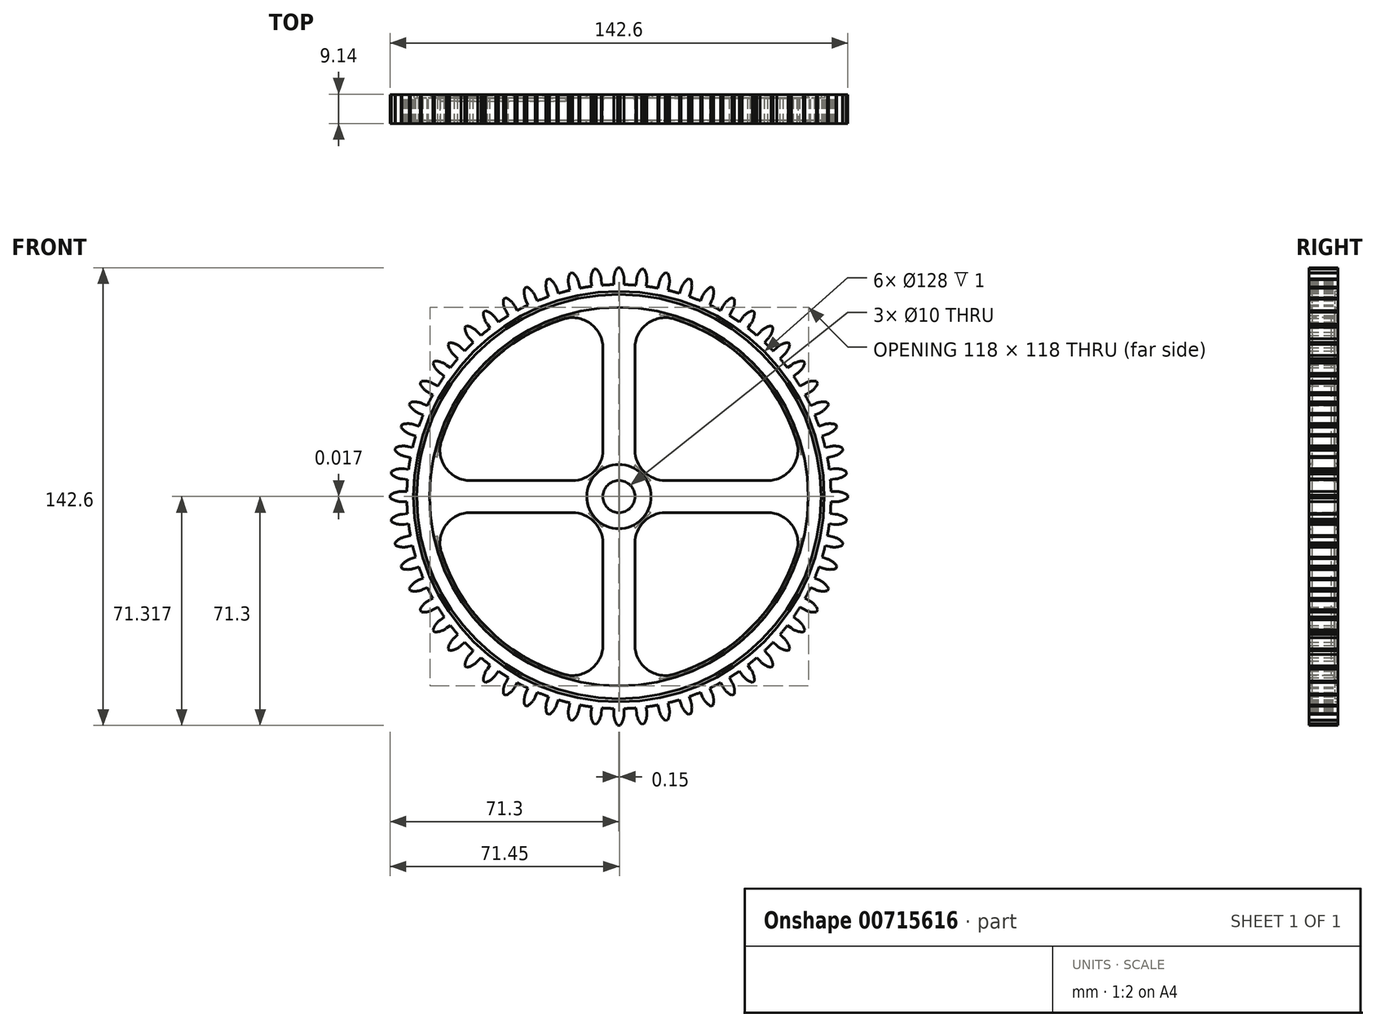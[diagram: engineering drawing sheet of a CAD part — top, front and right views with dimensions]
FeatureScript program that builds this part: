
annotation { "Feature Type Name" : "Feature", "Feature Type Description" : "" }
export const myFeature = defineFeature(function(context is Context, id is Id, definition is map)
    precondition{}
    {
        {
            var Q0;
            Q0=qCreatedBy(makeId("Front.planeOp"),FACE);
            var sketch = newSketch(context, id + "F0", { "sketchPlane" : qUnion([Q0])});
            skCircle(sketch, "E0", {"center": v(0, 0) * mm, "radius": 5 * mm});
            skCircle(sketch, "E1", {"center": v(0, 0) * mm, "radius": 66.1 * mm});
            skLineSegment(sketch, "E2", {"start": v(0, -77.77) * mm, "end": v(0, 74.62) * mm, "construction": true});
            skLineSegment(sketch, "E3", {"start": v(1.6, 66.08) * mm, "end": v(1.6, 67.83) * mm});
            skLineSegment(sketch, "E4", {"start": v(-1.6, 67.83) * mm, "end": v(-1.6, 66.08) * mm});
            skArc(sketch, "E5", {"start": v(-0.4, 71.3) * mm, "mid": v(-1.31, 69.54) * mm, "end": v(-1.6, 67.58) * mm});
            skArc(sketch, "E6.trimOffspring", {"start": v(1.6, 67.58) * mm, "mid": v(1.31, 69.54) * mm, "end": v(0.4, 71.3) * mm});
            skLineSegment(sketch, "E7", {"start": v(-0.4, 71.3) * mm, "end": v(0.4, 71.3) * mm});
            skLineSegment(sketch, "E8.1.0", {"start": v(-7.86, 70.87) * mm, "end": v(-7.05, 70.95) * mm});
            skArc(sketch, "E8.1.1", {"start": v(-5.47, 67.38) * mm, "mid": v(-5.96, 69.3) * mm, "end": v(-7.05, 70.95) * mm});
            skArc(sketch, "E8.1.2", {"start": v(-7.86, 70.87) * mm, "mid": v(-8.58, 69.02) * mm, "end": v(-8.66, 67.05) * mm});
            skLineSegment(sketch, "E8.1.3", {"start": v(-8.68, 67.3) * mm, "end": v(-8.5, 65.55) * mm});
            skLineSegment(sketch, "E8.1.4", {"start": v(-5.32, 65.89) * mm, "end": v(-5.5, 67.63) * mm});
            skLineSegment(sketch, "E8.2.0", {"start": v(-15.22, 69.66) * mm, "end": v(-14.43, 69.83) * mm});
            skArc(sketch, "E8.2.1", {"start": v(-12.49, 66.44) * mm, "mid": v(-13.17, 68.3) * mm, "end": v(-14.43, 69.83) * mm});
            skArc(sketch, "E8.2.2", {"start": v(-15.22, 69.66) * mm, "mid": v(-15.74, 67.75) * mm, "end": v(-15.62, 65.77) * mm});
            skLineSegment(sketch, "E8.2.3", {"start": v(-15.67, 66.02) * mm, "end": v(-15.3, 64.3) * mm});
            skLineSegment(sketch, "E8.2.4", {"start": v(-12.17, 64.97) * mm, "end": v(-12.54, 66.68) * mm});
            skLineSegment(sketch, "E9.1.3.0", {"start": v(-22.42, 67.68) * mm, "end": v(-21.64, 67.94) * mm});
            skArc(sketch, "E9.3.3.0", {"start": v(-19.36, 64.77) * mm, "mid": v(-20.24, 66.54) * mm, "end": v(-21.64, 67.94) * mm});
            skArc(sketch, "E9.7.3.0", {"start": v(-22.42, 67.68) * mm, "mid": v(-22.74, 65.73) * mm, "end": v(-22.4, 63.78) * mm});
            skLineSegment(sketch, "E9.11.3.0", {"start": v(-22.48, 64.02) * mm, "end": v(-21.94, 62.35) * mm});
            skLineSegment(sketch, "E9.14.3.0", {"start": v(-18.9, 63.34) * mm, "end": v(-19.44, 65) * mm});
            skLineSegment(sketch, "E9.1.4.0", {"start": v(-29.37, 64.97) * mm, "end": v(-28.63, 65.3) * mm});
            skArc(sketch, "E9.3.4.0", {"start": v(-26.03, 62.4) * mm, "mid": v(-27.08, 64.06) * mm, "end": v(-28.63, 65.3) * mm});
            skArc(sketch, "E9.7.4.0", {"start": v(-29.37, 64.97) * mm, "mid": v(-29.49, 63) * mm, "end": v(-28.95, 61.09) * mm});
            skLineSegment(sketch, "E9.11.4.0", {"start": v(-29.05, 61.32) * mm, "end": v(-28.34, 59.72) * mm});
            skLineSegment(sketch, "E9.14.4.0", {"start": v(-25.42, 61.02) * mm, "end": v(-26.13, 62.62) * mm});
            skLineSegment(sketch, "E9.1.5.0", {"start": v(-36, 61.54) * mm, "end": v(-35.3, 61.95) * mm});
            skArc(sketch, "E9.3.5.0", {"start": v(-32.4, 59.33) * mm, "mid": v(-33.63, 60.88) * mm, "end": v(-35.3, 61.95) * mm});
            skArc(sketch, "E9.7.5.0", {"start": v(-36, 61.54) * mm, "mid": v(-35.9, 59.57) * mm, "end": v(-35.18, 57.73) * mm});
            skLineSegment(sketch, "E9.11.5.0", {"start": v(-35.3, 57.94) * mm, "end": v(-34.43, 56.43) * mm});
            skLineSegment(sketch, "E9.14.5.0", {"start": v(-31.65, 58.03) * mm, "end": v(-32.53, 59.54) * mm});
            skLineSegment(sketch, "E9.1.6.0", {"start": v(-42.24, 57.44) * mm, "end": v(-41.58, 57.92) * mm});
            skArc(sketch, "E9.3.6.0", {"start": v(-38.43, 55.62) * mm, "mid": v(-39.81, 57.03) * mm, "end": v(-41.58, 57.92) * mm});
            skArc(sketch, "E9.7.6.0", {"start": v(-42.24, 57.44) * mm, "mid": v(-41.94, 55.49) * mm, "end": v(-41.02, 53.74) * mm});
            skLineSegment(sketch, "E9.11.6.0", {"start": v(-41.16, 53.94) * mm, "end": v(-40.14, 52.52) * mm});
            skLineSegment(sketch, "E9.14.6.0", {"start": v(-37.55, 54.4) * mm, "end": v(-38.58, 55.82) * mm});
            skLineSegment(sketch, "E9.1.7.0", {"start": v(-48.01, 52.71) * mm, "end": v(-47.4, 53.26) * mm});
            skArc(sketch, "E9.3.7.0", {"start": v(-44.03, 51.3) * mm, "mid": v(-45.56, 52.56) * mm, "end": v(-47.4, 53.26) * mm});
            skArc(sketch, "E9.7.7.0", {"start": v(-48.01, 52.71) * mm, "mid": v(-47.5, 50.8) * mm, "end": v(-46.41, 49.15) * mm});
            skLineSegment(sketch, "E9.11.7.0", {"start": v(-46.58, 49.34) * mm, "end": v(-45.4, 48.04) * mm});
            skLineSegment(sketch, "E9.14.7.0", {"start": v(-43.03, 50.18) * mm, "end": v(-44.2, 51.48) * mm});
            skLineSegment(sketch, "E9.1.8.0", {"start": v(-53.26, 47.4) * mm, "end": v(-52.71, 48.01) * mm});
            skArc(sketch, "E9.3.8.0", {"start": v(-49.15, 46.41) * mm, "mid": v(-50.8, 47.5) * mm, "end": v(-52.71, 48.01) * mm});
            skArc(sketch, "E9.7.8.0", {"start": v(-53.26, 47.4) * mm, "mid": v(-52.56, 45.56) * mm, "end": v(-51.3, 44.03) * mm});
            skLineSegment(sketch, "E9.11.8.0", {"start": v(-51.48, 44.2) * mm, "end": v(-50.18, 43.03) * mm});
            skLineSegment(sketch, "E9.14.8.0", {"start": v(-48.04, 45.4) * mm, "end": v(-49.34, 46.58) * mm});
            skLineSegment(sketch, "E9.1.9.0", {"start": v(-57.92, 41.58) * mm, "end": v(-57.44, 42.24) * mm});
            skArc(sketch, "E9.3.9.0", {"start": v(-53.74, 41.02) * mm, "mid": v(-55.49, 41.94) * mm, "end": v(-57.44, 42.24) * mm});
            skArc(sketch, "E9.7.9.0", {"start": v(-57.92, 41.58) * mm, "mid": v(-57.03, 39.81) * mm, "end": v(-55.62, 38.43) * mm});
            skLineSegment(sketch, "E9.11.9.0", {"start": v(-55.82, 38.58) * mm, "end": v(-54.4, 37.55) * mm});
            skLineSegment(sketch, "E9.14.9.0", {"start": v(-52.52, 40.14) * mm, "end": v(-53.94, 41.16) * mm});
            skLineSegment(sketch, "E9.1.10.0", {"start": v(-61.95, 35.3) * mm, "end": v(-61.54, 36) * mm});
            skArc(sketch, "E9.3.10.0", {"start": v(-57.73, 35.18) * mm, "mid": v(-59.57, 35.9) * mm, "end": v(-61.54, 36) * mm});
            skArc(sketch, "E9.7.10.0", {"start": v(-61.95, 35.3) * mm, "mid": v(-60.88, 33.63) * mm, "end": v(-59.33, 32.4) * mm});
            skLineSegment(sketch, "E9.11.10.0", {"start": v(-59.54, 32.53) * mm, "end": v(-58.03, 31.65) * mm});
            skLineSegment(sketch, "E9.14.10.0", {"start": v(-56.43, 34.43) * mm, "end": v(-57.94, 35.3) * mm});
            skLineSegment(sketch, "E9.1.11.0", {"start": v(-65.3, 28.63) * mm, "end": v(-64.97, 29.37) * mm});
            skArc(sketch, "E9.3.11.0", {"start": v(-61.09, 28.95) * mm, "mid": v(-63, 29.49) * mm, "end": v(-64.97, 29.37) * mm});
            skArc(sketch, "E9.7.11.0", {"start": v(-65.3, 28.63) * mm, "mid": v(-64.06, 27.08) * mm, "end": v(-62.4, 26.03) * mm});
            skLineSegment(sketch, "E9.11.11.0", {"start": v(-62.62, 26.13) * mm, "end": v(-61.02, 25.42) * mm});
            skLineSegment(sketch, "E9.14.11.0", {"start": v(-59.72, 28.34) * mm, "end": v(-61.32, 29.05) * mm});
            skLineSegment(sketch, "E9.1.12.0", {"start": v(-67.94, 21.64) * mm, "end": v(-67.68, 22.42) * mm});
            skArc(sketch, "E9.3.12.0", {"start": v(-63.78, 22.4) * mm, "mid": v(-65.73, 22.74) * mm, "end": v(-67.68, 22.42) * mm});
            skArc(sketch, "E9.7.12.0", {"start": v(-67.94, 21.64) * mm, "mid": v(-66.54, 20.24) * mm, "end": v(-64.77, 19.36) * mm});
            skLineSegment(sketch, "E9.11.12.0", {"start": v(-65, 19.44) * mm, "end": v(-63.34, 18.9) * mm});
            skLineSegment(sketch, "E9.14.12.0", {"start": v(-62.35, 21.94) * mm, "end": v(-64.02, 22.48) * mm});
            skLineSegment(sketch, "E9.1.13.0", {"start": v(-69.83, 14.43) * mm, "end": v(-69.66, 15.22) * mm});
            skArc(sketch, "E9.3.13.0", {"start": v(-65.77, 15.62) * mm, "mid": v(-67.75, 15.74) * mm, "end": v(-69.66, 15.22) * mm});
            skArc(sketch, "E9.7.13.0", {"start": v(-69.83, 14.43) * mm, "mid": v(-68.3, 13.17) * mm, "end": v(-66.44, 12.49) * mm});
            skLineSegment(sketch, "E9.11.13.0", {"start": v(-66.68, 12.54) * mm, "end": v(-64.97, 12.17) * mm});
            skLineSegment(sketch, "E9.14.13.0", {"start": v(-64.3, 15.3) * mm, "end": v(-66.02, 15.67) * mm});
            skLineSegment(sketch, "E9.1.14.0", {"start": v(-70.95, 7.05) * mm, "end": v(-70.87, 7.86) * mm});
            skArc(sketch, "E9.3.14.0", {"start": v(-67.05, 8.66) * mm, "mid": v(-69.02, 8.58) * mm, "end": v(-70.87, 7.86) * mm});
            skArc(sketch, "E9.7.14.0", {"start": v(-70.95, 7.05) * mm, "mid": v(-69.3, 5.96) * mm, "end": v(-67.38, 5.47) * mm});
            skLineSegment(sketch, "E9.11.14.0", {"start": v(-67.63, 5.5) * mm, "end": v(-65.89, 5.32) * mm});
            skLineSegment(sketch, "E9.14.14.0", {"start": v(-65.55, 8.5) * mm, "end": v(-67.3, 8.68) * mm});
            skLineSegment(sketch, "E9.1.15.0", {"start": v(-71.3, -0.4) * mm, "end": v(-71.3, 0.4) * mm});
            skArc(sketch, "E9.3.15.0", {"start": v(-67.58, 1.6) * mm, "mid": v(-69.54, 1.31) * mm, "end": v(-71.3, 0.4) * mm});
            skArc(sketch, "E9.7.15.0", {"start": v(-71.3, -0.4) * mm, "mid": v(-69.54, -1.31) * mm, "end": v(-67.58, -1.6) * mm});
            skLineSegment(sketch, "E9.11.15.0", {"start": v(-67.83, -1.6) * mm, "end": v(-66.08, -1.6) * mm});
            skLineSegment(sketch, "E9.14.15.0", {"start": v(-66.08, 1.6) * mm, "end": v(-67.83, 1.6) * mm});
            skLineSegment(sketch, "E9.1.16.0", {"start": v(-70.87, -7.86) * mm, "end": v(-70.95, -7.05) * mm});
            skArc(sketch, "E9.3.16.0", {"start": v(-67.38, -5.47) * mm, "mid": v(-69.3, -5.96) * mm, "end": v(-70.95, -7.05) * mm});
            skArc(sketch, "E9.7.16.0", {"start": v(-70.87, -7.86) * mm, "mid": v(-69.02, -8.58) * mm, "end": v(-67.05, -8.66) * mm});
            skLineSegment(sketch, "E9.11.16.0", {"start": v(-67.3, -8.68) * mm, "end": v(-65.55, -8.5) * mm});
            skLineSegment(sketch, "E9.14.16.0", {"start": v(-65.89, -5.32) * mm, "end": v(-67.63, -5.5) * mm});
            skLineSegment(sketch, "E9.1.17.0", {"start": v(-69.66, -15.22) * mm, "end": v(-69.83, -14.43) * mm});
            skArc(sketch, "E9.3.17.0", {"start": v(-66.44, -12.49) * mm, "mid": v(-68.3, -13.17) * mm, "end": v(-69.83, -14.43) * mm});
            skArc(sketch, "E9.7.17.0", {"start": v(-69.66, -15.22) * mm, "mid": v(-67.75, -15.74) * mm, "end": v(-65.77, -15.62) * mm});
            skLineSegment(sketch, "E9.11.17.0", {"start": v(-66.02, -15.67) * mm, "end": v(-64.3, -15.3) * mm});
            skLineSegment(sketch, "E9.14.17.0", {"start": v(-64.97, -12.17) * mm, "end": v(-66.68, -12.54) * mm});
            skLineSegment(sketch, "E9.1.18.0", {"start": v(-67.68, -22.42) * mm, "end": v(-67.94, -21.64) * mm});
            skArc(sketch, "E9.3.18.0", {"start": v(-64.77, -19.36) * mm, "mid": v(-66.54, -20.24) * mm, "end": v(-67.94, -21.64) * mm});
            skArc(sketch, "E9.7.18.0", {"start": v(-67.68, -22.42) * mm, "mid": v(-65.73, -22.74) * mm, "end": v(-63.78, -22.4) * mm});
            skLineSegment(sketch, "E9.11.18.0", {"start": v(-64.02, -22.48) * mm, "end": v(-62.35, -21.94) * mm});
            skLineSegment(sketch, "E9.14.18.0", {"start": v(-63.34, -18.9) * mm, "end": v(-65, -19.44) * mm});
            skLineSegment(sketch, "E9.1.19.0", {"start": v(-64.97, -29.37) * mm, "end": v(-65.3, -28.63) * mm});
            skArc(sketch, "E9.3.19.0", {"start": v(-62.4, -26.03) * mm, "mid": v(-64.06, -27.08) * mm, "end": v(-65.3, -28.63) * mm});
            skArc(sketch, "E9.7.19.0", {"start": v(-64.97, -29.37) * mm, "mid": v(-63, -29.49) * mm, "end": v(-61.09, -28.95) * mm});
            skLineSegment(sketch, "E9.11.19.0", {"start": v(-61.32, -29.05) * mm, "end": v(-59.72, -28.34) * mm});
            skLineSegment(sketch, "E9.14.19.0", {"start": v(-61.02, -25.42) * mm, "end": v(-62.62, -26.13) * mm});
            skLineSegment(sketch, "E9.1.20.0", {"start": v(-61.54, -36) * mm, "end": v(-61.95, -35.3) * mm});
            skArc(sketch, "E9.3.20.0", {"start": v(-59.33, -32.4) * mm, "mid": v(-60.88, -33.63) * mm, "end": v(-61.95, -35.3) * mm});
            skArc(sketch, "E9.7.20.0", {"start": v(-61.54, -36) * mm, "mid": v(-59.57, -35.9) * mm, "end": v(-57.73, -35.18) * mm});
            skLineSegment(sketch, "E9.11.20.0", {"start": v(-57.94, -35.3) * mm, "end": v(-56.43, -34.43) * mm});
            skLineSegment(sketch, "E9.14.20.0", {"start": v(-58.03, -31.65) * mm, "end": v(-59.54, -32.53) * mm});
            skLineSegment(sketch, "E9.1.21.0", {"start": v(-57.44, -42.24) * mm, "end": v(-57.92, -41.58) * mm});
            skArc(sketch, "E9.3.21.0", {"start": v(-55.62, -38.43) * mm, "mid": v(-57.03, -39.81) * mm, "end": v(-57.92, -41.58) * mm});
            skArc(sketch, "E9.7.21.0", {"start": v(-57.44, -42.24) * mm, "mid": v(-55.49, -41.94) * mm, "end": v(-53.74, -41.02) * mm});
            skLineSegment(sketch, "E9.11.21.0", {"start": v(-53.94, -41.16) * mm, "end": v(-52.52, -40.14) * mm});
            skLineSegment(sketch, "E9.14.21.0", {"start": v(-54.4, -37.55) * mm, "end": v(-55.82, -38.58) * mm});
            skLineSegment(sketch, "E9.1.22.0", {"start": v(-52.71, -48.01) * mm, "end": v(-53.26, -47.4) * mm});
            skArc(sketch, "E9.3.22.0", {"start": v(-51.3, -44.03) * mm, "mid": v(-52.56, -45.56) * mm, "end": v(-53.26, -47.4) * mm});
            skArc(sketch, "E9.7.22.0", {"start": v(-52.71, -48.01) * mm, "mid": v(-50.8, -47.5) * mm, "end": v(-49.15, -46.41) * mm});
            skLineSegment(sketch, "E9.11.22.0", {"start": v(-49.34, -46.58) * mm, "end": v(-48.04, -45.4) * mm});
            skLineSegment(sketch, "E9.14.22.0", {"start": v(-50.18, -43.03) * mm, "end": v(-51.48, -44.2) * mm});
            skLineSegment(sketch, "E9.1.23.0", {"start": v(-47.4, -53.26) * mm, "end": v(-48.01, -52.71) * mm});
            skArc(sketch, "E9.3.23.0", {"start": v(-46.41, -49.15) * mm, "mid": v(-47.5, -50.8) * mm, "end": v(-48.01, -52.71) * mm});
            skArc(sketch, "E9.7.23.0", {"start": v(-47.4, -53.26) * mm, "mid": v(-45.56, -52.56) * mm, "end": v(-44.03, -51.3) * mm});
            skLineSegment(sketch, "E9.11.23.0", {"start": v(-44.2, -51.48) * mm, "end": v(-43.03, -50.18) * mm});
            skLineSegment(sketch, "E9.14.23.0", {"start": v(-45.4, -48.04) * mm, "end": v(-46.58, -49.34) * mm});
            skLineSegment(sketch, "E9.1.24.0", {"start": v(-41.58, -57.92) * mm, "end": v(-42.24, -57.44) * mm});
            skArc(sketch, "E9.3.24.0", {"start": v(-41.02, -53.74) * mm, "mid": v(-41.94, -55.49) * mm, "end": v(-42.24, -57.44) * mm});
            skArc(sketch, "E9.7.24.0", {"start": v(-41.58, -57.92) * mm, "mid": v(-39.81, -57.03) * mm, "end": v(-38.43, -55.62) * mm});
            skLineSegment(sketch, "E9.11.24.0", {"start": v(-38.58, -55.82) * mm, "end": v(-37.55, -54.4) * mm});
            skLineSegment(sketch, "E9.14.24.0", {"start": v(-40.14, -52.52) * mm, "end": v(-41.16, -53.94) * mm});
            skLineSegment(sketch, "E9.1.25.0", {"start": v(-35.3, -61.95) * mm, "end": v(-36, -61.54) * mm});
            skArc(sketch, "E9.3.25.0", {"start": v(-35.18, -57.73) * mm, "mid": v(-35.9, -59.57) * mm, "end": v(-36, -61.54) * mm});
            skArc(sketch, "E9.7.25.0", {"start": v(-35.3, -61.95) * mm, "mid": v(-33.63, -60.88) * mm, "end": v(-32.4, -59.33) * mm});
            skLineSegment(sketch, "E9.11.25.0", {"start": v(-32.53, -59.54) * mm, "end": v(-31.65, -58.03) * mm});
            skLineSegment(sketch, "E9.14.25.0", {"start": v(-34.43, -56.43) * mm, "end": v(-35.3, -57.94) * mm});
            skLineSegment(sketch, "E9.1.26.0", {"start": v(-28.63, -65.3) * mm, "end": v(-29.37, -64.97) * mm});
            skArc(sketch, "E9.3.26.0", {"start": v(-28.95, -61.09) * mm, "mid": v(-29.49, -63) * mm, "end": v(-29.37, -64.97) * mm});
            skArc(sketch, "E9.7.26.0", {"start": v(-28.63, -65.3) * mm, "mid": v(-27.08, -64.06) * mm, "end": v(-26.03, -62.4) * mm});
            skLineSegment(sketch, "E9.11.26.0", {"start": v(-26.13, -62.62) * mm, "end": v(-25.42, -61.02) * mm});
            skLineSegment(sketch, "E9.14.26.0", {"start": v(-28.34, -59.72) * mm, "end": v(-29.05, -61.32) * mm});
            skLineSegment(sketch, "E9.1.27.0", {"start": v(-21.64, -67.94) * mm, "end": v(-22.42, -67.68) * mm});
            skArc(sketch, "E9.3.27.0", {"start": v(-22.4, -63.78) * mm, "mid": v(-22.74, -65.73) * mm, "end": v(-22.42, -67.68) * mm});
            skArc(sketch, "E9.7.27.0", {"start": v(-21.64, -67.94) * mm, "mid": v(-20.24, -66.54) * mm, "end": v(-19.36, -64.77) * mm});
            skLineSegment(sketch, "E9.11.27.0", {"start": v(-19.44, -65) * mm, "end": v(-18.9, -63.34) * mm});
            skLineSegment(sketch, "E9.14.27.0", {"start": v(-21.94, -62.35) * mm, "end": v(-22.48, -64.02) * mm});
            skLineSegment(sketch, "E9.1.28.0", {"start": v(-14.43, -69.83) * mm, "end": v(-15.22, -69.66) * mm});
            skArc(sketch, "E9.3.28.0", {"start": v(-15.62, -65.77) * mm, "mid": v(-15.74, -67.75) * mm, "end": v(-15.22, -69.66) * mm});
            skArc(sketch, "E9.7.28.0", {"start": v(-14.43, -69.83) * mm, "mid": v(-13.17, -68.3) * mm, "end": v(-12.49, -66.44) * mm});
            skLineSegment(sketch, "E9.11.28.0", {"start": v(-12.54, -66.68) * mm, "end": v(-12.17, -64.97) * mm});
            skLineSegment(sketch, "E9.14.28.0", {"start": v(-15.3, -64.3) * mm, "end": v(-15.67, -66.02) * mm});
            skLineSegment(sketch, "E9.1.29.0", {"start": v(-7.05, -70.95) * mm, "end": v(-7.86, -70.87) * mm});
            skArc(sketch, "E9.3.29.0", {"start": v(-8.66, -67.05) * mm, "mid": v(-8.58, -69.02) * mm, "end": v(-7.86, -70.87) * mm});
            skArc(sketch, "E9.7.29.0", {"start": v(-7.05, -70.95) * mm, "mid": v(-5.96, -69.3) * mm, "end": v(-5.47, -67.38) * mm});
            skLineSegment(sketch, "E9.11.29.0", {"start": v(-5.5, -67.63) * mm, "end": v(-5.32, -65.89) * mm});
            skLineSegment(sketch, "E9.14.29.0", {"start": v(-8.5, -65.55) * mm, "end": v(-8.68, -67.3) * mm});
            skLineSegment(sketch, "E9.1.30.0", {"start": v(0.4, -71.3) * mm, "end": v(-0.4, -71.3) * mm});
            skArc(sketch, "E9.3.30.0", {"start": v(-1.6, -67.58) * mm, "mid": v(-1.31, -69.54) * mm, "end": v(-0.4, -71.3) * mm});
            skArc(sketch, "E9.7.30.0", {"start": v(0.4, -71.3) * mm, "mid": v(1.31, -69.54) * mm, "end": v(1.6, -67.58) * mm});
            skLineSegment(sketch, "E9.11.30.0", {"start": v(1.6, -67.83) * mm, "end": v(1.6, -66.08) * mm});
            skLineSegment(sketch, "E9.14.30.0", {"start": v(-1.6, -66.08) * mm, "end": v(-1.6, -67.83) * mm});
            skLineSegment(sketch, "E9.1.31.0", {"start": v(7.86, -70.87) * mm, "end": v(7.05, -70.95) * mm});
            skArc(sketch, "E9.3.31.0", {"start": v(5.47, -67.38) * mm, "mid": v(5.96, -69.3) * mm, "end": v(7.05, -70.95) * mm});
            skArc(sketch, "E9.7.31.0", {"start": v(7.86, -70.87) * mm, "mid": v(8.58, -69.02) * mm, "end": v(8.66, -67.05) * mm});
            skLineSegment(sketch, "E9.11.31.0", {"start": v(8.68, -67.3) * mm, "end": v(8.5, -65.55) * mm});
            skLineSegment(sketch, "E9.14.31.0", {"start": v(5.32, -65.89) * mm, "end": v(5.5, -67.63) * mm});
            skLineSegment(sketch, "E9.1.32.0", {"start": v(15.22, -69.66) * mm, "end": v(14.43, -69.83) * mm});
            skArc(sketch, "E9.3.32.0", {"start": v(12.49, -66.44) * mm, "mid": v(13.17, -68.3) * mm, "end": v(14.43, -69.83) * mm});
            skArc(sketch, "E9.7.32.0", {"start": v(15.22, -69.66) * mm, "mid": v(15.74, -67.75) * mm, "end": v(15.62, -65.77) * mm});
            skLineSegment(sketch, "E9.11.32.0", {"start": v(15.67, -66.02) * mm, "end": v(15.3, -64.3) * mm});
            skLineSegment(sketch, "E9.14.32.0", {"start": v(12.17, -64.97) * mm, "end": v(12.54, -66.68) * mm});
            skLineSegment(sketch, "E9.1.33.0", {"start": v(22.42, -67.68) * mm, "end": v(21.64, -67.94) * mm});
            skArc(sketch, "E9.3.33.0", {"start": v(19.36, -64.77) * mm, "mid": v(20.24, -66.54) * mm, "end": v(21.64, -67.94) * mm});
            skArc(sketch, "E9.7.33.0", {"start": v(22.42, -67.68) * mm, "mid": v(22.74, -65.73) * mm, "end": v(22.4, -63.78) * mm});
            skLineSegment(sketch, "E9.11.33.0", {"start": v(22.48, -64.02) * mm, "end": v(21.94, -62.35) * mm});
            skLineSegment(sketch, "E9.14.33.0", {"start": v(18.9, -63.34) * mm, "end": v(19.44, -65) * mm});
            skLineSegment(sketch, "E9.1.34.0", {"start": v(29.37, -64.97) * mm, "end": v(28.63, -65.3) * mm});
            skArc(sketch, "E9.3.34.0", {"start": v(26.03, -62.4) * mm, "mid": v(27.08, -64.06) * mm, "end": v(28.63, -65.3) * mm});
            skArc(sketch, "E9.7.34.0", {"start": v(29.37, -64.97) * mm, "mid": v(29.49, -63) * mm, "end": v(28.95, -61.09) * mm});
            skLineSegment(sketch, "E9.11.34.0", {"start": v(29.05, -61.32) * mm, "end": v(28.34, -59.72) * mm});
            skLineSegment(sketch, "E9.14.34.0", {"start": v(25.42, -61.02) * mm, "end": v(26.13, -62.62) * mm});
            skLineSegment(sketch, "E9.1.35.0", {"start": v(36, -61.54) * mm, "end": v(35.3, -61.95) * mm});
            skArc(sketch, "E9.3.35.0", {"start": v(32.4, -59.33) * mm, "mid": v(33.63, -60.88) * mm, "end": v(35.3, -61.95) * mm});
            skArc(sketch, "E9.7.35.0", {"start": v(36, -61.54) * mm, "mid": v(35.9, -59.57) * mm, "end": v(35.18, -57.73) * mm});
            skLineSegment(sketch, "E9.11.35.0", {"start": v(35.3, -57.94) * mm, "end": v(34.43, -56.43) * mm});
            skLineSegment(sketch, "E9.14.35.0", {"start": v(31.65, -58.03) * mm, "end": v(32.53, -59.54) * mm});
            skLineSegment(sketch, "E9.1.36.0", {"start": v(42.24, -57.44) * mm, "end": v(41.58, -57.92) * mm});
            skArc(sketch, "E9.3.36.0", {"start": v(38.43, -55.62) * mm, "mid": v(39.81, -57.03) * mm, "end": v(41.58, -57.92) * mm});
            skArc(sketch, "E9.7.36.0", {"start": v(42.24, -57.44) * mm, "mid": v(41.94, -55.49) * mm, "end": v(41.02, -53.74) * mm});
            skLineSegment(sketch, "E9.11.36.0", {"start": v(41.16, -53.94) * mm, "end": v(40.14, -52.52) * mm});
            skLineSegment(sketch, "E9.14.36.0", {"start": v(37.55, -54.4) * mm, "end": v(38.58, -55.82) * mm});
            skLineSegment(sketch, "E9.1.37.0", {"start": v(48.01, -52.71) * mm, "end": v(47.4, -53.26) * mm});
            skArc(sketch, "E9.3.37.0", {"start": v(44.03, -51.3) * mm, "mid": v(45.56, -52.56) * mm, "end": v(47.4, -53.26) * mm});
            skArc(sketch, "E9.7.37.0", {"start": v(48.01, -52.71) * mm, "mid": v(47.5, -50.8) * mm, "end": v(46.41, -49.15) * mm});
            skLineSegment(sketch, "E9.11.37.0", {"start": v(46.58, -49.34) * mm, "end": v(45.4, -48.04) * mm});
            skLineSegment(sketch, "E9.14.37.0", {"start": v(43.03, -50.18) * mm, "end": v(44.2, -51.48) * mm});
            skLineSegment(sketch, "E9.1.38.0", {"start": v(53.26, -47.4) * mm, "end": v(52.71, -48.01) * mm});
            skArc(sketch, "E9.3.38.0", {"start": v(49.15, -46.41) * mm, "mid": v(50.8, -47.5) * mm, "end": v(52.71, -48.01) * mm});
            skArc(sketch, "E9.7.38.0", {"start": v(53.26, -47.4) * mm, "mid": v(52.56, -45.56) * mm, "end": v(51.3, -44.03) * mm});
            skLineSegment(sketch, "E9.11.38.0", {"start": v(51.48, -44.2) * mm, "end": v(50.18, -43.03) * mm});
            skLineSegment(sketch, "E9.14.38.0", {"start": v(48.04, -45.4) * mm, "end": v(49.34, -46.58) * mm});
            skLineSegment(sketch, "E9.1.39.0", {"start": v(57.92, -41.58) * mm, "end": v(57.44, -42.24) * mm});
            skArc(sketch, "E9.3.39.0", {"start": v(53.74, -41.02) * mm, "mid": v(55.49, -41.94) * mm, "end": v(57.44, -42.24) * mm});
            skArc(sketch, "E9.7.39.0", {"start": v(57.92, -41.58) * mm, "mid": v(57.03, -39.81) * mm, "end": v(55.62, -38.43) * mm});
            skLineSegment(sketch, "E9.11.39.0", {"start": v(55.82, -38.58) * mm, "end": v(54.4, -37.55) * mm});
            skLineSegment(sketch, "E9.14.39.0", {"start": v(52.52, -40.14) * mm, "end": v(53.94, -41.16) * mm});
            skLineSegment(sketch, "E9.1.40.0", {"start": v(61.95, -35.3) * mm, "end": v(61.54, -36) * mm});
            skArc(sketch, "E9.3.40.0", {"start": v(57.73, -35.18) * mm, "mid": v(59.57, -35.9) * mm, "end": v(61.54, -36) * mm});
            skArc(sketch, "E9.7.40.0", {"start": v(61.95, -35.3) * mm, "mid": v(60.88, -33.63) * mm, "end": v(59.33, -32.4) * mm});
            skLineSegment(sketch, "E9.11.40.0", {"start": v(59.54, -32.53) * mm, "end": v(58.03, -31.65) * mm});
            skLineSegment(sketch, "E9.14.40.0", {"start": v(56.43, -34.43) * mm, "end": v(57.94, -35.3) * mm});
            skLineSegment(sketch, "E9.1.41.0", {"start": v(65.3, -28.63) * mm, "end": v(64.97, -29.37) * mm});
            skArc(sketch, "E9.3.41.0", {"start": v(61.09, -28.95) * mm, "mid": v(63, -29.49) * mm, "end": v(64.97, -29.37) * mm});
            skArc(sketch, "E9.7.41.0", {"start": v(65.3, -28.63) * mm, "mid": v(64.06, -27.08) * mm, "end": v(62.4, -26.03) * mm});
            skLineSegment(sketch, "E9.11.41.0", {"start": v(62.62, -26.13) * mm, "end": v(61.02, -25.42) * mm});
            skLineSegment(sketch, "E9.14.41.0", {"start": v(59.72, -28.34) * mm, "end": v(61.32, -29.05) * mm});
            skLineSegment(sketch, "E9.1.42.0", {"start": v(67.94, -21.64) * mm, "end": v(67.68, -22.42) * mm});
            skArc(sketch, "E9.3.42.0", {"start": v(63.78, -22.4) * mm, "mid": v(65.73, -22.74) * mm, "end": v(67.68, -22.42) * mm});
            skArc(sketch, "E9.7.42.0", {"start": v(67.94, -21.64) * mm, "mid": v(66.54, -20.24) * mm, "end": v(64.77, -19.36) * mm});
            skLineSegment(sketch, "E9.11.42.0", {"start": v(65, -19.44) * mm, "end": v(63.34, -18.9) * mm});
            skLineSegment(sketch, "E9.14.42.0", {"start": v(62.35, -21.94) * mm, "end": v(64.02, -22.48) * mm});
            skLineSegment(sketch, "E9.1.43.0", {"start": v(69.83, -14.43) * mm, "end": v(69.66, -15.22) * mm});
            skArc(sketch, "E9.3.43.0", {"start": v(65.77, -15.62) * mm, "mid": v(67.75, -15.74) * mm, "end": v(69.66, -15.22) * mm});
            skArc(sketch, "E9.7.43.0", {"start": v(69.83, -14.43) * mm, "mid": v(68.3, -13.17) * mm, "end": v(66.44, -12.49) * mm});
            skLineSegment(sketch, "E9.11.43.0", {"start": v(66.68, -12.54) * mm, "end": v(64.97, -12.17) * mm});
            skLineSegment(sketch, "E9.14.43.0", {"start": v(64.3, -15.3) * mm, "end": v(66.02, -15.67) * mm});
            skLineSegment(sketch, "E9.1.44.0", {"start": v(70.95, -7.05) * mm, "end": v(70.87, -7.86) * mm});
            skArc(sketch, "E9.3.44.0", {"start": v(67.05, -8.66) * mm, "mid": v(69.02, -8.58) * mm, "end": v(70.87, -7.86) * mm});
            skArc(sketch, "E9.7.44.0", {"start": v(70.95, -7.05) * mm, "mid": v(69.3, -5.96) * mm, "end": v(67.38, -5.47) * mm});
            skLineSegment(sketch, "E9.11.44.0", {"start": v(67.63, -5.5) * mm, "end": v(65.89, -5.32) * mm});
            skLineSegment(sketch, "E9.14.44.0", {"start": v(65.55, -8.5) * mm, "end": v(67.3, -8.68) * mm});
            skLineSegment(sketch, "E9.1.45.0", {"start": v(71.3, 0.4) * mm, "end": v(71.3, -0.4) * mm});
            skArc(sketch, "E9.3.45.0", {"start": v(67.58, -1.6) * mm, "mid": v(69.54, -1.31) * mm, "end": v(71.3, -0.4) * mm});
            skArc(sketch, "E9.7.45.0", {"start": v(71.3, 0.4) * mm, "mid": v(69.54, 1.31) * mm, "end": v(67.58, 1.6) * mm});
            skLineSegment(sketch, "E9.11.45.0", {"start": v(67.83, 1.6) * mm, "end": v(66.08, 1.6) * mm});
            skLineSegment(sketch, "E9.14.45.0", {"start": v(66.08, -1.6) * mm, "end": v(67.83, -1.6) * mm});
            skLineSegment(sketch, "E9.1.46.0", {"start": v(70.87, 7.86) * mm, "end": v(70.95, 7.05) * mm});
            skArc(sketch, "E9.3.46.0", {"start": v(67.38, 5.47) * mm, "mid": v(69.3, 5.96) * mm, "end": v(70.95, 7.05) * mm});
            skArc(sketch, "E9.7.46.0", {"start": v(70.87, 7.86) * mm, "mid": v(69.02, 8.58) * mm, "end": v(67.05, 8.66) * mm});
            skLineSegment(sketch, "E9.11.46.0", {"start": v(67.3, 8.68) * mm, "end": v(65.55, 8.5) * mm});
            skLineSegment(sketch, "E9.14.46.0", {"start": v(65.89, 5.32) * mm, "end": v(67.63, 5.5) * mm});
            skLineSegment(sketch, "E9.1.47.0", {"start": v(69.66, 15.22) * mm, "end": v(69.83, 14.43) * mm});
            skArc(sketch, "E9.3.47.0", {"start": v(66.44, 12.49) * mm, "mid": v(68.3, 13.17) * mm, "end": v(69.83, 14.43) * mm});
            skArc(sketch, "E9.7.47.0", {"start": v(69.66, 15.22) * mm, "mid": v(67.75, 15.74) * mm, "end": v(65.77, 15.62) * mm});
            skLineSegment(sketch, "E9.11.47.0", {"start": v(66.02, 15.67) * mm, "end": v(64.3, 15.3) * mm});
            skLineSegment(sketch, "E9.14.47.0", {"start": v(64.97, 12.17) * mm, "end": v(66.68, 12.54) * mm});
            skLineSegment(sketch, "E9.1.48.0", {"start": v(67.68, 22.42) * mm, "end": v(67.94, 21.64) * mm});
            skArc(sketch, "E9.3.48.0", {"start": v(64.77, 19.36) * mm, "mid": v(66.54, 20.24) * mm, "end": v(67.94, 21.64) * mm});
            skArc(sketch, "E9.7.48.0", {"start": v(67.68, 22.42) * mm, "mid": v(65.73, 22.74) * mm, "end": v(63.78, 22.4) * mm});
            skLineSegment(sketch, "E9.11.48.0", {"start": v(64.02, 22.48) * mm, "end": v(62.35, 21.94) * mm});
            skLineSegment(sketch, "E9.14.48.0", {"start": v(63.34, 18.9) * mm, "end": v(65, 19.44) * mm});
            skLineSegment(sketch, "E9.1.49.0", {"start": v(64.97, 29.37) * mm, "end": v(65.3, 28.63) * mm});
            skArc(sketch, "E9.3.49.0", {"start": v(62.4, 26.03) * mm, "mid": v(64.06, 27.08) * mm, "end": v(65.3, 28.63) * mm});
            skArc(sketch, "E9.7.49.0", {"start": v(64.97, 29.37) * mm, "mid": v(63, 29.49) * mm, "end": v(61.09, 28.95) * mm});
            skLineSegment(sketch, "E9.11.49.0", {"start": v(61.32, 29.05) * mm, "end": v(59.72, 28.34) * mm});
            skLineSegment(sketch, "E9.14.49.0", {"start": v(61.02, 25.42) * mm, "end": v(62.62, 26.13) * mm});
            skLineSegment(sketch, "E9.1.50.0", {"start": v(61.54, 36) * mm, "end": v(61.95, 35.3) * mm});
            skArc(sketch, "E9.3.50.0", {"start": v(59.33, 32.4) * mm, "mid": v(60.88, 33.63) * mm, "end": v(61.95, 35.3) * mm});
            skArc(sketch, "E9.7.50.0", {"start": v(61.54, 36) * mm, "mid": v(59.57, 35.9) * mm, "end": v(57.73, 35.18) * mm});
            skLineSegment(sketch, "E9.11.50.0", {"start": v(57.94, 35.3) * mm, "end": v(56.43, 34.43) * mm});
            skLineSegment(sketch, "E9.14.50.0", {"start": v(58.03, 31.65) * mm, "end": v(59.54, 32.53) * mm});
            skLineSegment(sketch, "E9.1.51.0", {"start": v(57.44, 42.24) * mm, "end": v(57.92, 41.58) * mm});
            skArc(sketch, "E9.3.51.0", {"start": v(55.62, 38.43) * mm, "mid": v(57.03, 39.81) * mm, "end": v(57.92, 41.58) * mm});
            skArc(sketch, "E9.7.51.0", {"start": v(57.44, 42.24) * mm, "mid": v(55.49, 41.94) * mm, "end": v(53.74, 41.02) * mm});
            skLineSegment(sketch, "E9.11.51.0", {"start": v(53.94, 41.16) * mm, "end": v(52.52, 40.14) * mm});
            skLineSegment(sketch, "E9.14.51.0", {"start": v(54.4, 37.55) * mm, "end": v(55.82, 38.58) * mm});
            skLineSegment(sketch, "E9.1.52.0", {"start": v(52.71, 48.01) * mm, "end": v(53.26, 47.4) * mm});
            skArc(sketch, "E9.3.52.0", {"start": v(51.3, 44.03) * mm, "mid": v(52.56, 45.56) * mm, "end": v(53.26, 47.4) * mm});
            skArc(sketch, "E9.7.52.0", {"start": v(52.71, 48.01) * mm, "mid": v(50.8, 47.5) * mm, "end": v(49.15, 46.41) * mm});
            skLineSegment(sketch, "E9.11.52.0", {"start": v(49.34, 46.58) * mm, "end": v(48.04, 45.4) * mm});
            skLineSegment(sketch, "E9.14.52.0", {"start": v(50.18, 43.03) * mm, "end": v(51.48, 44.2) * mm});
            skLineSegment(sketch, "E9.1.53.0", {"start": v(47.4, 53.26) * mm, "end": v(48.01, 52.71) * mm});
            skArc(sketch, "E9.3.53.0", {"start": v(46.41, 49.15) * mm, "mid": v(47.5, 50.8) * mm, "end": v(48.01, 52.71) * mm});
            skArc(sketch, "E9.7.53.0", {"start": v(47.4, 53.26) * mm, "mid": v(45.56, 52.56) * mm, "end": v(44.03, 51.3) * mm});
            skLineSegment(sketch, "E9.11.53.0", {"start": v(44.2, 51.48) * mm, "end": v(43.03, 50.18) * mm});
            skLineSegment(sketch, "E9.14.53.0", {"start": v(45.4, 48.04) * mm, "end": v(46.58, 49.34) * mm});
            skLineSegment(sketch, "E9.1.54.0", {"start": v(41.58, 57.92) * mm, "end": v(42.24, 57.44) * mm});
            skArc(sketch, "E9.3.54.0", {"start": v(41.02, 53.74) * mm, "mid": v(41.94, 55.49) * mm, "end": v(42.24, 57.44) * mm});
            skArc(sketch, "E9.7.54.0", {"start": v(41.58, 57.92) * mm, "mid": v(39.81, 57.03) * mm, "end": v(38.43, 55.62) * mm});
            skLineSegment(sketch, "E9.11.54.0", {"start": v(38.58, 55.82) * mm, "end": v(37.55, 54.4) * mm});
            skLineSegment(sketch, "E9.14.54.0", {"start": v(40.14, 52.52) * mm, "end": v(41.16, 53.94) * mm});
            skLineSegment(sketch, "E9.1.55.0", {"start": v(35.3, 61.95) * mm, "end": v(36, 61.54) * mm});
            skArc(sketch, "E9.3.55.0", {"start": v(35.18, 57.73) * mm, "mid": v(35.9, 59.57) * mm, "end": v(36, 61.54) * mm});
            skArc(sketch, "E9.7.55.0", {"start": v(35.3, 61.95) * mm, "mid": v(33.63, 60.88) * mm, "end": v(32.4, 59.33) * mm});
            skLineSegment(sketch, "E9.11.55.0", {"start": v(32.53, 59.54) * mm, "end": v(31.65, 58.03) * mm});
            skLineSegment(sketch, "E9.14.55.0", {"start": v(34.43, 56.43) * mm, "end": v(35.3, 57.94) * mm});
            skLineSegment(sketch, "E9.1.56.0", {"start": v(28.63, 65.3) * mm, "end": v(29.37, 64.97) * mm});
            skArc(sketch, "E9.3.56.0", {"start": v(28.95, 61.09) * mm, "mid": v(29.49, 63) * mm, "end": v(29.37, 64.97) * mm});
            skArc(sketch, "E9.7.56.0", {"start": v(28.63, 65.3) * mm, "mid": v(27.08, 64.06) * mm, "end": v(26.03, 62.4) * mm});
            skLineSegment(sketch, "E9.11.56.0", {"start": v(26.13, 62.62) * mm, "end": v(25.42, 61.02) * mm});
            skLineSegment(sketch, "E9.14.56.0", {"start": v(28.34, 59.72) * mm, "end": v(29.05, 61.32) * mm});
            skLineSegment(sketch, "E9.1.57.0", {"start": v(21.64, 67.94) * mm, "end": v(22.42, 67.68) * mm});
            skArc(sketch, "E9.3.57.0", {"start": v(22.4, 63.78) * mm, "mid": v(22.74, 65.73) * mm, "end": v(22.42, 67.68) * mm});
            skArc(sketch, "E9.7.57.0", {"start": v(21.64, 67.94) * mm, "mid": v(20.24, 66.54) * mm, "end": v(19.36, 64.77) * mm});
            skLineSegment(sketch, "E9.11.57.0", {"start": v(19.44, 65) * mm, "end": v(18.9, 63.34) * mm});
            skLineSegment(sketch, "E9.14.57.0", {"start": v(21.94, 62.35) * mm, "end": v(22.48, 64.02) * mm});
            skLineSegment(sketch, "E9.1.58.0", {"start": v(14.43, 69.83) * mm, "end": v(15.22, 69.66) * mm});
            skArc(sketch, "E9.3.58.0", {"start": v(15.62, 65.77) * mm, "mid": v(15.74, 67.75) * mm, "end": v(15.22, 69.66) * mm});
            skArc(sketch, "E9.7.58.0", {"start": v(14.43, 69.83) * mm, "mid": v(13.17, 68.3) * mm, "end": v(12.49, 66.44) * mm});
            skLineSegment(sketch, "E9.11.58.0", {"start": v(12.54, 66.68) * mm, "end": v(12.17, 64.97) * mm});
            skLineSegment(sketch, "E9.14.58.0", {"start": v(15.3, 64.3) * mm, "end": v(15.67, 66.02) * mm});
            skLineSegment(sketch, "E9.1.59.0", {"start": v(7.05, 70.95) * mm, "end": v(7.86, 70.87) * mm});
            skArc(sketch, "E9.3.59.0", {"start": v(8.66, 67.05) * mm, "mid": v(8.58, 69.02) * mm, "end": v(7.86, 70.87) * mm});
            skArc(sketch, "E9.7.59.0", {"start": v(7.05, 70.95) * mm, "mid": v(5.96, 69.3) * mm, "end": v(5.47, 67.38) * mm});
            skLineSegment(sketch, "E9.11.59.0", {"start": v(5.5, 67.63) * mm, "end": v(5.32, 65.89) * mm});
            skLineSegment(sketch, "E9.14.59.0", {"start": v(8.5, 65.55) * mm, "end": v(8.68, 67.3) * mm});
            skSolve(sketch);
        }
        {
            var Q0;
            Q0=qSketchRegion(id+"F0",true);
            extrude(context, id + "F1", {"entities" : qUnion([Q0]), "depth" : 10 * mm, "offsetDistance" : 25 * mm});
        }
        {
            var Q0;
            Q0=makeQuery(id+"F1.opExtrude","CAP_FACE",FACE,{"disambiguationData":[OSD([sQuery(id+"F0.wireOp",EDGE,"E0"),sQuery(id+"F0.wireOp",EDGE,"E1"),sQuery(id+"F0.wireOp",EDGE,"E3"),sQuery(id+"F0.wireOp",EDGE,"E4"),sQuery(id+"F0.wireOp",EDGE,"E5"),sQuery(id+"F0.wireOp",EDGE,"E6.trimOffspring"),sQuery(id+"F0.wireOp",EDGE,"E7"),sQuery(id+"F0.wireOp",EDGE,"E8.1.0"),sQuery(id+"F0.wireOp",EDGE,"E8.1.1"),sQuery(id+"F0.wireOp",EDGE,"E8.1.2"),sQuery(id+"F0.wireOp",EDGE,"E8.1.3"),sQuery(id+"F0.wireOp",EDGE,"E8.1.4"),sQuery(id+"F0.wireOp",EDGE,"E8.2.0"),sQuery(id+"F0.wireOp",EDGE,"E8.2.1"),sQuery(id+"F0.wireOp",EDGE,"E8.2.2"),sQuery(id+"F0.wireOp",EDGE,"E8.2.3"),sQuery(id+"F0.wireOp",EDGE,"E8.2.4"),sQuery(id+"F0.wireOp",EDGE,"E9.1.3.0"),sQuery(id+"F0.wireOp",EDGE,"E9.3.3.0"),sQuery(id+"F0.wireOp",EDGE,"E9.7.3.0"),sQuery(id+"F0.wireOp",EDGE,"E9.11.3.0"),sQuery(id+"F0.wireOp",EDGE,"E9.14.3.0"),sQuery(id+"F0.wireOp",EDGE,"E9.1.4.0"),sQuery(id+"F0.wireOp",EDGE,"E9.3.4.0"),sQuery(id+"F0.wireOp",EDGE,"E9.7.4.0"),sQuery(id+"F0.wireOp",EDGE,"E9.11.4.0"),sQuery(id+"F0.wireOp",EDGE,"E9.14.4.0"),sQuery(id+"F0.wireOp",EDGE,"E9.1.5.0"),sQuery(id+"F0.wireOp",EDGE,"E9.3.5.0"),sQuery(id+"F0.wireOp",EDGE,"E9.7.5.0"),sQuery(id+"F0.wireOp",EDGE,"E9.11.5.0"),sQuery(id+"F0.wireOp",EDGE,"E9.14.5.0"),sQuery(id+"F0.wireOp",EDGE,"E9.1.6.0"),sQuery(id+"F0.wireOp",EDGE,"E9.3.6.0"),sQuery(id+"F0.wireOp",EDGE,"E9.7.6.0"),sQuery(id+"F0.wireOp",EDGE,"E9.11.6.0"),sQuery(id+"F0.wireOp",EDGE,"E9.14.6.0"),sQuery(id+"F0.wireOp",EDGE,"E9.1.7.0"),sQuery(id+"F0.wireOp",EDGE,"E9.3.7.0"),sQuery(id+"F0.wireOp",EDGE,"E9.7.7.0"),sQuery(id+"F0.wireOp",EDGE,"E9.11.7.0"),sQuery(id+"F0.wireOp",EDGE,"E9.14.7.0"),sQuery(id+"F0.wireOp",EDGE,"E9.1.8.0"),sQuery(id+"F0.wireOp",EDGE,"E9.3.8.0"),sQuery(id+"F0.wireOp",EDGE,"E9.7.8.0"),sQuery(id+"F0.wireOp",EDGE,"E9.11.8.0"),sQuery(id+"F0.wireOp",EDGE,"E9.14.8.0"),sQuery(id+"F0.wireOp",EDGE,"E9.1.9.0"),sQuery(id+"F0.wireOp",EDGE,"E9.3.9.0"),sQuery(id+"F0.wireOp",EDGE,"E9.7.9.0"),sQuery(id+"F0.wireOp",EDGE,"E9.11.9.0"),sQuery(id+"F0.wireOp",EDGE,"E9.14.9.0"),sQuery(id+"F0.wireOp",EDGE,"E9.1.10.0"),sQuery(id+"F0.wireOp",EDGE,"E9.3.10.0"),sQuery(id+"F0.wireOp",EDGE,"E9.7.10.0"),sQuery(id+"F0.wireOp",EDGE,"E9.11.10.0"),sQuery(id+"F0.wireOp",EDGE,"E9.14.10.0"),sQuery(id+"F0.wireOp",EDGE,"E9.1.11.0"),sQuery(id+"F0.wireOp",EDGE,"E9.3.11.0"),sQuery(id+"F0.wireOp",EDGE,"E9.7.11.0"),sQuery(id+"F0.wireOp",EDGE,"E9.11.11.0"),sQuery(id+"F0.wireOp",EDGE,"E9.14.11.0"),sQuery(id+"F0.wireOp",EDGE,"E9.1.12.0"),sQuery(id+"F0.wireOp",EDGE,"E9.3.12.0"),sQuery(id+"F0.wireOp",EDGE,"E9.7.12.0"),sQuery(id+"F0.wireOp",EDGE,"E9.11.12.0"),sQuery(id+"F0.wireOp",EDGE,"E9.14.12.0"),sQuery(id+"F0.wireOp",EDGE,"E9.1.13.0"),sQuery(id+"F0.wireOp",EDGE,"E9.3.13.0"),sQuery(id+"F0.wireOp",EDGE,"E9.7.13.0"),sQuery(id+"F0.wireOp",EDGE,"E9.11.13.0"),sQuery(id+"F0.wireOp",EDGE,"E9.14.13.0"),sQuery(id+"F0.wireOp",EDGE,"E9.1.14.0"),sQuery(id+"F0.wireOp",EDGE,"E9.3.14.0"),sQuery(id+"F0.wireOp",EDGE,"E9.7.14.0"),sQuery(id+"F0.wireOp",EDGE,"E9.11.14.0"),sQuery(id+"F0.wireOp",EDGE,"E9.14.14.0"),sQuery(id+"F0.wireOp",EDGE,"E9.1.15.0"),sQuery(id+"F0.wireOp",EDGE,"E9.3.15.0"),sQuery(id+"F0.wireOp",EDGE,"E9.7.15.0"),sQuery(id+"F0.wireOp",EDGE,"E9.11.15.0"),sQuery(id+"F0.wireOp",EDGE,"E9.14.15.0"),sQuery(id+"F0.wireOp",EDGE,"E9.1.16.0"),sQuery(id+"F0.wireOp",EDGE,"E9.3.16.0"),sQuery(id+"F0.wireOp",EDGE,"E9.7.16.0"),sQuery(id+"F0.wireOp",EDGE,"E9.11.16.0"),sQuery(id+"F0.wireOp",EDGE,"E9.14.16.0"),sQuery(id+"F0.wireOp",EDGE,"E9.1.17.0"),sQuery(id+"F0.wireOp",EDGE,"E9.3.17.0"),sQuery(id+"F0.wireOp",EDGE,"E9.7.17.0"),sQuery(id+"F0.wireOp",EDGE,"E9.11.17.0"),sQuery(id+"F0.wireOp",EDGE,"E9.14.17.0"),sQuery(id+"F0.wireOp",EDGE,"E9.1.18.0"),sQuery(id+"F0.wireOp",EDGE,"E9.3.18.0"),sQuery(id+"F0.wireOp",EDGE,"E9.7.18.0"),sQuery(id+"F0.wireOp",EDGE,"E9.11.18.0"),sQuery(id+"F0.wireOp",EDGE,"E9.14.18.0"),sQuery(id+"F0.wireOp",EDGE,"E9.1.19.0"),sQuery(id+"F0.wireOp",EDGE,"E9.3.19.0"),sQuery(id+"F0.wireOp",EDGE,"E9.7.19.0"),sQuery(id+"F0.wireOp",EDGE,"E9.11.19.0"),sQuery(id+"F0.wireOp",EDGE,"E9.14.19.0"),sQuery(id+"F0.wireOp",EDGE,"E9.1.20.0"),sQuery(id+"F0.wireOp",EDGE,"E9.3.20.0"),sQuery(id+"F0.wireOp",EDGE,"E9.7.20.0"),sQuery(id+"F0.wireOp",EDGE,"E9.11.20.0"),sQuery(id+"F0.wireOp",EDGE,"E9.14.20.0"),sQuery(id+"F0.wireOp",EDGE,"E9.1.21.0"),sQuery(id+"F0.wireOp",EDGE,"E9.3.21.0"),sQuery(id+"F0.wireOp",EDGE,"E9.7.21.0"),sQuery(id+"F0.wireOp",EDGE,"E9.11.21.0"),sQuery(id+"F0.wireOp",EDGE,"E9.14.21.0"),sQuery(id+"F0.wireOp",EDGE,"E9.1.22.0"),sQuery(id+"F0.wireOp",EDGE,"E9.3.22.0"),sQuery(id+"F0.wireOp",EDGE,"E9.7.22.0"),sQuery(id+"F0.wireOp",EDGE,"E9.11.22.0"),sQuery(id+"F0.wireOp",EDGE,"E9.14.22.0"),sQuery(id+"F0.wireOp",EDGE,"E9.1.23.0"),sQuery(id+"F0.wireOp",EDGE,"E9.3.23.0"),sQuery(id+"F0.wireOp",EDGE,"E9.7.23.0"),sQuery(id+"F0.wireOp",EDGE,"E9.11.23.0"),sQuery(id+"F0.wireOp",EDGE,"E9.14.23.0"),sQuery(id+"F0.wireOp",EDGE,"E9.1.24.0"),sQuery(id+"F0.wireOp",EDGE,"E9.3.24.0"),sQuery(id+"F0.wireOp",EDGE,"E9.7.24.0"),sQuery(id+"F0.wireOp",EDGE,"E9.11.24.0"),sQuery(id+"F0.wireOp",EDGE,"E9.14.24.0"),sQuery(id+"F0.wireOp",EDGE,"E9.1.25.0"),sQuery(id+"F0.wireOp",EDGE,"E9.3.25.0"),sQuery(id+"F0.wireOp",EDGE,"E9.7.25.0"),sQuery(id+"F0.wireOp",EDGE,"E9.11.25.0"),sQuery(id+"F0.wireOp",EDGE,"E9.14.25.0"),sQuery(id+"F0.wireOp",EDGE,"E9.1.26.0"),sQuery(id+"F0.wireOp",EDGE,"E9.3.26.0"),sQuery(id+"F0.wireOp",EDGE,"E9.7.26.0"),sQuery(id+"F0.wireOp",EDGE,"E9.11.26.0"),sQuery(id+"F0.wireOp",EDGE,"E9.14.26.0"),sQuery(id+"F0.wireOp",EDGE,"E9.1.27.0"),sQuery(id+"F0.wireOp",EDGE,"E9.3.27.0"),sQuery(id+"F0.wireOp",EDGE,"E9.7.27.0"),sQuery(id+"F0.wireOp",EDGE,"E9.11.27.0"),sQuery(id+"F0.wireOp",EDGE,"E9.14.27.0"),sQuery(id+"F0.wireOp",EDGE,"E9.1.28.0"),sQuery(id+"F0.wireOp",EDGE,"E9.3.28.0"),sQuery(id+"F0.wireOp",EDGE,"E9.7.28.0"),sQuery(id+"F0.wireOp",EDGE,"E9.11.28.0"),sQuery(id+"F0.wireOp",EDGE,"E9.14.28.0"),sQuery(id+"F0.wireOp",EDGE,"E9.1.29.0"),sQuery(id+"F0.wireOp",EDGE,"E9.3.29.0"),sQuery(id+"F0.wireOp",EDGE,"E9.7.29.0"),sQuery(id+"F0.wireOp",EDGE,"E9.11.29.0"),sQuery(id+"F0.wireOp",EDGE,"E9.14.29.0"),sQuery(id+"F0.wireOp",EDGE,"E9.1.30.0"),sQuery(id+"F0.wireOp",EDGE,"E9.3.30.0"),sQuery(id+"F0.wireOp",EDGE,"E9.7.30.0"),sQuery(id+"F0.wireOp",EDGE,"E9.11.30.0"),sQuery(id+"F0.wireOp",EDGE,"E9.14.30.0"),sQuery(id+"F0.wireOp",EDGE,"E9.1.31.0"),sQuery(id+"F0.wireOp",EDGE,"E9.3.31.0"),sQuery(id+"F0.wireOp",EDGE,"E9.7.31.0"),sQuery(id+"F0.wireOp",EDGE,"E9.11.31.0"),sQuery(id+"F0.wireOp",EDGE,"E9.14.31.0"),sQuery(id+"F0.wireOp",EDGE,"E9.1.32.0"),sQuery(id+"F0.wireOp",EDGE,"E9.3.32.0"),sQuery(id+"F0.wireOp",EDGE,"E9.7.32.0"),sQuery(id+"F0.wireOp",EDGE,"E9.11.32.0"),sQuery(id+"F0.wireOp",EDGE,"E9.14.32.0"),sQuery(id+"F0.wireOp",EDGE,"E9.1.33.0"),sQuery(id+"F0.wireOp",EDGE,"E9.3.33.0"),sQuery(id+"F0.wireOp",EDGE,"E9.7.33.0"),sQuery(id+"F0.wireOp",EDGE,"E9.11.33.0"),sQuery(id+"F0.wireOp",EDGE,"E9.14.33.0"),sQuery(id+"F0.wireOp",EDGE,"E9.1.34.0"),sQuery(id+"F0.wireOp",EDGE,"E9.3.34.0"),sQuery(id+"F0.wireOp",EDGE,"E9.7.34.0"),sQuery(id+"F0.wireOp",EDGE,"E9.11.34.0"),sQuery(id+"F0.wireOp",EDGE,"E9.14.34.0"),sQuery(id+"F0.wireOp",EDGE,"E9.1.35.0"),sQuery(id+"F0.wireOp",EDGE,"E9.3.35.0"),sQuery(id+"F0.wireOp",EDGE,"E9.7.35.0"),sQuery(id+"F0.wireOp",EDGE,"E9.11.35.0"),sQuery(id+"F0.wireOp",EDGE,"E9.14.35.0"),sQuery(id+"F0.wireOp",EDGE,"E9.1.36.0"),sQuery(id+"F0.wireOp",EDGE,"E9.3.36.0"),sQuery(id+"F0.wireOp",EDGE,"E9.7.36.0"),sQuery(id+"F0.wireOp",EDGE,"E9.11.36.0"),sQuery(id+"F0.wireOp",EDGE,"E9.14.36.0"),sQuery(id+"F0.wireOp",EDGE,"E9.1.37.0"),sQuery(id+"F0.wireOp",EDGE,"E9.3.37.0"),sQuery(id+"F0.wireOp",EDGE,"E9.7.37.0"),sQuery(id+"F0.wireOp",EDGE,"E9.11.37.0"),sQuery(id+"F0.wireOp",EDGE,"E9.14.37.0"),sQuery(id+"F0.wireOp",EDGE,"E9.1.38.0"),sQuery(id+"F0.wireOp",EDGE,"E9.3.38.0"),sQuery(id+"F0.wireOp",EDGE,"E9.7.38.0"),sQuery(id+"F0.wireOp",EDGE,"E9.11.38.0"),sQuery(id+"F0.wireOp",EDGE,"E9.14.38.0"),sQuery(id+"F0.wireOp",EDGE,"E9.1.39.0"),sQuery(id+"F0.wireOp",EDGE,"E9.3.39.0"),sQuery(id+"F0.wireOp",EDGE,"E9.7.39.0"),sQuery(id+"F0.wireOp",EDGE,"E9.11.39.0"),sQuery(id+"F0.wireOp",EDGE,"E9.14.39.0"),sQuery(id+"F0.wireOp",EDGE,"E9.1.40.0"),sQuery(id+"F0.wireOp",EDGE,"E9.3.40.0"),sQuery(id+"F0.wireOp",EDGE,"E9.7.40.0"),sQuery(id+"F0.wireOp",EDGE,"E9.11.40.0"),sQuery(id+"F0.wireOp",EDGE,"E9.14.40.0"),sQuery(id+"F0.wireOp",EDGE,"E9.1.41.0"),sQuery(id+"F0.wireOp",EDGE,"E9.3.41.0"),sQuery(id+"F0.wireOp",EDGE,"E9.7.41.0"),sQuery(id+"F0.wireOp",EDGE,"E9.11.41.0"),sQuery(id+"F0.wireOp",EDGE,"E9.14.41.0"),sQuery(id+"F0.wireOp",EDGE,"E9.1.42.0"),sQuery(id+"F0.wireOp",EDGE,"E9.3.42.0"),sQuery(id+"F0.wireOp",EDGE,"E9.7.42.0"),sQuery(id+"F0.wireOp",EDGE,"E9.11.42.0"),sQuery(id+"F0.wireOp",EDGE,"E9.14.42.0"),sQuery(id+"F0.wireOp",EDGE,"E9.1.43.0"),sQuery(id+"F0.wireOp",EDGE,"E9.3.43.0"),sQuery(id+"F0.wireOp",EDGE,"E9.7.43.0"),sQuery(id+"F0.wireOp",EDGE,"E9.11.43.0"),sQuery(id+"F0.wireOp",EDGE,"E9.14.43.0"),sQuery(id+"F0.wireOp",EDGE,"E9.1.44.0"),sQuery(id+"F0.wireOp",EDGE,"E9.3.44.0"),sQuery(id+"F0.wireOp",EDGE,"E9.7.44.0"),sQuery(id+"F0.wireOp",EDGE,"E9.11.44.0"),sQuery(id+"F0.wireOp",EDGE,"E9.14.44.0"),sQuery(id+"F0.wireOp",EDGE,"E9.1.45.0"),sQuery(id+"F0.wireOp",EDGE,"E9.3.45.0"),sQuery(id+"F0.wireOp",EDGE,"E9.7.45.0"),sQuery(id+"F0.wireOp",EDGE,"E9.11.45.0"),sQuery(id+"F0.wireOp",EDGE,"E9.14.45.0"),sQuery(id+"F0.wireOp",EDGE,"E9.1.46.0"),sQuery(id+"F0.wireOp",EDGE,"E9.3.46.0"),sQuery(id+"F0.wireOp",EDGE,"E9.7.46.0"),sQuery(id+"F0.wireOp",EDGE,"E9.11.46.0"),sQuery(id+"F0.wireOp",EDGE,"E9.14.46.0"),sQuery(id+"F0.wireOp",EDGE,"E9.1.47.0"),sQuery(id+"F0.wireOp",EDGE,"E9.3.47.0"),sQuery(id+"F0.wireOp",EDGE,"E9.7.47.0"),sQuery(id+"F0.wireOp",EDGE,"E9.11.47.0"),sQuery(id+"F0.wireOp",EDGE,"E9.14.47.0"),sQuery(id+"F0.wireOp",EDGE,"E9.1.48.0"),sQuery(id+"F0.wireOp",EDGE,"E9.3.48.0"),sQuery(id+"F0.wireOp",EDGE,"E9.7.48.0"),sQuery(id+"F0.wireOp",EDGE,"E9.11.48.0"),sQuery(id+"F0.wireOp",EDGE,"E9.14.48.0"),sQuery(id+"F0.wireOp",EDGE,"E9.1.49.0"),sQuery(id+"F0.wireOp",EDGE,"E9.3.49.0"),sQuery(id+"F0.wireOp",EDGE,"E9.7.49.0"),sQuery(id+"F0.wireOp",EDGE,"E9.11.49.0"),sQuery(id+"F0.wireOp",EDGE,"E9.14.49.0"),sQuery(id+"F0.wireOp",EDGE,"E9.1.50.0"),sQuery(id+"F0.wireOp",EDGE,"E9.3.50.0"),sQuery(id+"F0.wireOp",EDGE,"E9.7.50.0"),sQuery(id+"F0.wireOp",EDGE,"E9.11.50.0"),sQuery(id+"F0.wireOp",EDGE,"E9.14.50.0"),sQuery(id+"F0.wireOp",EDGE,"E9.1.51.0"),sQuery(id+"F0.wireOp",EDGE,"E9.3.51.0"),sQuery(id+"F0.wireOp",EDGE,"E9.7.51.0"),sQuery(id+"F0.wireOp",EDGE,"E9.11.51.0"),sQuery(id+"F0.wireOp",EDGE,"E9.14.51.0"),sQuery(id+"F0.wireOp",EDGE,"E9.1.52.0"),sQuery(id+"F0.wireOp",EDGE,"E9.3.52.0"),sQuery(id+"F0.wireOp",EDGE,"E9.7.52.0"),sQuery(id+"F0.wireOp",EDGE,"E9.11.52.0"),sQuery(id+"F0.wireOp",EDGE,"E9.14.52.0"),sQuery(id+"F0.wireOp",EDGE,"E9.1.53.0"),sQuery(id+"F0.wireOp",EDGE,"E9.3.53.0"),sQuery(id+"F0.wireOp",EDGE,"E9.7.53.0"),sQuery(id+"F0.wireOp",EDGE,"E9.11.53.0"),sQuery(id+"F0.wireOp",EDGE,"E9.14.53.0"),sQuery(id+"F0.wireOp",EDGE,"E9.1.54.0"),sQuery(id+"F0.wireOp",EDGE,"E9.3.54.0"),sQuery(id+"F0.wireOp",EDGE,"E9.7.54.0"),sQuery(id+"F0.wireOp",EDGE,"E9.11.54.0"),sQuery(id+"F0.wireOp",EDGE,"E9.14.54.0"),sQuery(id+"F0.wireOp",EDGE,"E9.1.55.0"),sQuery(id+"F0.wireOp",EDGE,"E9.3.55.0"),sQuery(id+"F0.wireOp",EDGE,"E9.7.55.0"),sQuery(id+"F0.wireOp",EDGE,"E9.11.55.0"),sQuery(id+"F0.wireOp",EDGE,"E9.14.55.0"),sQuery(id+"F0.wireOp",EDGE,"E9.1.56.0"),sQuery(id+"F0.wireOp",EDGE,"E9.3.56.0"),sQuery(id+"F0.wireOp",EDGE,"E9.7.56.0"),sQuery(id+"F0.wireOp",EDGE,"E9.11.56.0"),sQuery(id+"F0.wireOp",EDGE,"E9.14.56.0"),sQuery(id+"F0.wireOp",EDGE,"E9.1.57.0"),sQuery(id+"F0.wireOp",EDGE,"E9.3.57.0"),sQuery(id+"F0.wireOp",EDGE,"E9.7.57.0"),sQuery(id+"F0.wireOp",EDGE,"E9.11.57.0"),sQuery(id+"F0.wireOp",EDGE,"E9.14.57.0"),sQuery(id+"F0.wireOp",EDGE,"E9.1.58.0"),sQuery(id+"F0.wireOp",EDGE,"E9.3.58.0"),sQuery(id+"F0.wireOp",EDGE,"E9.7.58.0"),sQuery(id+"F0.wireOp",EDGE,"E9.11.58.0"),sQuery(id+"F0.wireOp",EDGE,"E9.14.58.0"),sQuery(id+"F0.wireOp",EDGE,"E9.1.59.0"),sQuery(id+"F0.wireOp",EDGE,"E9.3.59.0"),sQuery(id+"F0.wireOp",EDGE,"E9.7.59.0"),sQuery(id+"F0.wireOp",EDGE,"E9.11.59.0"),sQuery(id+"F0.wireOp",EDGE,"E9.14.59.0")])],"isStart":false});
            var sketch = newSketch(context, id + "F2", { "sketchPlane" : qUnion([Q0])});
            skCircle(sketch, "E10", {"center": v(0, 0) * mm, "radius": 64 * mm});
            skCircle(sketch, "E11", {"center": v(0, 0) * mm, "radius": 63 * mm});
            skCircle(sketch, "E12", {"center": v(0, 0) * mm, "radius": 60 * mm});
            skCircle(sketch, "E13", {"center": v(0, 0) * mm, "radius": 59 * mm});
            skCircle(sketch, "E14", {"center": v(0, 0) * mm, "radius": 10 * mm});
            skCircle(sketch, "E15", {"center": v(0, 0) * mm, "radius": 58 * mm});
            skCircle(sketch, "E16", {"center": v(0, 0) * mm, "radius": 11 * mm});
            skLineSegment(sketch, "E17", {"start": v(0, -58) * mm, "end": v(0, 58) * mm, "construction": true});
            skLineSegment(sketch, "E18", {"start": v(58, 0) * mm, "end": v(-58, 0) * mm, "construction": true});
            skLineSegment(sketch, "E19", {"start": v(-46.28, 5) * mm, "end": v(-14.5, 5) * mm});
            skLineSegment(sketch, "E20.0", {"start": v(-46.28, -5) * mm, "end": v(-14.5, -5) * mm});
            skLineSegment(sketch, "E21", {"start": v(-5, -46.28) * mm, "end": v(-5, -14.5) * mm});
            skLineSegment(sketch, "E22.0", {"start": v(5, -46.28) * mm, "end": v(5, -14.5) * mm});
            skArc(sketch, "E23", {"start": v(5, 14.5) * mm, "mid": v(7.78, 7.78) * mm, "end": v(14.5, 5) * mm});
            skArc(sketch, "E24", {"start": v(-14.5, 5) * mm, "mid": v(-7.78, 7.78) * mm, "end": v(-5, 14.5) * mm});
            skArc(sketch, "E25", {"start": v(-5, -14.5) * mm, "mid": v(-7.78, -7.78) * mm, "end": v(-14.5, -5) * mm});
            skArc(sketch, "E26", {"start": v(14.5, -5) * mm, "mid": v(7.78, -7.78) * mm, "end": v(5, -14.5) * mm});
            skArc(sketch, "E27", {"start": v(46.28, 5) * mm, "mid": v(53.94, 8.88) * mm, "end": v(55.35, 17.34) * mm});
            skArc(sketch, "E28", {"start": v(17.34, 55.35) * mm, "mid": v(8.88, 53.94) * mm, "end": v(5, 46.28) * mm});
            skArc(sketch, "E29", {"start": v(-5, 46.28) * mm, "mid": v(-8.88, 53.94) * mm, "end": v(-17.34, 55.35) * mm});
            skArc(sketch, "E30", {"start": v(-55.35, 17.34) * mm, "mid": v(-53.94, 8.88) * mm, "end": v(-46.28, 5) * mm});
            skArc(sketch, "E31", {"start": v(-46.28, -5) * mm, "mid": v(-53.94, -8.88) * mm, "end": v(-55.35, -17.34) * mm});
            skArc(sketch, "E32", {"start": v(-17.34, -55.35) * mm, "mid": v(-8.88, -53.94) * mm, "end": v(-5, -46.28) * mm});
            skArc(sketch, "E33", {"start": v(5, -46.28) * mm, "mid": v(8.88, -53.94) * mm, "end": v(17.34, -55.35) * mm});
            skArc(sketch, "E34", {"start": v(55.35, -17.34) * mm, "mid": v(53.94, -8.88) * mm, "end": v(46.28, -5) * mm});
            skLineSegment(sketch, "E35.trimOffspring", {"start": v(-5, 14.5) * mm, "end": v(-5, 46.28) * mm});
            skLineSegment(sketch, "E36.trimOffspring", {"start": v(14.5, 5) * mm, "end": v(46.28, 5) * mm});
            skLineSegment(sketch, "E37.trimOffspring", {"start": v(5, 14.5) * mm, "end": v(5, 46.28) * mm});
            skLineSegment(sketch, "E38.trimOffspring", {"start": v(14.5, -5) * mm, "end": v(46.28, -5) * mm});
            skSolve(sketch);
        }
        {
            var Q0;
            Q0=makeQuery(id+"F1.opExtrude","CAP_FACE",FACE,{"disambiguationData":[OSD([sQuery(id+"F0.wireOp",EDGE,"E0"),sQuery(id+"F0.wireOp",EDGE,"E1"),sQuery(id+"F0.wireOp",EDGE,"E3"),sQuery(id+"F0.wireOp",EDGE,"E4"),sQuery(id+"F0.wireOp",EDGE,"E5"),sQuery(id+"F0.wireOp",EDGE,"E6.trimOffspring"),sQuery(id+"F0.wireOp",EDGE,"E7"),sQuery(id+"F0.wireOp",EDGE,"E8.1.0"),sQuery(id+"F0.wireOp",EDGE,"E8.1.1"),sQuery(id+"F0.wireOp",EDGE,"E8.1.2"),sQuery(id+"F0.wireOp",EDGE,"E8.1.3"),sQuery(id+"F0.wireOp",EDGE,"E8.1.4"),sQuery(id+"F0.wireOp",EDGE,"E8.2.0"),sQuery(id+"F0.wireOp",EDGE,"E8.2.1"),sQuery(id+"F0.wireOp",EDGE,"E8.2.2"),sQuery(id+"F0.wireOp",EDGE,"E8.2.3"),sQuery(id+"F0.wireOp",EDGE,"E8.2.4"),sQuery(id+"F0.wireOp",EDGE,"E9.1.3.0"),sQuery(id+"F0.wireOp",EDGE,"E9.3.3.0"),sQuery(id+"F0.wireOp",EDGE,"E9.7.3.0"),sQuery(id+"F0.wireOp",EDGE,"E9.11.3.0"),sQuery(id+"F0.wireOp",EDGE,"E9.14.3.0"),sQuery(id+"F0.wireOp",EDGE,"E9.1.4.0"),sQuery(id+"F0.wireOp",EDGE,"E9.3.4.0"),sQuery(id+"F0.wireOp",EDGE,"E9.7.4.0"),sQuery(id+"F0.wireOp",EDGE,"E9.11.4.0"),sQuery(id+"F0.wireOp",EDGE,"E9.14.4.0"),sQuery(id+"F0.wireOp",EDGE,"E9.1.5.0"),sQuery(id+"F0.wireOp",EDGE,"E9.3.5.0"),sQuery(id+"F0.wireOp",EDGE,"E9.7.5.0"),sQuery(id+"F0.wireOp",EDGE,"E9.11.5.0"),sQuery(id+"F0.wireOp",EDGE,"E9.14.5.0"),sQuery(id+"F0.wireOp",EDGE,"E9.1.6.0"),sQuery(id+"F0.wireOp",EDGE,"E9.3.6.0"),sQuery(id+"F0.wireOp",EDGE,"E9.7.6.0"),sQuery(id+"F0.wireOp",EDGE,"E9.11.6.0"),sQuery(id+"F0.wireOp",EDGE,"E9.14.6.0"),sQuery(id+"F0.wireOp",EDGE,"E9.1.7.0"),sQuery(id+"F0.wireOp",EDGE,"E9.3.7.0"),sQuery(id+"F0.wireOp",EDGE,"E9.7.7.0"),sQuery(id+"F0.wireOp",EDGE,"E9.11.7.0"),sQuery(id+"F0.wireOp",EDGE,"E9.14.7.0"),sQuery(id+"F0.wireOp",EDGE,"E9.1.8.0"),sQuery(id+"F0.wireOp",EDGE,"E9.3.8.0"),sQuery(id+"F0.wireOp",EDGE,"E9.7.8.0"),sQuery(id+"F0.wireOp",EDGE,"E9.11.8.0"),sQuery(id+"F0.wireOp",EDGE,"E9.14.8.0"),sQuery(id+"F0.wireOp",EDGE,"E9.1.9.0"),sQuery(id+"F0.wireOp",EDGE,"E9.3.9.0"),sQuery(id+"F0.wireOp",EDGE,"E9.7.9.0"),sQuery(id+"F0.wireOp",EDGE,"E9.11.9.0"),sQuery(id+"F0.wireOp",EDGE,"E9.14.9.0"),sQuery(id+"F0.wireOp",EDGE,"E9.1.10.0"),sQuery(id+"F0.wireOp",EDGE,"E9.3.10.0"),sQuery(id+"F0.wireOp",EDGE,"E9.7.10.0"),sQuery(id+"F0.wireOp",EDGE,"E9.11.10.0"),sQuery(id+"F0.wireOp",EDGE,"E9.14.10.0"),sQuery(id+"F0.wireOp",EDGE,"E9.1.11.0"),sQuery(id+"F0.wireOp",EDGE,"E9.3.11.0"),sQuery(id+"F0.wireOp",EDGE,"E9.7.11.0"),sQuery(id+"F0.wireOp",EDGE,"E9.11.11.0"),sQuery(id+"F0.wireOp",EDGE,"E9.14.11.0"),sQuery(id+"F0.wireOp",EDGE,"E9.1.12.0"),sQuery(id+"F0.wireOp",EDGE,"E9.3.12.0"),sQuery(id+"F0.wireOp",EDGE,"E9.7.12.0"),sQuery(id+"F0.wireOp",EDGE,"E9.11.12.0"),sQuery(id+"F0.wireOp",EDGE,"E9.14.12.0"),sQuery(id+"F0.wireOp",EDGE,"E9.1.13.0"),sQuery(id+"F0.wireOp",EDGE,"E9.3.13.0"),sQuery(id+"F0.wireOp",EDGE,"E9.7.13.0"),sQuery(id+"F0.wireOp",EDGE,"E9.11.13.0"),sQuery(id+"F0.wireOp",EDGE,"E9.14.13.0"),sQuery(id+"F0.wireOp",EDGE,"E9.1.14.0"),sQuery(id+"F0.wireOp",EDGE,"E9.3.14.0"),sQuery(id+"F0.wireOp",EDGE,"E9.7.14.0"),sQuery(id+"F0.wireOp",EDGE,"E9.11.14.0"),sQuery(id+"F0.wireOp",EDGE,"E9.14.14.0"),sQuery(id+"F0.wireOp",EDGE,"E9.1.15.0"),sQuery(id+"F0.wireOp",EDGE,"E9.3.15.0"),sQuery(id+"F0.wireOp",EDGE,"E9.7.15.0"),sQuery(id+"F0.wireOp",EDGE,"E9.11.15.0"),sQuery(id+"F0.wireOp",EDGE,"E9.14.15.0"),sQuery(id+"F0.wireOp",EDGE,"E9.1.16.0"),sQuery(id+"F0.wireOp",EDGE,"E9.3.16.0"),sQuery(id+"F0.wireOp",EDGE,"E9.7.16.0"),sQuery(id+"F0.wireOp",EDGE,"E9.11.16.0"),sQuery(id+"F0.wireOp",EDGE,"E9.14.16.0"),sQuery(id+"F0.wireOp",EDGE,"E9.1.17.0"),sQuery(id+"F0.wireOp",EDGE,"E9.3.17.0"),sQuery(id+"F0.wireOp",EDGE,"E9.7.17.0"),sQuery(id+"F0.wireOp",EDGE,"E9.11.17.0"),sQuery(id+"F0.wireOp",EDGE,"E9.14.17.0"),sQuery(id+"F0.wireOp",EDGE,"E9.1.18.0"),sQuery(id+"F0.wireOp",EDGE,"E9.3.18.0"),sQuery(id+"F0.wireOp",EDGE,"E9.7.18.0"),sQuery(id+"F0.wireOp",EDGE,"E9.11.18.0"),sQuery(id+"F0.wireOp",EDGE,"E9.14.18.0"),sQuery(id+"F0.wireOp",EDGE,"E9.1.19.0"),sQuery(id+"F0.wireOp",EDGE,"E9.3.19.0"),sQuery(id+"F0.wireOp",EDGE,"E9.7.19.0"),sQuery(id+"F0.wireOp",EDGE,"E9.11.19.0"),sQuery(id+"F0.wireOp",EDGE,"E9.14.19.0"),sQuery(id+"F0.wireOp",EDGE,"E9.1.20.0"),sQuery(id+"F0.wireOp",EDGE,"E9.3.20.0"),sQuery(id+"F0.wireOp",EDGE,"E9.7.20.0"),sQuery(id+"F0.wireOp",EDGE,"E9.11.20.0"),sQuery(id+"F0.wireOp",EDGE,"E9.14.20.0"),sQuery(id+"F0.wireOp",EDGE,"E9.1.21.0"),sQuery(id+"F0.wireOp",EDGE,"E9.3.21.0"),sQuery(id+"F0.wireOp",EDGE,"E9.7.21.0"),sQuery(id+"F0.wireOp",EDGE,"E9.11.21.0"),sQuery(id+"F0.wireOp",EDGE,"E9.14.21.0"),sQuery(id+"F0.wireOp",EDGE,"E9.1.22.0"),sQuery(id+"F0.wireOp",EDGE,"E9.3.22.0"),sQuery(id+"F0.wireOp",EDGE,"E9.7.22.0"),sQuery(id+"F0.wireOp",EDGE,"E9.11.22.0"),sQuery(id+"F0.wireOp",EDGE,"E9.14.22.0"),sQuery(id+"F0.wireOp",EDGE,"E9.1.23.0"),sQuery(id+"F0.wireOp",EDGE,"E9.3.23.0"),sQuery(id+"F0.wireOp",EDGE,"E9.7.23.0"),sQuery(id+"F0.wireOp",EDGE,"E9.11.23.0"),sQuery(id+"F0.wireOp",EDGE,"E9.14.23.0"),sQuery(id+"F0.wireOp",EDGE,"E9.1.24.0"),sQuery(id+"F0.wireOp",EDGE,"E9.3.24.0"),sQuery(id+"F0.wireOp",EDGE,"E9.7.24.0"),sQuery(id+"F0.wireOp",EDGE,"E9.11.24.0"),sQuery(id+"F0.wireOp",EDGE,"E9.14.24.0"),sQuery(id+"F0.wireOp",EDGE,"E9.1.25.0"),sQuery(id+"F0.wireOp",EDGE,"E9.3.25.0"),sQuery(id+"F0.wireOp",EDGE,"E9.7.25.0"),sQuery(id+"F0.wireOp",EDGE,"E9.11.25.0"),sQuery(id+"F0.wireOp",EDGE,"E9.14.25.0"),sQuery(id+"F0.wireOp",EDGE,"E9.1.26.0"),sQuery(id+"F0.wireOp",EDGE,"E9.3.26.0"),sQuery(id+"F0.wireOp",EDGE,"E9.7.26.0"),sQuery(id+"F0.wireOp",EDGE,"E9.11.26.0"),sQuery(id+"F0.wireOp",EDGE,"E9.14.26.0"),sQuery(id+"F0.wireOp",EDGE,"E9.1.27.0"),sQuery(id+"F0.wireOp",EDGE,"E9.3.27.0"),sQuery(id+"F0.wireOp",EDGE,"E9.7.27.0"),sQuery(id+"F0.wireOp",EDGE,"E9.11.27.0"),sQuery(id+"F0.wireOp",EDGE,"E9.14.27.0"),sQuery(id+"F0.wireOp",EDGE,"E9.1.28.0"),sQuery(id+"F0.wireOp",EDGE,"E9.3.28.0"),sQuery(id+"F0.wireOp",EDGE,"E9.7.28.0"),sQuery(id+"F0.wireOp",EDGE,"E9.11.28.0"),sQuery(id+"F0.wireOp",EDGE,"E9.14.28.0"),sQuery(id+"F0.wireOp",EDGE,"E9.1.29.0"),sQuery(id+"F0.wireOp",EDGE,"E9.3.29.0"),sQuery(id+"F0.wireOp",EDGE,"E9.7.29.0"),sQuery(id+"F0.wireOp",EDGE,"E9.11.29.0"),sQuery(id+"F0.wireOp",EDGE,"E9.14.29.0"),sQuery(id+"F0.wireOp",EDGE,"E9.1.30.0"),sQuery(id+"F0.wireOp",EDGE,"E9.3.30.0"),sQuery(id+"F0.wireOp",EDGE,"E9.7.30.0"),sQuery(id+"F0.wireOp",EDGE,"E9.11.30.0"),sQuery(id+"F0.wireOp",EDGE,"E9.14.30.0"),sQuery(id+"F0.wireOp",EDGE,"E9.1.31.0"),sQuery(id+"F0.wireOp",EDGE,"E9.3.31.0"),sQuery(id+"F0.wireOp",EDGE,"E9.7.31.0"),sQuery(id+"F0.wireOp",EDGE,"E9.11.31.0"),sQuery(id+"F0.wireOp",EDGE,"E9.14.31.0"),sQuery(id+"F0.wireOp",EDGE,"E9.1.32.0"),sQuery(id+"F0.wireOp",EDGE,"E9.3.32.0"),sQuery(id+"F0.wireOp",EDGE,"E9.7.32.0"),sQuery(id+"F0.wireOp",EDGE,"E9.11.32.0"),sQuery(id+"F0.wireOp",EDGE,"E9.14.32.0"),sQuery(id+"F0.wireOp",EDGE,"E9.1.33.0"),sQuery(id+"F0.wireOp",EDGE,"E9.3.33.0"),sQuery(id+"F0.wireOp",EDGE,"E9.7.33.0"),sQuery(id+"F0.wireOp",EDGE,"E9.11.33.0"),sQuery(id+"F0.wireOp",EDGE,"E9.14.33.0"),sQuery(id+"F0.wireOp",EDGE,"E9.1.34.0"),sQuery(id+"F0.wireOp",EDGE,"E9.3.34.0"),sQuery(id+"F0.wireOp",EDGE,"E9.7.34.0"),sQuery(id+"F0.wireOp",EDGE,"E9.11.34.0"),sQuery(id+"F0.wireOp",EDGE,"E9.14.34.0"),sQuery(id+"F0.wireOp",EDGE,"E9.1.35.0"),sQuery(id+"F0.wireOp",EDGE,"E9.3.35.0"),sQuery(id+"F0.wireOp",EDGE,"E9.7.35.0"),sQuery(id+"F0.wireOp",EDGE,"E9.11.35.0"),sQuery(id+"F0.wireOp",EDGE,"E9.14.35.0"),sQuery(id+"F0.wireOp",EDGE,"E9.1.36.0"),sQuery(id+"F0.wireOp",EDGE,"E9.3.36.0"),sQuery(id+"F0.wireOp",EDGE,"E9.7.36.0"),sQuery(id+"F0.wireOp",EDGE,"E9.11.36.0"),sQuery(id+"F0.wireOp",EDGE,"E9.14.36.0"),sQuery(id+"F0.wireOp",EDGE,"E9.1.37.0"),sQuery(id+"F0.wireOp",EDGE,"E9.3.37.0"),sQuery(id+"F0.wireOp",EDGE,"E9.7.37.0"),sQuery(id+"F0.wireOp",EDGE,"E9.11.37.0"),sQuery(id+"F0.wireOp",EDGE,"E9.14.37.0"),sQuery(id+"F0.wireOp",EDGE,"E9.1.38.0"),sQuery(id+"F0.wireOp",EDGE,"E9.3.38.0"),sQuery(id+"F0.wireOp",EDGE,"E9.7.38.0"),sQuery(id+"F0.wireOp",EDGE,"E9.11.38.0"),sQuery(id+"F0.wireOp",EDGE,"E9.14.38.0"),sQuery(id+"F0.wireOp",EDGE,"E9.1.39.0"),sQuery(id+"F0.wireOp",EDGE,"E9.3.39.0"),sQuery(id+"F0.wireOp",EDGE,"E9.7.39.0"),sQuery(id+"F0.wireOp",EDGE,"E9.11.39.0"),sQuery(id+"F0.wireOp",EDGE,"E9.14.39.0"),sQuery(id+"F0.wireOp",EDGE,"E9.1.40.0"),sQuery(id+"F0.wireOp",EDGE,"E9.3.40.0"),sQuery(id+"F0.wireOp",EDGE,"E9.7.40.0"),sQuery(id+"F0.wireOp",EDGE,"E9.11.40.0"),sQuery(id+"F0.wireOp",EDGE,"E9.14.40.0"),sQuery(id+"F0.wireOp",EDGE,"E9.1.41.0"),sQuery(id+"F0.wireOp",EDGE,"E9.3.41.0"),sQuery(id+"F0.wireOp",EDGE,"E9.7.41.0"),sQuery(id+"F0.wireOp",EDGE,"E9.11.41.0"),sQuery(id+"F0.wireOp",EDGE,"E9.14.41.0"),sQuery(id+"F0.wireOp",EDGE,"E9.1.42.0"),sQuery(id+"F0.wireOp",EDGE,"E9.3.42.0"),sQuery(id+"F0.wireOp",EDGE,"E9.7.42.0"),sQuery(id+"F0.wireOp",EDGE,"E9.11.42.0"),sQuery(id+"F0.wireOp",EDGE,"E9.14.42.0"),sQuery(id+"F0.wireOp",EDGE,"E9.1.43.0"),sQuery(id+"F0.wireOp",EDGE,"E9.3.43.0"),sQuery(id+"F0.wireOp",EDGE,"E9.7.43.0"),sQuery(id+"F0.wireOp",EDGE,"E9.11.43.0"),sQuery(id+"F0.wireOp",EDGE,"E9.14.43.0"),sQuery(id+"F0.wireOp",EDGE,"E9.1.44.0"),sQuery(id+"F0.wireOp",EDGE,"E9.3.44.0"),sQuery(id+"F0.wireOp",EDGE,"E9.7.44.0"),sQuery(id+"F0.wireOp",EDGE,"E9.11.44.0"),sQuery(id+"F0.wireOp",EDGE,"E9.14.44.0"),sQuery(id+"F0.wireOp",EDGE,"E9.1.45.0"),sQuery(id+"F0.wireOp",EDGE,"E9.3.45.0"),sQuery(id+"F0.wireOp",EDGE,"E9.7.45.0"),sQuery(id+"F0.wireOp",EDGE,"E9.11.45.0"),sQuery(id+"F0.wireOp",EDGE,"E9.14.45.0"),sQuery(id+"F0.wireOp",EDGE,"E9.1.46.0"),sQuery(id+"F0.wireOp",EDGE,"E9.3.46.0"),sQuery(id+"F0.wireOp",EDGE,"E9.7.46.0"),sQuery(id+"F0.wireOp",EDGE,"E9.11.46.0"),sQuery(id+"F0.wireOp",EDGE,"E9.14.46.0"),sQuery(id+"F0.wireOp",EDGE,"E9.1.47.0"),sQuery(id+"F0.wireOp",EDGE,"E9.3.47.0"),sQuery(id+"F0.wireOp",EDGE,"E9.7.47.0"),sQuery(id+"F0.wireOp",EDGE,"E9.11.47.0"),sQuery(id+"F0.wireOp",EDGE,"E9.14.47.0"),sQuery(id+"F0.wireOp",EDGE,"E9.1.48.0"),sQuery(id+"F0.wireOp",EDGE,"E9.3.48.0"),sQuery(id+"F0.wireOp",EDGE,"E9.7.48.0"),sQuery(id+"F0.wireOp",EDGE,"E9.11.48.0"),sQuery(id+"F0.wireOp",EDGE,"E9.14.48.0"),sQuery(id+"F0.wireOp",EDGE,"E9.1.49.0"),sQuery(id+"F0.wireOp",EDGE,"E9.3.49.0"),sQuery(id+"F0.wireOp",EDGE,"E9.7.49.0"),sQuery(id+"F0.wireOp",EDGE,"E9.11.49.0"),sQuery(id+"F0.wireOp",EDGE,"E9.14.49.0"),sQuery(id+"F0.wireOp",EDGE,"E9.1.50.0"),sQuery(id+"F0.wireOp",EDGE,"E9.3.50.0"),sQuery(id+"F0.wireOp",EDGE,"E9.7.50.0"),sQuery(id+"F0.wireOp",EDGE,"E9.11.50.0"),sQuery(id+"F0.wireOp",EDGE,"E9.14.50.0"),sQuery(id+"F0.wireOp",EDGE,"E9.1.51.0"),sQuery(id+"F0.wireOp",EDGE,"E9.3.51.0"),sQuery(id+"F0.wireOp",EDGE,"E9.7.51.0"),sQuery(id+"F0.wireOp",EDGE,"E9.11.51.0"),sQuery(id+"F0.wireOp",EDGE,"E9.14.51.0"),sQuery(id+"F0.wireOp",EDGE,"E9.1.52.0"),sQuery(id+"F0.wireOp",EDGE,"E9.3.52.0"),sQuery(id+"F0.wireOp",EDGE,"E9.7.52.0"),sQuery(id+"F0.wireOp",EDGE,"E9.11.52.0"),sQuery(id+"F0.wireOp",EDGE,"E9.14.52.0"),sQuery(id+"F0.wireOp",EDGE,"E9.1.53.0"),sQuery(id+"F0.wireOp",EDGE,"E9.3.53.0"),sQuery(id+"F0.wireOp",EDGE,"E9.7.53.0"),sQuery(id+"F0.wireOp",EDGE,"E9.11.53.0"),sQuery(id+"F0.wireOp",EDGE,"E9.14.53.0"),sQuery(id+"F0.wireOp",EDGE,"E9.1.54.0"),sQuery(id+"F0.wireOp",EDGE,"E9.3.54.0"),sQuery(id+"F0.wireOp",EDGE,"E9.7.54.0"),sQuery(id+"F0.wireOp",EDGE,"E9.11.54.0"),sQuery(id+"F0.wireOp",EDGE,"E9.14.54.0"),sQuery(id+"F0.wireOp",EDGE,"E9.1.55.0"),sQuery(id+"F0.wireOp",EDGE,"E9.3.55.0"),sQuery(id+"F0.wireOp",EDGE,"E9.7.55.0"),sQuery(id+"F0.wireOp",EDGE,"E9.11.55.0"),sQuery(id+"F0.wireOp",EDGE,"E9.14.55.0"),sQuery(id+"F0.wireOp",EDGE,"E9.1.56.0"),sQuery(id+"F0.wireOp",EDGE,"E9.3.56.0"),sQuery(id+"F0.wireOp",EDGE,"E9.7.56.0"),sQuery(id+"F0.wireOp",EDGE,"E9.11.56.0"),sQuery(id+"F0.wireOp",EDGE,"E9.14.56.0"),sQuery(id+"F0.wireOp",EDGE,"E9.1.57.0"),sQuery(id+"F0.wireOp",EDGE,"E9.3.57.0"),sQuery(id+"F0.wireOp",EDGE,"E9.7.57.0"),sQuery(id+"F0.wireOp",EDGE,"E9.11.57.0"),sQuery(id+"F0.wireOp",EDGE,"E9.14.57.0"),sQuery(id+"F0.wireOp",EDGE,"E9.1.58.0"),sQuery(id+"F0.wireOp",EDGE,"E9.3.58.0"),sQuery(id+"F0.wireOp",EDGE,"E9.7.58.0"),sQuery(id+"F0.wireOp",EDGE,"E9.11.58.0"),sQuery(id+"F0.wireOp",EDGE,"E9.14.58.0"),sQuery(id+"F0.wireOp",EDGE,"E9.1.59.0"),sQuery(id+"F0.wireOp",EDGE,"E9.3.59.0"),sQuery(id+"F0.wireOp",EDGE,"E9.7.59.0"),sQuery(id+"F0.wireOp",EDGE,"E9.11.59.0"),sQuery(id+"F0.wireOp",EDGE,"E9.14.59.0")])],"isStart":true});
            var sketch = newSketch(context, id + "F3", { "sketchPlane" : qUnion([Q0])});
            skCircle(sketch, "E39", {"center": v(-0.15, 0.02) * mm, "radius": 64 * mm});
            skCircle(sketch, "E40", {"center": v(-0.15, 0.02) * mm, "radius": 63 * mm});
            skCircle(sketch, "E41", {"center": v(-0.15, 0.02) * mm, "radius": 60 * mm});
            skCircle(sketch, "E42", {"center": v(-0.15, 0.02) * mm, "radius": 59 * mm});
            skCircle(sketch, "E43", {"center": v(-0.15, 0.02) * mm, "radius": 10 * mm});
            skSolve(sketch);
        }
        {
            var Q0;
            Q0=makeQuery(id+"F3.imprint","IMPRINT",FACE,{"disambiguationData":[TD([[makeQuery(id+"F3.imprint","IMPRINT",EDGE,{"derivedFrom":sQuery(id+"F3.wireOp",EDGE,"E39")}),1.0]])]});
            var Q1;
            Q1=makeQuery(id+"F3.imprint","IMPRINT",FACE,{"disambiguationData":[TD([[makeQuery(id+"F3.imprint","IMPRINT",EDGE,{"derivedFrom":sQuery(id+"F3.wireOp",EDGE,"E42")}),1.0]])]});
            var Q2;
            Q2=qConstructionFilter(qBodyType(qCreatedBy(id+"F3",EDGE),BodyType.WIRE),ConstructionObject.NO);
            extrude(context, id + "F4", {"entities" : qUnion([Q0, Q1]), "operationType" : NewBodyOperationType.REMOVE, "surfaceEntities" : qUnion([Q2]), "oppositeDirection" : true, "depth" : 1 * mm, "offsetDistance" : 25 * mm});
        }
        {
            var Q0;
            Q0=makeQuery(id+"FLAiNYIGUJVPJrN_1.boolean.opBoolean","SPLIT",FACE,{"disambiguationData":[TD([makeQuery(id+"FLAiNYIGUJVPJrN_1.opExtrude","SWEPT_FACE",FACE,{"disambiguationData":[OSD([sQuery(id+"F2.wireOp",EDGE,"E15")])]})])],"derivedFrom":makeQuery(id+"F1.opExtrude","CAP_FACE",FACE,{"disambiguationData":[OSD([sQuery(id+"F0.wireOp",EDGE,"E0"),sQuery(id+"F0.wireOp",EDGE,"E1"),sQuery(id+"F0.wireOp",EDGE,"E3"),sQuery(id+"F0.wireOp",EDGE,"E4"),sQuery(id+"F0.wireOp",EDGE,"E5"),sQuery(id+"F0.wireOp",EDGE,"E6.trimOffspring"),sQuery(id+"F0.wireOp",EDGE,"E7"),sQuery(id+"F0.wireOp",EDGE,"E8.1.0"),sQuery(id+"F0.wireOp",EDGE,"E8.1.1"),sQuery(id+"F0.wireOp",EDGE,"E8.1.2"),sQuery(id+"F0.wireOp",EDGE,"E8.1.3"),sQuery(id+"F0.wireOp",EDGE,"E8.1.4"),sQuery(id+"F0.wireOp",EDGE,"E8.2.0"),sQuery(id+"F0.wireOp",EDGE,"E8.2.1"),sQuery(id+"F0.wireOp",EDGE,"E8.2.2"),sQuery(id+"F0.wireOp",EDGE,"E8.2.3"),sQuery(id+"F0.wireOp",EDGE,"E8.2.4"),sQuery(id+"F0.wireOp",EDGE,"E9.1.3.0"),sQuery(id+"F0.wireOp",EDGE,"E9.3.3.0"),sQuery(id+"F0.wireOp",EDGE,"E9.7.3.0"),sQuery(id+"F0.wireOp",EDGE,"E9.11.3.0"),sQuery(id+"F0.wireOp",EDGE,"E9.14.3.0"),sQuery(id+"F0.wireOp",EDGE,"E9.1.4.0"),sQuery(id+"F0.wireOp",EDGE,"E9.3.4.0"),sQuery(id+"F0.wireOp",EDGE,"E9.7.4.0"),sQuery(id+"F0.wireOp",EDGE,"E9.11.4.0"),sQuery(id+"F0.wireOp",EDGE,"E9.14.4.0"),sQuery(id+"F0.wireOp",EDGE,"E9.1.5.0"),sQuery(id+"F0.wireOp",EDGE,"E9.3.5.0"),sQuery(id+"F0.wireOp",EDGE,"E9.7.5.0"),sQuery(id+"F0.wireOp",EDGE,"E9.11.5.0"),sQuery(id+"F0.wireOp",EDGE,"E9.14.5.0"),sQuery(id+"F0.wireOp",EDGE,"E9.1.6.0"),sQuery(id+"F0.wireOp",EDGE,"E9.3.6.0"),sQuery(id+"F0.wireOp",EDGE,"E9.7.6.0"),sQuery(id+"F0.wireOp",EDGE,"E9.11.6.0"),sQuery(id+"F0.wireOp",EDGE,"E9.14.6.0"),sQuery(id+"F0.wireOp",EDGE,"E9.1.7.0"),sQuery(id+"F0.wireOp",EDGE,"E9.3.7.0"),sQuery(id+"F0.wireOp",EDGE,"E9.7.7.0"),sQuery(id+"F0.wireOp",EDGE,"E9.11.7.0"),sQuery(id+"F0.wireOp",EDGE,"E9.14.7.0"),sQuery(id+"F0.wireOp",EDGE,"E9.1.8.0"),sQuery(id+"F0.wireOp",EDGE,"E9.3.8.0"),sQuery(id+"F0.wireOp",EDGE,"E9.7.8.0"),sQuery(id+"F0.wireOp",EDGE,"E9.11.8.0"),sQuery(id+"F0.wireOp",EDGE,"E9.14.8.0"),sQuery(id+"F0.wireOp",EDGE,"E9.1.9.0"),sQuery(id+"F0.wireOp",EDGE,"E9.3.9.0"),sQuery(id+"F0.wireOp",EDGE,"E9.7.9.0"),sQuery(id+"F0.wireOp",EDGE,"E9.11.9.0"),sQuery(id+"F0.wireOp",EDGE,"E9.14.9.0"),sQuery(id+"F0.wireOp",EDGE,"E9.1.10.0"),sQuery(id+"F0.wireOp",EDGE,"E9.3.10.0"),sQuery(id+"F0.wireOp",EDGE,"E9.7.10.0"),sQuery(id+"F0.wireOp",EDGE,"E9.11.10.0"),sQuery(id+"F0.wireOp",EDGE,"E9.14.10.0"),sQuery(id+"F0.wireOp",EDGE,"E9.1.11.0"),sQuery(id+"F0.wireOp",EDGE,"E9.3.11.0"),sQuery(id+"F0.wireOp",EDGE,"E9.7.11.0"),sQuery(id+"F0.wireOp",EDGE,"E9.11.11.0"),sQuery(id+"F0.wireOp",EDGE,"E9.14.11.0"),sQuery(id+"F0.wireOp",EDGE,"E9.1.12.0"),sQuery(id+"F0.wireOp",EDGE,"E9.3.12.0"),sQuery(id+"F0.wireOp",EDGE,"E9.7.12.0"),sQuery(id+"F0.wireOp",EDGE,"E9.11.12.0"),sQuery(id+"F0.wireOp",EDGE,"E9.14.12.0"),sQuery(id+"F0.wireOp",EDGE,"E9.1.13.0"),sQuery(id+"F0.wireOp",EDGE,"E9.3.13.0"),sQuery(id+"F0.wireOp",EDGE,"E9.7.13.0"),sQuery(id+"F0.wireOp",EDGE,"E9.11.13.0"),sQuery(id+"F0.wireOp",EDGE,"E9.14.13.0"),sQuery(id+"F0.wireOp",EDGE,"E9.1.14.0"),sQuery(id+"F0.wireOp",EDGE,"E9.3.14.0"),sQuery(id+"F0.wireOp",EDGE,"E9.7.14.0"),sQuery(id+"F0.wireOp",EDGE,"E9.11.14.0"),sQuery(id+"F0.wireOp",EDGE,"E9.14.14.0"),sQuery(id+"F0.wireOp",EDGE,"E9.1.15.0"),sQuery(id+"F0.wireOp",EDGE,"E9.3.15.0"),sQuery(id+"F0.wireOp",EDGE,"E9.7.15.0"),sQuery(id+"F0.wireOp",EDGE,"E9.11.15.0"),sQuery(id+"F0.wireOp",EDGE,"E9.14.15.0"),sQuery(id+"F0.wireOp",EDGE,"E9.1.16.0"),sQuery(id+"F0.wireOp",EDGE,"E9.3.16.0"),sQuery(id+"F0.wireOp",EDGE,"E9.7.16.0"),sQuery(id+"F0.wireOp",EDGE,"E9.11.16.0"),sQuery(id+"F0.wireOp",EDGE,"E9.14.16.0"),sQuery(id+"F0.wireOp",EDGE,"E9.1.17.0"),sQuery(id+"F0.wireOp",EDGE,"E9.3.17.0"),sQuery(id+"F0.wireOp",EDGE,"E9.7.17.0"),sQuery(id+"F0.wireOp",EDGE,"E9.11.17.0"),sQuery(id+"F0.wireOp",EDGE,"E9.14.17.0"),sQuery(id+"F0.wireOp",EDGE,"E9.1.18.0"),sQuery(id+"F0.wireOp",EDGE,"E9.3.18.0"),sQuery(id+"F0.wireOp",EDGE,"E9.7.18.0"),sQuery(id+"F0.wireOp",EDGE,"E9.11.18.0"),sQuery(id+"F0.wireOp",EDGE,"E9.14.18.0"),sQuery(id+"F0.wireOp",EDGE,"E9.1.19.0"),sQuery(id+"F0.wireOp",EDGE,"E9.3.19.0"),sQuery(id+"F0.wireOp",EDGE,"E9.7.19.0"),sQuery(id+"F0.wireOp",EDGE,"E9.11.19.0"),sQuery(id+"F0.wireOp",EDGE,"E9.14.19.0"),sQuery(id+"F0.wireOp",EDGE,"E9.1.20.0"),sQuery(id+"F0.wireOp",EDGE,"E9.3.20.0"),sQuery(id+"F0.wireOp",EDGE,"E9.7.20.0"),sQuery(id+"F0.wireOp",EDGE,"E9.11.20.0"),sQuery(id+"F0.wireOp",EDGE,"E9.14.20.0"),sQuery(id+"F0.wireOp",EDGE,"E9.1.21.0"),sQuery(id+"F0.wireOp",EDGE,"E9.3.21.0"),sQuery(id+"F0.wireOp",EDGE,"E9.7.21.0"),sQuery(id+"F0.wireOp",EDGE,"E9.11.21.0"),sQuery(id+"F0.wireOp",EDGE,"E9.14.21.0"),sQuery(id+"F0.wireOp",EDGE,"E9.1.22.0"),sQuery(id+"F0.wireOp",EDGE,"E9.3.22.0"),sQuery(id+"F0.wireOp",EDGE,"E9.7.22.0"),sQuery(id+"F0.wireOp",EDGE,"E9.11.22.0"),sQuery(id+"F0.wireOp",EDGE,"E9.14.22.0"),sQuery(id+"F0.wireOp",EDGE,"E9.1.23.0"),sQuery(id+"F0.wireOp",EDGE,"E9.3.23.0"),sQuery(id+"F0.wireOp",EDGE,"E9.7.23.0"),sQuery(id+"F0.wireOp",EDGE,"E9.11.23.0"),sQuery(id+"F0.wireOp",EDGE,"E9.14.23.0"),sQuery(id+"F0.wireOp",EDGE,"E9.1.24.0"),sQuery(id+"F0.wireOp",EDGE,"E9.3.24.0"),sQuery(id+"F0.wireOp",EDGE,"E9.7.24.0"),sQuery(id+"F0.wireOp",EDGE,"E9.11.24.0"),sQuery(id+"F0.wireOp",EDGE,"E9.14.24.0"),sQuery(id+"F0.wireOp",EDGE,"E9.1.25.0"),sQuery(id+"F0.wireOp",EDGE,"E9.3.25.0"),sQuery(id+"F0.wireOp",EDGE,"E9.7.25.0"),sQuery(id+"F0.wireOp",EDGE,"E9.11.25.0"),sQuery(id+"F0.wireOp",EDGE,"E9.14.25.0"),sQuery(id+"F0.wireOp",EDGE,"E9.1.26.0"),sQuery(id+"F0.wireOp",EDGE,"E9.3.26.0"),sQuery(id+"F0.wireOp",EDGE,"E9.7.26.0"),sQuery(id+"F0.wireOp",EDGE,"E9.11.26.0"),sQuery(id+"F0.wireOp",EDGE,"E9.14.26.0"),sQuery(id+"F0.wireOp",EDGE,"E9.1.27.0"),sQuery(id+"F0.wireOp",EDGE,"E9.3.27.0"),sQuery(id+"F0.wireOp",EDGE,"E9.7.27.0"),sQuery(id+"F0.wireOp",EDGE,"E9.11.27.0"),sQuery(id+"F0.wireOp",EDGE,"E9.14.27.0"),sQuery(id+"F0.wireOp",EDGE,"E9.1.28.0"),sQuery(id+"F0.wireOp",EDGE,"E9.3.28.0"),sQuery(id+"F0.wireOp",EDGE,"E9.7.28.0"),sQuery(id+"F0.wireOp",EDGE,"E9.11.28.0"),sQuery(id+"F0.wireOp",EDGE,"E9.14.28.0"),sQuery(id+"F0.wireOp",EDGE,"E9.1.29.0"),sQuery(id+"F0.wireOp",EDGE,"E9.3.29.0"),sQuery(id+"F0.wireOp",EDGE,"E9.7.29.0"),sQuery(id+"F0.wireOp",EDGE,"E9.11.29.0"),sQuery(id+"F0.wireOp",EDGE,"E9.14.29.0"),sQuery(id+"F0.wireOp",EDGE,"E9.1.30.0"),sQuery(id+"F0.wireOp",EDGE,"E9.3.30.0"),sQuery(id+"F0.wireOp",EDGE,"E9.7.30.0"),sQuery(id+"F0.wireOp",EDGE,"E9.11.30.0"),sQuery(id+"F0.wireOp",EDGE,"E9.14.30.0"),sQuery(id+"F0.wireOp",EDGE,"E9.1.31.0"),sQuery(id+"F0.wireOp",EDGE,"E9.3.31.0"),sQuery(id+"F0.wireOp",EDGE,"E9.7.31.0"),sQuery(id+"F0.wireOp",EDGE,"E9.11.31.0"),sQuery(id+"F0.wireOp",EDGE,"E9.14.31.0"),sQuery(id+"F0.wireOp",EDGE,"E9.1.32.0"),sQuery(id+"F0.wireOp",EDGE,"E9.3.32.0"),sQuery(id+"F0.wireOp",EDGE,"E9.7.32.0"),sQuery(id+"F0.wireOp",EDGE,"E9.11.32.0"),sQuery(id+"F0.wireOp",EDGE,"E9.14.32.0"),sQuery(id+"F0.wireOp",EDGE,"E9.1.33.0"),sQuery(id+"F0.wireOp",EDGE,"E9.3.33.0"),sQuery(id+"F0.wireOp",EDGE,"E9.7.33.0"),sQuery(id+"F0.wireOp",EDGE,"E9.11.33.0"),sQuery(id+"F0.wireOp",EDGE,"E9.14.33.0"),sQuery(id+"F0.wireOp",EDGE,"E9.1.34.0"),sQuery(id+"F0.wireOp",EDGE,"E9.3.34.0"),sQuery(id+"F0.wireOp",EDGE,"E9.7.34.0"),sQuery(id+"F0.wireOp",EDGE,"E9.11.34.0"),sQuery(id+"F0.wireOp",EDGE,"E9.14.34.0"),sQuery(id+"F0.wireOp",EDGE,"E9.1.35.0"),sQuery(id+"F0.wireOp",EDGE,"E9.3.35.0"),sQuery(id+"F0.wireOp",EDGE,"E9.7.35.0"),sQuery(id+"F0.wireOp",EDGE,"E9.11.35.0"),sQuery(id+"F0.wireOp",EDGE,"E9.14.35.0"),sQuery(id+"F0.wireOp",EDGE,"E9.1.36.0"),sQuery(id+"F0.wireOp",EDGE,"E9.3.36.0"),sQuery(id+"F0.wireOp",EDGE,"E9.7.36.0"),sQuery(id+"F0.wireOp",EDGE,"E9.11.36.0"),sQuery(id+"F0.wireOp",EDGE,"E9.14.36.0"),sQuery(id+"F0.wireOp",EDGE,"E9.1.37.0"),sQuery(id+"F0.wireOp",EDGE,"E9.3.37.0"),sQuery(id+"F0.wireOp",EDGE,"E9.7.37.0"),sQuery(id+"F0.wireOp",EDGE,"E9.11.37.0"),sQuery(id+"F0.wireOp",EDGE,"E9.14.37.0"),sQuery(id+"F0.wireOp",EDGE,"E9.1.38.0"),sQuery(id+"F0.wireOp",EDGE,"E9.3.38.0"),sQuery(id+"F0.wireOp",EDGE,"E9.7.38.0"),sQuery(id+"F0.wireOp",EDGE,"E9.11.38.0"),sQuery(id+"F0.wireOp",EDGE,"E9.14.38.0"),sQuery(id+"F0.wireOp",EDGE,"E9.1.39.0"),sQuery(id+"F0.wireOp",EDGE,"E9.3.39.0"),sQuery(id+"F0.wireOp",EDGE,"E9.7.39.0"),sQuery(id+"F0.wireOp",EDGE,"E9.11.39.0"),sQuery(id+"F0.wireOp",EDGE,"E9.14.39.0"),sQuery(id+"F0.wireOp",EDGE,"E9.1.40.0"),sQuery(id+"F0.wireOp",EDGE,"E9.3.40.0"),sQuery(id+"F0.wireOp",EDGE,"E9.7.40.0"),sQuery(id+"F0.wireOp",EDGE,"E9.11.40.0"),sQuery(id+"F0.wireOp",EDGE,"E9.14.40.0"),sQuery(id+"F0.wireOp",EDGE,"E9.1.41.0"),sQuery(id+"F0.wireOp",EDGE,"E9.3.41.0"),sQuery(id+"F0.wireOp",EDGE,"E9.7.41.0"),sQuery(id+"F0.wireOp",EDGE,"E9.11.41.0"),sQuery(id+"F0.wireOp",EDGE,"E9.14.41.0"),sQuery(id+"F0.wireOp",EDGE,"E9.1.42.0"),sQuery(id+"F0.wireOp",EDGE,"E9.3.42.0"),sQuery(id+"F0.wireOp",EDGE,"E9.7.42.0"),sQuery(id+"F0.wireOp",EDGE,"E9.11.42.0"),sQuery(id+"F0.wireOp",EDGE,"E9.14.42.0"),sQuery(id+"F0.wireOp",EDGE,"E9.1.43.0"),sQuery(id+"F0.wireOp",EDGE,"E9.3.43.0"),sQuery(id+"F0.wireOp",EDGE,"E9.7.43.0"),sQuery(id+"F0.wireOp",EDGE,"E9.11.43.0"),sQuery(id+"F0.wireOp",EDGE,"E9.14.43.0"),sQuery(id+"F0.wireOp",EDGE,"E9.1.44.0"),sQuery(id+"F0.wireOp",EDGE,"E9.3.44.0"),sQuery(id+"F0.wireOp",EDGE,"E9.7.44.0"),sQuery(id+"F0.wireOp",EDGE,"E9.11.44.0"),sQuery(id+"F0.wireOp",EDGE,"E9.14.44.0"),sQuery(id+"F0.wireOp",EDGE,"E9.1.45.0"),sQuery(id+"F0.wireOp",EDGE,"E9.3.45.0"),sQuery(id+"F0.wireOp",EDGE,"E9.7.45.0"),sQuery(id+"F0.wireOp",EDGE,"E9.11.45.0"),sQuery(id+"F0.wireOp",EDGE,"E9.14.45.0"),sQuery(id+"F0.wireOp",EDGE,"E9.1.46.0"),sQuery(id+"F0.wireOp",EDGE,"E9.3.46.0"),sQuery(id+"F0.wireOp",EDGE,"E9.7.46.0"),sQuery(id+"F0.wireOp",EDGE,"E9.11.46.0"),sQuery(id+"F0.wireOp",EDGE,"E9.14.46.0"),sQuery(id+"F0.wireOp",EDGE,"E9.1.47.0"),sQuery(id+"F0.wireOp",EDGE,"E9.3.47.0"),sQuery(id+"F0.wireOp",EDGE,"E9.7.47.0"),sQuery(id+"F0.wireOp",EDGE,"E9.11.47.0"),sQuery(id+"F0.wireOp",EDGE,"E9.14.47.0"),sQuery(id+"F0.wireOp",EDGE,"E9.1.48.0"),sQuery(id+"F0.wireOp",EDGE,"E9.3.48.0"),sQuery(id+"F0.wireOp",EDGE,"E9.7.48.0"),sQuery(id+"F0.wireOp",EDGE,"E9.11.48.0"),sQuery(id+"F0.wireOp",EDGE,"E9.14.48.0"),sQuery(id+"F0.wireOp",EDGE,"E9.1.49.0"),sQuery(id+"F0.wireOp",EDGE,"E9.3.49.0"),sQuery(id+"F0.wireOp",EDGE,"E9.7.49.0"),sQuery(id+"F0.wireOp",EDGE,"E9.11.49.0"),sQuery(id+"F0.wireOp",EDGE,"E9.14.49.0"),sQuery(id+"F0.wireOp",EDGE,"E9.1.50.0"),sQuery(id+"F0.wireOp",EDGE,"E9.3.50.0"),sQuery(id+"F0.wireOp",EDGE,"E9.7.50.0"),sQuery(id+"F0.wireOp",EDGE,"E9.11.50.0"),sQuery(id+"F0.wireOp",EDGE,"E9.14.50.0"),sQuery(id+"F0.wireOp",EDGE,"E9.1.51.0"),sQuery(id+"F0.wireOp",EDGE,"E9.3.51.0"),sQuery(id+"F0.wireOp",EDGE,"E9.7.51.0"),sQuery(id+"F0.wireOp",EDGE,"E9.11.51.0"),sQuery(id+"F0.wireOp",EDGE,"E9.14.51.0"),sQuery(id+"F0.wireOp",EDGE,"E9.1.52.0"),sQuery(id+"F0.wireOp",EDGE,"E9.3.52.0"),sQuery(id+"F0.wireOp",EDGE,"E9.7.52.0"),sQuery(id+"F0.wireOp",EDGE,"E9.11.52.0"),sQuery(id+"F0.wireOp",EDGE,"E9.14.52.0"),sQuery(id+"F0.wireOp",EDGE,"E9.1.53.0"),sQuery(id+"F0.wireOp",EDGE,"E9.3.53.0"),sQuery(id+"F0.wireOp",EDGE,"E9.7.53.0"),sQuery(id+"F0.wireOp",EDGE,"E9.11.53.0"),sQuery(id+"F0.wireOp",EDGE,"E9.14.53.0"),sQuery(id+"F0.wireOp",EDGE,"E9.1.54.0"),sQuery(id+"F0.wireOp",EDGE,"E9.3.54.0"),sQuery(id+"F0.wireOp",EDGE,"E9.7.54.0"),sQuery(id+"F0.wireOp",EDGE,"E9.11.54.0"),sQuery(id+"F0.wireOp",EDGE,"E9.14.54.0"),sQuery(id+"F0.wireOp",EDGE,"E9.1.55.0"),sQuery(id+"F0.wireOp",EDGE,"E9.3.55.0"),sQuery(id+"F0.wireOp",EDGE,"E9.7.55.0"),sQuery(id+"F0.wireOp",EDGE,"E9.11.55.0"),sQuery(id+"F0.wireOp",EDGE,"E9.14.55.0"),sQuery(id+"F0.wireOp",EDGE,"E9.1.56.0"),sQuery(id+"F0.wireOp",EDGE,"E9.3.56.0"),sQuery(id+"F0.wireOp",EDGE,"E9.7.56.0"),sQuery(id+"F0.wireOp",EDGE,"E9.11.56.0"),sQuery(id+"F0.wireOp",EDGE,"E9.14.56.0"),sQuery(id+"F0.wireOp",EDGE,"E9.1.57.0"),sQuery(id+"F0.wireOp",EDGE,"E9.3.57.0"),sQuery(id+"F0.wireOp",EDGE,"E9.7.57.0"),sQuery(id+"F0.wireOp",EDGE,"E9.11.57.0"),sQuery(id+"F0.wireOp",EDGE,"E9.14.57.0"),sQuery(id+"F0.wireOp",EDGE,"E9.1.58.0"),sQuery(id+"F0.wireOp",EDGE,"E9.3.58.0"),sQuery(id+"F0.wireOp",EDGE,"E9.7.58.0"),sQuery(id+"F0.wireOp",EDGE,"E9.11.58.0"),sQuery(id+"F0.wireOp",EDGE,"E9.14.58.0"),sQuery(id+"F0.wireOp",EDGE,"E9.1.59.0"),sQuery(id+"F0.wireOp",EDGE,"E9.3.59.0"),sQuery(id+"F0.wireOp",EDGE,"E9.7.59.0"),sQuery(id+"F0.wireOp",EDGE,"E9.11.59.0"),sQuery(id+"F0.wireOp",EDGE,"E9.14.59.0")])],"isStart":false})});
            extrude(context, id + "F5", {"entities" : qUnion([Q0]), "operationType" : NewBodyOperationType.REMOVE, "oppositeDirection" : true, "depth" : 1 * mm, "offsetDistance" : 25 * mm});
        }
        {
            var Q0;
            Q0=makeQuery(id+"F2.imprint","IMPRINT",FACE,{"disambiguationData":[TD([[makeQuery(id+"F2.imprint","IMPRINT",EDGE,{"derivedFrom":sQuery(id+"F2.wireOp",EDGE,"E19")}),1.0]])]});
            var Q1;
            Q1=makeQuery(id+"F2.imprint","IMPRINT",FACE,{"disambiguationData":[TD([[makeQuery(id+"F2.imprint","IMPRINT",EDGE,{"derivedFrom":sQuery(id+"F2.wireOp",EDGE,"E23")}),1.0]])]});
            var Q2;
            Q2=makeQuery(id+"F2.imprint","IMPRINT",FACE,{"disambiguationData":[TD([[makeQuery(id+"F2.imprint","IMPRINT",EDGE,{"derivedFrom":sQuery(id+"F2.wireOp",EDGE,"E22.0")}),-1.0]])]});
            var Q3;
            Q3=makeQuery(id+"F2.imprint","IMPRINT",FACE,{"disambiguationData":[TD([[makeQuery(id+"F2.imprint","IMPRINT",EDGE,{"derivedFrom":sQuery(id+"F2.wireOp",EDGE,"E20.0")}),-1.0]])]});
            extrude(context, id + "F6", {"entities" : qUnion([Q0, Q1, Q2, Q3]), "operationType" : NewBodyOperationType.REMOVE, "endBound" : BoundingType.THROUGH_ALL, "oppositeDirection" : true, "depth" : 25 * mm, "offsetDistance" : 25 * mm});
        }
        {
            var Q0;
            Q0=makeQuery(id+"F5.boolean.opBoolean","COPY",FACE,{"derivedFrom":makeQuery(id+"F5.opExtrude","CAP_FACE",FACE,{"disambiguationData":[OSD([sQuery(id+"F0.wireOp",EDGE,"E0"),sQuery(id+"F0.wireOp",EDGE,"E1"),sQuery(id+"F0.wireOp",EDGE,"E3"),sQuery(id+"F0.wireOp",EDGE,"E4"),sQuery(id+"F0.wireOp",EDGE,"E5"),sQuery(id+"F0.wireOp",EDGE,"E6.trimOffspring"),sQuery(id+"F0.wireOp",EDGE,"E7"),sQuery(id+"F0.wireOp",EDGE,"E8.1.0"),sQuery(id+"F0.wireOp",EDGE,"E8.1.1"),sQuery(id+"F0.wireOp",EDGE,"E8.1.2"),sQuery(id+"F0.wireOp",EDGE,"E8.1.3"),sQuery(id+"F0.wireOp",EDGE,"E8.1.4"),sQuery(id+"F0.wireOp",EDGE,"E8.2.0"),sQuery(id+"F0.wireOp",EDGE,"E8.2.1"),sQuery(id+"F0.wireOp",EDGE,"E8.2.2"),sQuery(id+"F0.wireOp",EDGE,"E8.2.3"),sQuery(id+"F0.wireOp",EDGE,"E8.2.4"),sQuery(id+"F0.wireOp",EDGE,"E9.1.3.0"),sQuery(id+"F0.wireOp",EDGE,"E9.3.3.0"),sQuery(id+"F0.wireOp",EDGE,"E9.7.3.0"),sQuery(id+"F0.wireOp",EDGE,"E9.11.3.0"),sQuery(id+"F0.wireOp",EDGE,"E9.14.3.0"),sQuery(id+"F0.wireOp",EDGE,"E9.1.4.0"),sQuery(id+"F0.wireOp",EDGE,"E9.3.4.0"),sQuery(id+"F0.wireOp",EDGE,"E9.7.4.0"),sQuery(id+"F0.wireOp",EDGE,"E9.11.4.0"),sQuery(id+"F0.wireOp",EDGE,"E9.14.4.0"),sQuery(id+"F0.wireOp",EDGE,"E9.1.5.0"),sQuery(id+"F0.wireOp",EDGE,"E9.3.5.0"),sQuery(id+"F0.wireOp",EDGE,"E9.7.5.0"),sQuery(id+"F0.wireOp",EDGE,"E9.11.5.0"),sQuery(id+"F0.wireOp",EDGE,"E9.14.5.0"),sQuery(id+"F0.wireOp",EDGE,"E9.1.6.0"),sQuery(id+"F0.wireOp",EDGE,"E9.3.6.0"),sQuery(id+"F0.wireOp",EDGE,"E9.7.6.0"),sQuery(id+"F0.wireOp",EDGE,"E9.11.6.0"),sQuery(id+"F0.wireOp",EDGE,"E9.14.6.0"),sQuery(id+"F0.wireOp",EDGE,"E9.1.7.0"),sQuery(id+"F0.wireOp",EDGE,"E9.3.7.0"),sQuery(id+"F0.wireOp",EDGE,"E9.7.7.0"),sQuery(id+"F0.wireOp",EDGE,"E9.11.7.0"),sQuery(id+"F0.wireOp",EDGE,"E9.14.7.0"),sQuery(id+"F0.wireOp",EDGE,"E9.1.8.0"),sQuery(id+"F0.wireOp",EDGE,"E9.3.8.0"),sQuery(id+"F0.wireOp",EDGE,"E9.7.8.0"),sQuery(id+"F0.wireOp",EDGE,"E9.11.8.0"),sQuery(id+"F0.wireOp",EDGE,"E9.14.8.0"),sQuery(id+"F0.wireOp",EDGE,"E9.1.9.0"),sQuery(id+"F0.wireOp",EDGE,"E9.3.9.0"),sQuery(id+"F0.wireOp",EDGE,"E9.7.9.0"),sQuery(id+"F0.wireOp",EDGE,"E9.11.9.0"),sQuery(id+"F0.wireOp",EDGE,"E9.14.9.0"),sQuery(id+"F0.wireOp",EDGE,"E9.1.10.0"),sQuery(id+"F0.wireOp",EDGE,"E9.3.10.0"),sQuery(id+"F0.wireOp",EDGE,"E9.7.10.0"),sQuery(id+"F0.wireOp",EDGE,"E9.11.10.0"),sQuery(id+"F0.wireOp",EDGE,"E9.14.10.0"),sQuery(id+"F0.wireOp",EDGE,"E9.1.11.0"),sQuery(id+"F0.wireOp",EDGE,"E9.3.11.0"),sQuery(id+"F0.wireOp",EDGE,"E9.7.11.0"),sQuery(id+"F0.wireOp",EDGE,"E9.11.11.0"),sQuery(id+"F0.wireOp",EDGE,"E9.14.11.0"),sQuery(id+"F0.wireOp",EDGE,"E9.1.12.0"),sQuery(id+"F0.wireOp",EDGE,"E9.3.12.0"),sQuery(id+"F0.wireOp",EDGE,"E9.7.12.0"),sQuery(id+"F0.wireOp",EDGE,"E9.11.12.0"),sQuery(id+"F0.wireOp",EDGE,"E9.14.12.0"),sQuery(id+"F0.wireOp",EDGE,"E9.1.13.0"),sQuery(id+"F0.wireOp",EDGE,"E9.3.13.0"),sQuery(id+"F0.wireOp",EDGE,"E9.7.13.0"),sQuery(id+"F0.wireOp",EDGE,"E9.11.13.0"),sQuery(id+"F0.wireOp",EDGE,"E9.14.13.0"),sQuery(id+"F0.wireOp",EDGE,"E9.1.14.0"),sQuery(id+"F0.wireOp",EDGE,"E9.3.14.0"),sQuery(id+"F0.wireOp",EDGE,"E9.7.14.0"),sQuery(id+"F0.wireOp",EDGE,"E9.11.14.0"),sQuery(id+"F0.wireOp",EDGE,"E9.14.14.0"),sQuery(id+"F0.wireOp",EDGE,"E9.1.15.0"),sQuery(id+"F0.wireOp",EDGE,"E9.3.15.0"),sQuery(id+"F0.wireOp",EDGE,"E9.7.15.0"),sQuery(id+"F0.wireOp",EDGE,"E9.11.15.0"),sQuery(id+"F0.wireOp",EDGE,"E9.14.15.0"),sQuery(id+"F0.wireOp",EDGE,"E9.1.16.0"),sQuery(id+"F0.wireOp",EDGE,"E9.3.16.0"),sQuery(id+"F0.wireOp",EDGE,"E9.7.16.0"),sQuery(id+"F0.wireOp",EDGE,"E9.11.16.0"),sQuery(id+"F0.wireOp",EDGE,"E9.14.16.0"),sQuery(id+"F0.wireOp",EDGE,"E9.1.17.0"),sQuery(id+"F0.wireOp",EDGE,"E9.3.17.0"),sQuery(id+"F0.wireOp",EDGE,"E9.7.17.0"),sQuery(id+"F0.wireOp",EDGE,"E9.11.17.0"),sQuery(id+"F0.wireOp",EDGE,"E9.14.17.0"),sQuery(id+"F0.wireOp",EDGE,"E9.1.18.0"),sQuery(id+"F0.wireOp",EDGE,"E9.3.18.0"),sQuery(id+"F0.wireOp",EDGE,"E9.7.18.0"),sQuery(id+"F0.wireOp",EDGE,"E9.11.18.0"),sQuery(id+"F0.wireOp",EDGE,"E9.14.18.0"),sQuery(id+"F0.wireOp",EDGE,"E9.1.19.0"),sQuery(id+"F0.wireOp",EDGE,"E9.3.19.0"),sQuery(id+"F0.wireOp",EDGE,"E9.7.19.0"),sQuery(id+"F0.wireOp",EDGE,"E9.11.19.0"),sQuery(id+"F0.wireOp",EDGE,"E9.14.19.0"),sQuery(id+"F0.wireOp",EDGE,"E9.1.20.0"),sQuery(id+"F0.wireOp",EDGE,"E9.3.20.0"),sQuery(id+"F0.wireOp",EDGE,"E9.7.20.0"),sQuery(id+"F0.wireOp",EDGE,"E9.11.20.0"),sQuery(id+"F0.wireOp",EDGE,"E9.14.20.0"),sQuery(id+"F0.wireOp",EDGE,"E9.1.21.0"),sQuery(id+"F0.wireOp",EDGE,"E9.3.21.0"),sQuery(id+"F0.wireOp",EDGE,"E9.7.21.0"),sQuery(id+"F0.wireOp",EDGE,"E9.11.21.0"),sQuery(id+"F0.wireOp",EDGE,"E9.14.21.0"),sQuery(id+"F0.wireOp",EDGE,"E9.1.22.0"),sQuery(id+"F0.wireOp",EDGE,"E9.3.22.0"),sQuery(id+"F0.wireOp",EDGE,"E9.7.22.0"),sQuery(id+"F0.wireOp",EDGE,"E9.11.22.0"),sQuery(id+"F0.wireOp",EDGE,"E9.14.22.0"),sQuery(id+"F0.wireOp",EDGE,"E9.1.23.0"),sQuery(id+"F0.wireOp",EDGE,"E9.3.23.0"),sQuery(id+"F0.wireOp",EDGE,"E9.7.23.0"),sQuery(id+"F0.wireOp",EDGE,"E9.11.23.0"),sQuery(id+"F0.wireOp",EDGE,"E9.14.23.0"),sQuery(id+"F0.wireOp",EDGE,"E9.1.24.0"),sQuery(id+"F0.wireOp",EDGE,"E9.3.24.0"),sQuery(id+"F0.wireOp",EDGE,"E9.7.24.0"),sQuery(id+"F0.wireOp",EDGE,"E9.11.24.0"),sQuery(id+"F0.wireOp",EDGE,"E9.14.24.0"),sQuery(id+"F0.wireOp",EDGE,"E9.1.25.0"),sQuery(id+"F0.wireOp",EDGE,"E9.3.25.0"),sQuery(id+"F0.wireOp",EDGE,"E9.7.25.0"),sQuery(id+"F0.wireOp",EDGE,"E9.11.25.0"),sQuery(id+"F0.wireOp",EDGE,"E9.14.25.0"),sQuery(id+"F0.wireOp",EDGE,"E9.1.26.0"),sQuery(id+"F0.wireOp",EDGE,"E9.3.26.0"),sQuery(id+"F0.wireOp",EDGE,"E9.7.26.0"),sQuery(id+"F0.wireOp",EDGE,"E9.11.26.0"),sQuery(id+"F0.wireOp",EDGE,"E9.14.26.0"),sQuery(id+"F0.wireOp",EDGE,"E9.1.27.0"),sQuery(id+"F0.wireOp",EDGE,"E9.3.27.0"),sQuery(id+"F0.wireOp",EDGE,"E9.7.27.0"),sQuery(id+"F0.wireOp",EDGE,"E9.11.27.0"),sQuery(id+"F0.wireOp",EDGE,"E9.14.27.0"),sQuery(id+"F0.wireOp",EDGE,"E9.1.28.0"),sQuery(id+"F0.wireOp",EDGE,"E9.3.28.0"),sQuery(id+"F0.wireOp",EDGE,"E9.7.28.0"),sQuery(id+"F0.wireOp",EDGE,"E9.11.28.0"),sQuery(id+"F0.wireOp",EDGE,"E9.14.28.0"),sQuery(id+"F0.wireOp",EDGE,"E9.1.29.0"),sQuery(id+"F0.wireOp",EDGE,"E9.3.29.0"),sQuery(id+"F0.wireOp",EDGE,"E9.7.29.0"),sQuery(id+"F0.wireOp",EDGE,"E9.11.29.0"),sQuery(id+"F0.wireOp",EDGE,"E9.14.29.0"),sQuery(id+"F0.wireOp",EDGE,"E9.1.30.0"),sQuery(id+"F0.wireOp",EDGE,"E9.3.30.0"),sQuery(id+"F0.wireOp",EDGE,"E9.7.30.0"),sQuery(id+"F0.wireOp",EDGE,"E9.11.30.0"),sQuery(id+"F0.wireOp",EDGE,"E9.14.30.0"),sQuery(id+"F0.wireOp",EDGE,"E9.1.31.0"),sQuery(id+"F0.wireOp",EDGE,"E9.3.31.0"),sQuery(id+"F0.wireOp",EDGE,"E9.7.31.0"),sQuery(id+"F0.wireOp",EDGE,"E9.11.31.0"),sQuery(id+"F0.wireOp",EDGE,"E9.14.31.0"),sQuery(id+"F0.wireOp",EDGE,"E9.1.32.0"),sQuery(id+"F0.wireOp",EDGE,"E9.3.32.0"),sQuery(id+"F0.wireOp",EDGE,"E9.7.32.0"),sQuery(id+"F0.wireOp",EDGE,"E9.11.32.0"),sQuery(id+"F0.wireOp",EDGE,"E9.14.32.0"),sQuery(id+"F0.wireOp",EDGE,"E9.1.33.0"),sQuery(id+"F0.wireOp",EDGE,"E9.3.33.0"),sQuery(id+"F0.wireOp",EDGE,"E9.7.33.0"),sQuery(id+"F0.wireOp",EDGE,"E9.11.33.0"),sQuery(id+"F0.wireOp",EDGE,"E9.14.33.0"),sQuery(id+"F0.wireOp",EDGE,"E9.1.34.0"),sQuery(id+"F0.wireOp",EDGE,"E9.3.34.0"),sQuery(id+"F0.wireOp",EDGE,"E9.7.34.0"),sQuery(id+"F0.wireOp",EDGE,"E9.11.34.0"),sQuery(id+"F0.wireOp",EDGE,"E9.14.34.0"),sQuery(id+"F0.wireOp",EDGE,"E9.1.35.0"),sQuery(id+"F0.wireOp",EDGE,"E9.3.35.0"),sQuery(id+"F0.wireOp",EDGE,"E9.7.35.0"),sQuery(id+"F0.wireOp",EDGE,"E9.11.35.0"),sQuery(id+"F0.wireOp",EDGE,"E9.14.35.0"),sQuery(id+"F0.wireOp",EDGE,"E9.1.36.0"),sQuery(id+"F0.wireOp",EDGE,"E9.3.36.0"),sQuery(id+"F0.wireOp",EDGE,"E9.7.36.0"),sQuery(id+"F0.wireOp",EDGE,"E9.11.36.0"),sQuery(id+"F0.wireOp",EDGE,"E9.14.36.0"),sQuery(id+"F0.wireOp",EDGE,"E9.1.37.0"),sQuery(id+"F0.wireOp",EDGE,"E9.3.37.0"),sQuery(id+"F0.wireOp",EDGE,"E9.7.37.0"),sQuery(id+"F0.wireOp",EDGE,"E9.11.37.0"),sQuery(id+"F0.wireOp",EDGE,"E9.14.37.0"),sQuery(id+"F0.wireOp",EDGE,"E9.1.38.0"),sQuery(id+"F0.wireOp",EDGE,"E9.3.38.0"),sQuery(id+"F0.wireOp",EDGE,"E9.7.38.0"),sQuery(id+"F0.wireOp",EDGE,"E9.11.38.0"),sQuery(id+"F0.wireOp",EDGE,"E9.14.38.0"),sQuery(id+"F0.wireOp",EDGE,"E9.1.39.0"),sQuery(id+"F0.wireOp",EDGE,"E9.3.39.0"),sQuery(id+"F0.wireOp",EDGE,"E9.7.39.0"),sQuery(id+"F0.wireOp",EDGE,"E9.11.39.0"),sQuery(id+"F0.wireOp",EDGE,"E9.14.39.0"),sQuery(id+"F0.wireOp",EDGE,"E9.1.40.0"),sQuery(id+"F0.wireOp",EDGE,"E9.3.40.0"),sQuery(id+"F0.wireOp",EDGE,"E9.7.40.0"),sQuery(id+"F0.wireOp",EDGE,"E9.11.40.0"),sQuery(id+"F0.wireOp",EDGE,"E9.14.40.0"),sQuery(id+"F0.wireOp",EDGE,"E9.1.41.0"),sQuery(id+"F0.wireOp",EDGE,"E9.3.41.0"),sQuery(id+"F0.wireOp",EDGE,"E9.7.41.0"),sQuery(id+"F0.wireOp",EDGE,"E9.11.41.0"),sQuery(id+"F0.wireOp",EDGE,"E9.14.41.0"),sQuery(id+"F0.wireOp",EDGE,"E9.1.42.0"),sQuery(id+"F0.wireOp",EDGE,"E9.3.42.0"),sQuery(id+"F0.wireOp",EDGE,"E9.7.42.0"),sQuery(id+"F0.wireOp",EDGE,"E9.11.42.0"),sQuery(id+"F0.wireOp",EDGE,"E9.14.42.0"),sQuery(id+"F0.wireOp",EDGE,"E9.1.43.0"),sQuery(id+"F0.wireOp",EDGE,"E9.3.43.0"),sQuery(id+"F0.wireOp",EDGE,"E9.7.43.0"),sQuery(id+"F0.wireOp",EDGE,"E9.11.43.0"),sQuery(id+"F0.wireOp",EDGE,"E9.14.43.0"),sQuery(id+"F0.wireOp",EDGE,"E9.1.44.0"),sQuery(id+"F0.wireOp",EDGE,"E9.3.44.0"),sQuery(id+"F0.wireOp",EDGE,"E9.7.44.0"),sQuery(id+"F0.wireOp",EDGE,"E9.11.44.0"),sQuery(id+"F0.wireOp",EDGE,"E9.14.44.0"),sQuery(id+"F0.wireOp",EDGE,"E9.1.45.0"),sQuery(id+"F0.wireOp",EDGE,"E9.3.45.0"),sQuery(id+"F0.wireOp",EDGE,"E9.7.45.0"),sQuery(id+"F0.wireOp",EDGE,"E9.11.45.0"),sQuery(id+"F0.wireOp",EDGE,"E9.14.45.0"),sQuery(id+"F0.wireOp",EDGE,"E9.1.46.0"),sQuery(id+"F0.wireOp",EDGE,"E9.3.46.0"),sQuery(id+"F0.wireOp",EDGE,"E9.7.46.0"),sQuery(id+"F0.wireOp",EDGE,"E9.11.46.0"),sQuery(id+"F0.wireOp",EDGE,"E9.14.46.0"),sQuery(id+"F0.wireOp",EDGE,"E9.1.47.0"),sQuery(id+"F0.wireOp",EDGE,"E9.3.47.0"),sQuery(id+"F0.wireOp",EDGE,"E9.7.47.0"),sQuery(id+"F0.wireOp",EDGE,"E9.11.47.0"),sQuery(id+"F0.wireOp",EDGE,"E9.14.47.0"),sQuery(id+"F0.wireOp",EDGE,"E9.1.48.0"),sQuery(id+"F0.wireOp",EDGE,"E9.3.48.0"),sQuery(id+"F0.wireOp",EDGE,"E9.7.48.0"),sQuery(id+"F0.wireOp",EDGE,"E9.11.48.0"),sQuery(id+"F0.wireOp",EDGE,"E9.14.48.0"),sQuery(id+"F0.wireOp",EDGE,"E9.1.49.0"),sQuery(id+"F0.wireOp",EDGE,"E9.3.49.0"),sQuery(id+"F0.wireOp",EDGE,"E9.7.49.0"),sQuery(id+"F0.wireOp",EDGE,"E9.11.49.0"),sQuery(id+"F0.wireOp",EDGE,"E9.14.49.0"),sQuery(id+"F0.wireOp",EDGE,"E9.1.50.0"),sQuery(id+"F0.wireOp",EDGE,"E9.3.50.0"),sQuery(id+"F0.wireOp",EDGE,"E9.7.50.0"),sQuery(id+"F0.wireOp",EDGE,"E9.11.50.0"),sQuery(id+"F0.wireOp",EDGE,"E9.14.50.0"),sQuery(id+"F0.wireOp",EDGE,"E9.1.51.0"),sQuery(id+"F0.wireOp",EDGE,"E9.3.51.0"),sQuery(id+"F0.wireOp",EDGE,"E9.7.51.0"),sQuery(id+"F0.wireOp",EDGE,"E9.11.51.0"),sQuery(id+"F0.wireOp",EDGE,"E9.14.51.0"),sQuery(id+"F0.wireOp",EDGE,"E9.1.52.0"),sQuery(id+"F0.wireOp",EDGE,"E9.3.52.0"),sQuery(id+"F0.wireOp",EDGE,"E9.7.52.0"),sQuery(id+"F0.wireOp",EDGE,"E9.11.52.0"),sQuery(id+"F0.wireOp",EDGE,"E9.14.52.0"),sQuery(id+"F0.wireOp",EDGE,"E9.1.53.0"),sQuery(id+"F0.wireOp",EDGE,"E9.3.53.0"),sQuery(id+"F0.wireOp",EDGE,"E9.7.53.0"),sQuery(id+"F0.wireOp",EDGE,"E9.11.53.0"),sQuery(id+"F0.wireOp",EDGE,"E9.14.53.0"),sQuery(id+"F0.wireOp",EDGE,"E9.1.54.0"),sQuery(id+"F0.wireOp",EDGE,"E9.3.54.0"),sQuery(id+"F0.wireOp",EDGE,"E9.7.54.0"),sQuery(id+"F0.wireOp",EDGE,"E9.11.54.0"),sQuery(id+"F0.wireOp",EDGE,"E9.14.54.0"),sQuery(id+"F0.wireOp",EDGE,"E9.1.55.0"),sQuery(id+"F0.wireOp",EDGE,"E9.3.55.0"),sQuery(id+"F0.wireOp",EDGE,"E9.7.55.0"),sQuery(id+"F0.wireOp",EDGE,"E9.11.55.0"),sQuery(id+"F0.wireOp",EDGE,"E9.14.55.0"),sQuery(id+"F0.wireOp",EDGE,"E9.1.56.0"),sQuery(id+"F0.wireOp",EDGE,"E9.3.56.0"),sQuery(id+"F0.wireOp",EDGE,"E9.7.56.0"),sQuery(id+"F0.wireOp",EDGE,"E9.11.56.0"),sQuery(id+"F0.wireOp",EDGE,"E9.14.56.0"),sQuery(id+"F0.wireOp",EDGE,"E9.1.57.0"),sQuery(id+"F0.wireOp",EDGE,"E9.3.57.0"),sQuery(id+"F0.wireOp",EDGE,"E9.7.57.0"),sQuery(id+"F0.wireOp",EDGE,"E9.11.57.0"),sQuery(id+"F0.wireOp",EDGE,"E9.14.57.0"),sQuery(id+"F0.wireOp",EDGE,"E9.1.58.0"),sQuery(id+"F0.wireOp",EDGE,"E9.3.58.0"),sQuery(id+"F0.wireOp",EDGE,"E9.7.58.0"),sQuery(id+"F0.wireOp",EDGE,"E9.11.58.0"),sQuery(id+"F0.wireOp",EDGE,"E9.14.58.0"),sQuery(id+"F0.wireOp",EDGE,"E9.1.59.0"),sQuery(id+"F0.wireOp",EDGE,"E9.3.59.0"),sQuery(id+"F0.wireOp",EDGE,"E9.7.59.0"),sQuery(id+"F0.wireOp",EDGE,"E9.11.59.0"),sQuery(id+"F0.wireOp",EDGE,"E9.14.59.0")])],"isStart":false})});
            var sketch = newSketch(context, id + "F7", { "sketchPlane" : qUnion([Q0])});
            skCircle(sketch, "E44", {"center": v(0, 0) * mm, "radius": 59 * mm});
            skCircle(sketch, "E45", {"center": v(0, 0) * mm, "radius": 64 * mm});
            skCircle(sketch, "E46", {"center": v(0, 0) * mm, "radius": 63 * mm});
            skCircle(sketch, "E47", {"center": v(0, 0) * mm, "radius": 10 * mm});
            skSolve(sketch);
        }
        {
            var Q0;
            Q0=qSketchRegion(id+"F7",true);
            var Q1;
            Q1=makeQuery(id+"F7.imprint","IMPRINT",FACE,{"disambiguationData":[TD([[makeQuery(id+"F7.imprint","IMPRINT",EDGE,{"derivedFrom":sQuery(id+"F7.wireOp",EDGE,"E44")}),1.0]])]});
            extrude(context, id + "F8", {"entities" : qUnion([Q0, Q1]), "operationType" : NewBodyOperationType.REMOVE, "oppositeDirection" : true, "depth" : 1 * mm, "offsetDistance" : 25 * mm});
        }
        {
            var Q0;
            Q0=makeQuery(id+"F8.boolean.opBoolean","COPY",EDGE,{"derivedFrom":makeQuery(id+"F8.opExtrude","CAP_EDGE",EDGE,{"disambiguationData":[OSD([sQuery(id+"F0.wireOp",EDGE,"E0"),sQuery(id+"F0.wireOp",EDGE,"E1"),sQuery(id+"F0.wireOp",EDGE,"E3"),sQuery(id+"F0.wireOp",EDGE,"E4"),sQuery(id+"F0.wireOp",EDGE,"E5"),sQuery(id+"F0.wireOp",EDGE,"E6.trimOffspring"),sQuery(id+"F0.wireOp",EDGE,"E7"),sQuery(id+"F0.wireOp",EDGE,"E8.1.0"),sQuery(id+"F0.wireOp",EDGE,"E8.1.1"),sQuery(id+"F0.wireOp",EDGE,"E8.1.2"),sQuery(id+"F0.wireOp",EDGE,"E8.1.3"),sQuery(id+"F0.wireOp",EDGE,"E8.1.4"),sQuery(id+"F0.wireOp",EDGE,"E8.2.0"),sQuery(id+"F0.wireOp",EDGE,"E8.2.1"),sQuery(id+"F0.wireOp",EDGE,"E8.2.2"),sQuery(id+"F0.wireOp",EDGE,"E8.2.3"),sQuery(id+"F0.wireOp",EDGE,"E8.2.4"),sQuery(id+"F0.wireOp",EDGE,"E9.1.3.0"),sQuery(id+"F0.wireOp",EDGE,"E9.3.3.0"),sQuery(id+"F0.wireOp",EDGE,"E9.7.3.0"),sQuery(id+"F0.wireOp",EDGE,"E9.11.3.0"),sQuery(id+"F0.wireOp",EDGE,"E9.14.3.0"),sQuery(id+"F0.wireOp",EDGE,"E9.1.4.0"),sQuery(id+"F0.wireOp",EDGE,"E9.3.4.0"),sQuery(id+"F0.wireOp",EDGE,"E9.7.4.0"),sQuery(id+"F0.wireOp",EDGE,"E9.11.4.0"),sQuery(id+"F0.wireOp",EDGE,"E9.14.4.0"),sQuery(id+"F0.wireOp",EDGE,"E9.1.5.0"),sQuery(id+"F0.wireOp",EDGE,"E9.3.5.0"),sQuery(id+"F0.wireOp",EDGE,"E9.7.5.0"),sQuery(id+"F0.wireOp",EDGE,"E9.11.5.0"),sQuery(id+"F0.wireOp",EDGE,"E9.14.5.0"),sQuery(id+"F0.wireOp",EDGE,"E9.1.6.0"),sQuery(id+"F0.wireOp",EDGE,"E9.3.6.0"),sQuery(id+"F0.wireOp",EDGE,"E9.7.6.0"),sQuery(id+"F0.wireOp",EDGE,"E9.11.6.0"),sQuery(id+"F0.wireOp",EDGE,"E9.14.6.0"),sQuery(id+"F0.wireOp",EDGE,"E9.1.7.0"),sQuery(id+"F0.wireOp",EDGE,"E9.3.7.0"),sQuery(id+"F0.wireOp",EDGE,"E9.7.7.0"),sQuery(id+"F0.wireOp",EDGE,"E9.11.7.0"),sQuery(id+"F0.wireOp",EDGE,"E9.14.7.0"),sQuery(id+"F0.wireOp",EDGE,"E9.1.8.0"),sQuery(id+"F0.wireOp",EDGE,"E9.3.8.0"),sQuery(id+"F0.wireOp",EDGE,"E9.7.8.0"),sQuery(id+"F0.wireOp",EDGE,"E9.11.8.0"),sQuery(id+"F0.wireOp",EDGE,"E9.14.8.0"),sQuery(id+"F0.wireOp",EDGE,"E9.1.9.0"),sQuery(id+"F0.wireOp",EDGE,"E9.3.9.0"),sQuery(id+"F0.wireOp",EDGE,"E9.7.9.0"),sQuery(id+"F0.wireOp",EDGE,"E9.11.9.0"),sQuery(id+"F0.wireOp",EDGE,"E9.14.9.0"),sQuery(id+"F0.wireOp",EDGE,"E9.1.10.0"),sQuery(id+"F0.wireOp",EDGE,"E9.3.10.0"),sQuery(id+"F0.wireOp",EDGE,"E9.7.10.0"),sQuery(id+"F0.wireOp",EDGE,"E9.11.10.0"),sQuery(id+"F0.wireOp",EDGE,"E9.14.10.0"),sQuery(id+"F0.wireOp",EDGE,"E9.1.11.0"),sQuery(id+"F0.wireOp",EDGE,"E9.3.11.0"),sQuery(id+"F0.wireOp",EDGE,"E9.7.11.0"),sQuery(id+"F0.wireOp",EDGE,"E9.11.11.0"),sQuery(id+"F0.wireOp",EDGE,"E9.14.11.0"),sQuery(id+"F0.wireOp",EDGE,"E9.1.12.0"),sQuery(id+"F0.wireOp",EDGE,"E9.3.12.0"),sQuery(id+"F0.wireOp",EDGE,"E9.7.12.0"),sQuery(id+"F0.wireOp",EDGE,"E9.11.12.0"),sQuery(id+"F0.wireOp",EDGE,"E9.14.12.0"),sQuery(id+"F0.wireOp",EDGE,"E9.1.13.0"),sQuery(id+"F0.wireOp",EDGE,"E9.3.13.0"),sQuery(id+"F0.wireOp",EDGE,"E9.7.13.0"),sQuery(id+"F0.wireOp",EDGE,"E9.11.13.0"),sQuery(id+"F0.wireOp",EDGE,"E9.14.13.0"),sQuery(id+"F0.wireOp",EDGE,"E9.1.14.0"),sQuery(id+"F0.wireOp",EDGE,"E9.3.14.0"),sQuery(id+"F0.wireOp",EDGE,"E9.7.14.0"),sQuery(id+"F0.wireOp",EDGE,"E9.11.14.0"),sQuery(id+"F0.wireOp",EDGE,"E9.14.14.0"),sQuery(id+"F0.wireOp",EDGE,"E9.1.15.0"),sQuery(id+"F0.wireOp",EDGE,"E9.3.15.0"),sQuery(id+"F0.wireOp",EDGE,"E9.7.15.0"),sQuery(id+"F0.wireOp",EDGE,"E9.11.15.0"),sQuery(id+"F0.wireOp",EDGE,"E9.14.15.0"),sQuery(id+"F0.wireOp",EDGE,"E9.1.16.0"),sQuery(id+"F0.wireOp",EDGE,"E9.3.16.0"),sQuery(id+"F0.wireOp",EDGE,"E9.7.16.0"),sQuery(id+"F0.wireOp",EDGE,"E9.11.16.0"),sQuery(id+"F0.wireOp",EDGE,"E9.14.16.0"),sQuery(id+"F0.wireOp",EDGE,"E9.1.17.0"),sQuery(id+"F0.wireOp",EDGE,"E9.3.17.0"),sQuery(id+"F0.wireOp",EDGE,"E9.7.17.0"),sQuery(id+"F0.wireOp",EDGE,"E9.11.17.0"),sQuery(id+"F0.wireOp",EDGE,"E9.14.17.0"),sQuery(id+"F0.wireOp",EDGE,"E9.1.18.0"),sQuery(id+"F0.wireOp",EDGE,"E9.3.18.0"),sQuery(id+"F0.wireOp",EDGE,"E9.7.18.0"),sQuery(id+"F0.wireOp",EDGE,"E9.11.18.0"),sQuery(id+"F0.wireOp",EDGE,"E9.14.18.0"),sQuery(id+"F0.wireOp",EDGE,"E9.1.19.0"),sQuery(id+"F0.wireOp",EDGE,"E9.3.19.0"),sQuery(id+"F0.wireOp",EDGE,"E9.7.19.0"),sQuery(id+"F0.wireOp",EDGE,"E9.11.19.0"),sQuery(id+"F0.wireOp",EDGE,"E9.14.19.0"),sQuery(id+"F0.wireOp",EDGE,"E9.1.20.0"),sQuery(id+"F0.wireOp",EDGE,"E9.3.20.0"),sQuery(id+"F0.wireOp",EDGE,"E9.7.20.0"),sQuery(id+"F0.wireOp",EDGE,"E9.11.20.0"),sQuery(id+"F0.wireOp",EDGE,"E9.14.20.0"),sQuery(id+"F0.wireOp",EDGE,"E9.1.21.0"),sQuery(id+"F0.wireOp",EDGE,"E9.3.21.0"),sQuery(id+"F0.wireOp",EDGE,"E9.7.21.0"),sQuery(id+"F0.wireOp",EDGE,"E9.11.21.0"),sQuery(id+"F0.wireOp",EDGE,"E9.14.21.0"),sQuery(id+"F0.wireOp",EDGE,"E9.1.22.0"),sQuery(id+"F0.wireOp",EDGE,"E9.3.22.0"),sQuery(id+"F0.wireOp",EDGE,"E9.7.22.0"),sQuery(id+"F0.wireOp",EDGE,"E9.11.22.0"),sQuery(id+"F0.wireOp",EDGE,"E9.14.22.0"),sQuery(id+"F0.wireOp",EDGE,"E9.1.23.0"),sQuery(id+"F0.wireOp",EDGE,"E9.3.23.0"),sQuery(id+"F0.wireOp",EDGE,"E9.7.23.0"),sQuery(id+"F0.wireOp",EDGE,"E9.11.23.0"),sQuery(id+"F0.wireOp",EDGE,"E9.14.23.0"),sQuery(id+"F0.wireOp",EDGE,"E9.1.24.0"),sQuery(id+"F0.wireOp",EDGE,"E9.3.24.0"),sQuery(id+"F0.wireOp",EDGE,"E9.7.24.0"),sQuery(id+"F0.wireOp",EDGE,"E9.11.24.0"),sQuery(id+"F0.wireOp",EDGE,"E9.14.24.0"),sQuery(id+"F0.wireOp",EDGE,"E9.1.25.0"),sQuery(id+"F0.wireOp",EDGE,"E9.3.25.0"),sQuery(id+"F0.wireOp",EDGE,"E9.7.25.0"),sQuery(id+"F0.wireOp",EDGE,"E9.11.25.0"),sQuery(id+"F0.wireOp",EDGE,"E9.14.25.0"),sQuery(id+"F0.wireOp",EDGE,"E9.1.26.0"),sQuery(id+"F0.wireOp",EDGE,"E9.3.26.0"),sQuery(id+"F0.wireOp",EDGE,"E9.7.26.0"),sQuery(id+"F0.wireOp",EDGE,"E9.11.26.0"),sQuery(id+"F0.wireOp",EDGE,"E9.14.26.0"),sQuery(id+"F0.wireOp",EDGE,"E9.1.27.0"),sQuery(id+"F0.wireOp",EDGE,"E9.3.27.0"),sQuery(id+"F0.wireOp",EDGE,"E9.7.27.0"),sQuery(id+"F0.wireOp",EDGE,"E9.11.27.0"),sQuery(id+"F0.wireOp",EDGE,"E9.14.27.0"),sQuery(id+"F0.wireOp",EDGE,"E9.1.28.0"),sQuery(id+"F0.wireOp",EDGE,"E9.3.28.0"),sQuery(id+"F0.wireOp",EDGE,"E9.7.28.0"),sQuery(id+"F0.wireOp",EDGE,"E9.11.28.0"),sQuery(id+"F0.wireOp",EDGE,"E9.14.28.0"),sQuery(id+"F0.wireOp",EDGE,"E9.1.29.0"),sQuery(id+"F0.wireOp",EDGE,"E9.3.29.0"),sQuery(id+"F0.wireOp",EDGE,"E9.7.29.0"),sQuery(id+"F0.wireOp",EDGE,"E9.11.29.0"),sQuery(id+"F0.wireOp",EDGE,"E9.14.29.0"),sQuery(id+"F0.wireOp",EDGE,"E9.1.30.0"),sQuery(id+"F0.wireOp",EDGE,"E9.3.30.0"),sQuery(id+"F0.wireOp",EDGE,"E9.7.30.0"),sQuery(id+"F0.wireOp",EDGE,"E9.11.30.0"),sQuery(id+"F0.wireOp",EDGE,"E9.14.30.0"),sQuery(id+"F0.wireOp",EDGE,"E9.1.31.0"),sQuery(id+"F0.wireOp",EDGE,"E9.3.31.0"),sQuery(id+"F0.wireOp",EDGE,"E9.7.31.0"),sQuery(id+"F0.wireOp",EDGE,"E9.11.31.0"),sQuery(id+"F0.wireOp",EDGE,"E9.14.31.0"),sQuery(id+"F0.wireOp",EDGE,"E9.1.32.0"),sQuery(id+"F0.wireOp",EDGE,"E9.3.32.0"),sQuery(id+"F0.wireOp",EDGE,"E9.7.32.0"),sQuery(id+"F0.wireOp",EDGE,"E9.11.32.0"),sQuery(id+"F0.wireOp",EDGE,"E9.14.32.0"),sQuery(id+"F0.wireOp",EDGE,"E9.1.33.0"),sQuery(id+"F0.wireOp",EDGE,"E9.3.33.0"),sQuery(id+"F0.wireOp",EDGE,"E9.7.33.0"),sQuery(id+"F0.wireOp",EDGE,"E9.11.33.0"),sQuery(id+"F0.wireOp",EDGE,"E9.14.33.0"),sQuery(id+"F0.wireOp",EDGE,"E9.1.34.0"),sQuery(id+"F0.wireOp",EDGE,"E9.3.34.0"),sQuery(id+"F0.wireOp",EDGE,"E9.7.34.0"),sQuery(id+"F0.wireOp",EDGE,"E9.11.34.0"),sQuery(id+"F0.wireOp",EDGE,"E9.14.34.0"),sQuery(id+"F0.wireOp",EDGE,"E9.1.35.0"),sQuery(id+"F0.wireOp",EDGE,"E9.3.35.0"),sQuery(id+"F0.wireOp",EDGE,"E9.7.35.0"),sQuery(id+"F0.wireOp",EDGE,"E9.11.35.0"),sQuery(id+"F0.wireOp",EDGE,"E9.14.35.0"),sQuery(id+"F0.wireOp",EDGE,"E9.1.36.0"),sQuery(id+"F0.wireOp",EDGE,"E9.3.36.0"),sQuery(id+"F0.wireOp",EDGE,"E9.7.36.0"),sQuery(id+"F0.wireOp",EDGE,"E9.11.36.0"),sQuery(id+"F0.wireOp",EDGE,"E9.14.36.0"),sQuery(id+"F0.wireOp",EDGE,"E9.1.37.0"),sQuery(id+"F0.wireOp",EDGE,"E9.3.37.0"),sQuery(id+"F0.wireOp",EDGE,"E9.7.37.0"),sQuery(id+"F0.wireOp",EDGE,"E9.11.37.0"),sQuery(id+"F0.wireOp",EDGE,"E9.14.37.0"),sQuery(id+"F0.wireOp",EDGE,"E9.1.38.0"),sQuery(id+"F0.wireOp",EDGE,"E9.3.38.0"),sQuery(id+"F0.wireOp",EDGE,"E9.7.38.0"),sQuery(id+"F0.wireOp",EDGE,"E9.11.38.0"),sQuery(id+"F0.wireOp",EDGE,"E9.14.38.0"),sQuery(id+"F0.wireOp",EDGE,"E9.1.39.0"),sQuery(id+"F0.wireOp",EDGE,"E9.3.39.0"),sQuery(id+"F0.wireOp",EDGE,"E9.7.39.0"),sQuery(id+"F0.wireOp",EDGE,"E9.11.39.0"),sQuery(id+"F0.wireOp",EDGE,"E9.14.39.0"),sQuery(id+"F0.wireOp",EDGE,"E9.1.40.0"),sQuery(id+"F0.wireOp",EDGE,"E9.3.40.0"),sQuery(id+"F0.wireOp",EDGE,"E9.7.40.0"),sQuery(id+"F0.wireOp",EDGE,"E9.11.40.0"),sQuery(id+"F0.wireOp",EDGE,"E9.14.40.0"),sQuery(id+"F0.wireOp",EDGE,"E9.1.41.0"),sQuery(id+"F0.wireOp",EDGE,"E9.3.41.0"),sQuery(id+"F0.wireOp",EDGE,"E9.7.41.0"),sQuery(id+"F0.wireOp",EDGE,"E9.11.41.0"),sQuery(id+"F0.wireOp",EDGE,"E9.14.41.0"),sQuery(id+"F0.wireOp",EDGE,"E9.1.42.0"),sQuery(id+"F0.wireOp",EDGE,"E9.3.42.0"),sQuery(id+"F0.wireOp",EDGE,"E9.7.42.0"),sQuery(id+"F0.wireOp",EDGE,"E9.11.42.0"),sQuery(id+"F0.wireOp",EDGE,"E9.14.42.0"),sQuery(id+"F0.wireOp",EDGE,"E9.1.43.0"),sQuery(id+"F0.wireOp",EDGE,"E9.3.43.0"),sQuery(id+"F0.wireOp",EDGE,"E9.7.43.0"),sQuery(id+"F0.wireOp",EDGE,"E9.11.43.0"),sQuery(id+"F0.wireOp",EDGE,"E9.14.43.0"),sQuery(id+"F0.wireOp",EDGE,"E9.1.44.0"),sQuery(id+"F0.wireOp",EDGE,"E9.3.44.0"),sQuery(id+"F0.wireOp",EDGE,"E9.7.44.0"),sQuery(id+"F0.wireOp",EDGE,"E9.11.44.0"),sQuery(id+"F0.wireOp",EDGE,"E9.14.44.0"),sQuery(id+"F0.wireOp",EDGE,"E9.1.45.0"),sQuery(id+"F0.wireOp",EDGE,"E9.3.45.0"),sQuery(id+"F0.wireOp",EDGE,"E9.7.45.0"),sQuery(id+"F0.wireOp",EDGE,"E9.11.45.0"),sQuery(id+"F0.wireOp",EDGE,"E9.14.45.0"),sQuery(id+"F0.wireOp",EDGE,"E9.1.46.0"),sQuery(id+"F0.wireOp",EDGE,"E9.3.46.0"),sQuery(id+"F0.wireOp",EDGE,"E9.7.46.0"),sQuery(id+"F0.wireOp",EDGE,"E9.11.46.0"),sQuery(id+"F0.wireOp",EDGE,"E9.14.46.0"),sQuery(id+"F0.wireOp",EDGE,"E9.1.47.0"),sQuery(id+"F0.wireOp",EDGE,"E9.3.47.0"),sQuery(id+"F0.wireOp",EDGE,"E9.7.47.0"),sQuery(id+"F0.wireOp",EDGE,"E9.11.47.0"),sQuery(id+"F0.wireOp",EDGE,"E9.14.47.0"),sQuery(id+"F0.wireOp",EDGE,"E9.1.48.0"),sQuery(id+"F0.wireOp",EDGE,"E9.3.48.0"),sQuery(id+"F0.wireOp",EDGE,"E9.7.48.0"),sQuery(id+"F0.wireOp",EDGE,"E9.11.48.0"),sQuery(id+"F0.wireOp",EDGE,"E9.14.48.0"),sQuery(id+"F0.wireOp",EDGE,"E9.1.49.0"),sQuery(id+"F0.wireOp",EDGE,"E9.3.49.0"),sQuery(id+"F0.wireOp",EDGE,"E9.7.49.0"),sQuery(id+"F0.wireOp",EDGE,"E9.11.49.0"),sQuery(id+"F0.wireOp",EDGE,"E9.14.49.0"),sQuery(id+"F0.wireOp",EDGE,"E9.1.50.0"),sQuery(id+"F0.wireOp",EDGE,"E9.3.50.0"),sQuery(id+"F0.wireOp",EDGE,"E9.7.50.0"),sQuery(id+"F0.wireOp",EDGE,"E9.11.50.0"),sQuery(id+"F0.wireOp",EDGE,"E9.14.50.0"),sQuery(id+"F0.wireOp",EDGE,"E9.1.51.0"),sQuery(id+"F0.wireOp",EDGE,"E9.3.51.0"),sQuery(id+"F0.wireOp",EDGE,"E9.7.51.0"),sQuery(id+"F0.wireOp",EDGE,"E9.11.51.0"),sQuery(id+"F0.wireOp",EDGE,"E9.14.51.0"),sQuery(id+"F0.wireOp",EDGE,"E9.1.52.0"),sQuery(id+"F0.wireOp",EDGE,"E9.3.52.0"),sQuery(id+"F0.wireOp",EDGE,"E9.7.52.0"),sQuery(id+"F0.wireOp",EDGE,"E9.11.52.0"),sQuery(id+"F0.wireOp",EDGE,"E9.14.52.0"),sQuery(id+"F0.wireOp",EDGE,"E9.1.53.0"),sQuery(id+"F0.wireOp",EDGE,"E9.3.53.0"),sQuery(id+"F0.wireOp",EDGE,"E9.7.53.0"),sQuery(id+"F0.wireOp",EDGE,"E9.11.53.0"),sQuery(id+"F0.wireOp",EDGE,"E9.14.53.0"),sQuery(id+"F0.wireOp",EDGE,"E9.1.54.0"),sQuery(id+"F0.wireOp",EDGE,"E9.3.54.0"),sQuery(id+"F0.wireOp",EDGE,"E9.7.54.0"),sQuery(id+"F0.wireOp",EDGE,"E9.11.54.0"),sQuery(id+"F0.wireOp",EDGE,"E9.14.54.0"),sQuery(id+"F0.wireOp",EDGE,"E9.1.55.0"),sQuery(id+"F0.wireOp",EDGE,"E9.3.55.0"),sQuery(id+"F0.wireOp",EDGE,"E9.7.55.0"),sQuery(id+"F0.wireOp",EDGE,"E9.11.55.0"),sQuery(id+"F0.wireOp",EDGE,"E9.14.55.0"),sQuery(id+"F0.wireOp",EDGE,"E9.1.56.0"),sQuery(id+"F0.wireOp",EDGE,"E9.3.56.0"),sQuery(id+"F0.wireOp",EDGE,"E9.7.56.0"),sQuery(id+"F0.wireOp",EDGE,"E9.11.56.0"),sQuery(id+"F0.wireOp",EDGE,"E9.14.56.0"),sQuery(id+"F0.wireOp",EDGE,"E9.1.57.0"),sQuery(id+"F0.wireOp",EDGE,"E9.3.57.0"),sQuery(id+"F0.wireOp",EDGE,"E9.7.57.0"),sQuery(id+"F0.wireOp",EDGE,"E9.11.57.0"),sQuery(id+"F0.wireOp",EDGE,"E9.14.57.0"),sQuery(id+"F0.wireOp",EDGE,"E9.1.58.0"),sQuery(id+"F0.wireOp",EDGE,"E9.3.58.0"),sQuery(id+"F0.wireOp",EDGE,"E9.7.58.0"),sQuery(id+"F0.wireOp",EDGE,"E9.11.58.0"),sQuery(id+"F0.wireOp",EDGE,"E9.14.58.0"),sQuery(id+"F0.wireOp",EDGE,"E9.1.59.0"),sQuery(id+"F0.wireOp",EDGE,"E9.3.59.0"),sQuery(id+"F0.wireOp",EDGE,"E9.7.59.0"),sQuery(id+"F0.wireOp",EDGE,"E9.11.59.0"),sQuery(id+"F0.wireOp",EDGE,"E9.14.59.0"),sQuery(id+"F2.wireOp",EDGE,"E19")])],"isStart":false})});
            var Q1;
            Q1=makeQuery(id+"F8.boolean.opBoolean","COPY",EDGE,{"derivedFrom":makeQuery(id+"F8.opExtrude","CAP_EDGE",EDGE,{"disambiguationData":[OSD([sQuery(id+"F0.wireOp",EDGE,"E0"),sQuery(id+"F0.wireOp",EDGE,"E1"),sQuery(id+"F0.wireOp",EDGE,"E3"),sQuery(id+"F0.wireOp",EDGE,"E4"),sQuery(id+"F0.wireOp",EDGE,"E5"),sQuery(id+"F0.wireOp",EDGE,"E6.trimOffspring"),sQuery(id+"F0.wireOp",EDGE,"E7"),sQuery(id+"F0.wireOp",EDGE,"E8.1.0"),sQuery(id+"F0.wireOp",EDGE,"E8.1.1"),sQuery(id+"F0.wireOp",EDGE,"E8.1.2"),sQuery(id+"F0.wireOp",EDGE,"E8.1.3"),sQuery(id+"F0.wireOp",EDGE,"E8.1.4"),sQuery(id+"F0.wireOp",EDGE,"E8.2.0"),sQuery(id+"F0.wireOp",EDGE,"E8.2.1"),sQuery(id+"F0.wireOp",EDGE,"E8.2.2"),sQuery(id+"F0.wireOp",EDGE,"E8.2.3"),sQuery(id+"F0.wireOp",EDGE,"E8.2.4"),sQuery(id+"F0.wireOp",EDGE,"E9.1.3.0"),sQuery(id+"F0.wireOp",EDGE,"E9.3.3.0"),sQuery(id+"F0.wireOp",EDGE,"E9.7.3.0"),sQuery(id+"F0.wireOp",EDGE,"E9.11.3.0"),sQuery(id+"F0.wireOp",EDGE,"E9.14.3.0"),sQuery(id+"F0.wireOp",EDGE,"E9.1.4.0"),sQuery(id+"F0.wireOp",EDGE,"E9.3.4.0"),sQuery(id+"F0.wireOp",EDGE,"E9.7.4.0"),sQuery(id+"F0.wireOp",EDGE,"E9.11.4.0"),sQuery(id+"F0.wireOp",EDGE,"E9.14.4.0"),sQuery(id+"F0.wireOp",EDGE,"E9.1.5.0"),sQuery(id+"F0.wireOp",EDGE,"E9.3.5.0"),sQuery(id+"F0.wireOp",EDGE,"E9.7.5.0"),sQuery(id+"F0.wireOp",EDGE,"E9.11.5.0"),sQuery(id+"F0.wireOp",EDGE,"E9.14.5.0"),sQuery(id+"F0.wireOp",EDGE,"E9.1.6.0"),sQuery(id+"F0.wireOp",EDGE,"E9.3.6.0"),sQuery(id+"F0.wireOp",EDGE,"E9.7.6.0"),sQuery(id+"F0.wireOp",EDGE,"E9.11.6.0"),sQuery(id+"F0.wireOp",EDGE,"E9.14.6.0"),sQuery(id+"F0.wireOp",EDGE,"E9.1.7.0"),sQuery(id+"F0.wireOp",EDGE,"E9.3.7.0"),sQuery(id+"F0.wireOp",EDGE,"E9.7.7.0"),sQuery(id+"F0.wireOp",EDGE,"E9.11.7.0"),sQuery(id+"F0.wireOp",EDGE,"E9.14.7.0"),sQuery(id+"F0.wireOp",EDGE,"E9.1.8.0"),sQuery(id+"F0.wireOp",EDGE,"E9.3.8.0"),sQuery(id+"F0.wireOp",EDGE,"E9.7.8.0"),sQuery(id+"F0.wireOp",EDGE,"E9.11.8.0"),sQuery(id+"F0.wireOp",EDGE,"E9.14.8.0"),sQuery(id+"F0.wireOp",EDGE,"E9.1.9.0"),sQuery(id+"F0.wireOp",EDGE,"E9.3.9.0"),sQuery(id+"F0.wireOp",EDGE,"E9.7.9.0"),sQuery(id+"F0.wireOp",EDGE,"E9.11.9.0"),sQuery(id+"F0.wireOp",EDGE,"E9.14.9.0"),sQuery(id+"F0.wireOp",EDGE,"E9.1.10.0"),sQuery(id+"F0.wireOp",EDGE,"E9.3.10.0"),sQuery(id+"F0.wireOp",EDGE,"E9.7.10.0"),sQuery(id+"F0.wireOp",EDGE,"E9.11.10.0"),sQuery(id+"F0.wireOp",EDGE,"E9.14.10.0"),sQuery(id+"F0.wireOp",EDGE,"E9.1.11.0"),sQuery(id+"F0.wireOp",EDGE,"E9.3.11.0"),sQuery(id+"F0.wireOp",EDGE,"E9.7.11.0"),sQuery(id+"F0.wireOp",EDGE,"E9.11.11.0"),sQuery(id+"F0.wireOp",EDGE,"E9.14.11.0"),sQuery(id+"F0.wireOp",EDGE,"E9.1.12.0"),sQuery(id+"F0.wireOp",EDGE,"E9.3.12.0"),sQuery(id+"F0.wireOp",EDGE,"E9.7.12.0"),sQuery(id+"F0.wireOp",EDGE,"E9.11.12.0"),sQuery(id+"F0.wireOp",EDGE,"E9.14.12.0"),sQuery(id+"F0.wireOp",EDGE,"E9.1.13.0"),sQuery(id+"F0.wireOp",EDGE,"E9.3.13.0"),sQuery(id+"F0.wireOp",EDGE,"E9.7.13.0"),sQuery(id+"F0.wireOp",EDGE,"E9.11.13.0"),sQuery(id+"F0.wireOp",EDGE,"E9.14.13.0"),sQuery(id+"F0.wireOp",EDGE,"E9.1.14.0"),sQuery(id+"F0.wireOp",EDGE,"E9.3.14.0"),sQuery(id+"F0.wireOp",EDGE,"E9.7.14.0"),sQuery(id+"F0.wireOp",EDGE,"E9.11.14.0"),sQuery(id+"F0.wireOp",EDGE,"E9.14.14.0"),sQuery(id+"F0.wireOp",EDGE,"E9.1.15.0"),sQuery(id+"F0.wireOp",EDGE,"E9.3.15.0"),sQuery(id+"F0.wireOp",EDGE,"E9.7.15.0"),sQuery(id+"F0.wireOp",EDGE,"E9.11.15.0"),sQuery(id+"F0.wireOp",EDGE,"E9.14.15.0"),sQuery(id+"F0.wireOp",EDGE,"E9.1.16.0"),sQuery(id+"F0.wireOp",EDGE,"E9.3.16.0"),sQuery(id+"F0.wireOp",EDGE,"E9.7.16.0"),sQuery(id+"F0.wireOp",EDGE,"E9.11.16.0"),sQuery(id+"F0.wireOp",EDGE,"E9.14.16.0"),sQuery(id+"F0.wireOp",EDGE,"E9.1.17.0"),sQuery(id+"F0.wireOp",EDGE,"E9.3.17.0"),sQuery(id+"F0.wireOp",EDGE,"E9.7.17.0"),sQuery(id+"F0.wireOp",EDGE,"E9.11.17.0"),sQuery(id+"F0.wireOp",EDGE,"E9.14.17.0"),sQuery(id+"F0.wireOp",EDGE,"E9.1.18.0"),sQuery(id+"F0.wireOp",EDGE,"E9.3.18.0"),sQuery(id+"F0.wireOp",EDGE,"E9.7.18.0"),sQuery(id+"F0.wireOp",EDGE,"E9.11.18.0"),sQuery(id+"F0.wireOp",EDGE,"E9.14.18.0"),sQuery(id+"F0.wireOp",EDGE,"E9.1.19.0"),sQuery(id+"F0.wireOp",EDGE,"E9.3.19.0"),sQuery(id+"F0.wireOp",EDGE,"E9.7.19.0"),sQuery(id+"F0.wireOp",EDGE,"E9.11.19.0"),sQuery(id+"F0.wireOp",EDGE,"E9.14.19.0"),sQuery(id+"F0.wireOp",EDGE,"E9.1.20.0"),sQuery(id+"F0.wireOp",EDGE,"E9.3.20.0"),sQuery(id+"F0.wireOp",EDGE,"E9.7.20.0"),sQuery(id+"F0.wireOp",EDGE,"E9.11.20.0"),sQuery(id+"F0.wireOp",EDGE,"E9.14.20.0"),sQuery(id+"F0.wireOp",EDGE,"E9.1.21.0"),sQuery(id+"F0.wireOp",EDGE,"E9.3.21.0"),sQuery(id+"F0.wireOp",EDGE,"E9.7.21.0"),sQuery(id+"F0.wireOp",EDGE,"E9.11.21.0"),sQuery(id+"F0.wireOp",EDGE,"E9.14.21.0"),sQuery(id+"F0.wireOp",EDGE,"E9.1.22.0"),sQuery(id+"F0.wireOp",EDGE,"E9.3.22.0"),sQuery(id+"F0.wireOp",EDGE,"E9.7.22.0"),sQuery(id+"F0.wireOp",EDGE,"E9.11.22.0"),sQuery(id+"F0.wireOp",EDGE,"E9.14.22.0"),sQuery(id+"F0.wireOp",EDGE,"E9.1.23.0"),sQuery(id+"F0.wireOp",EDGE,"E9.3.23.0"),sQuery(id+"F0.wireOp",EDGE,"E9.7.23.0"),sQuery(id+"F0.wireOp",EDGE,"E9.11.23.0"),sQuery(id+"F0.wireOp",EDGE,"E9.14.23.0"),sQuery(id+"F0.wireOp",EDGE,"E9.1.24.0"),sQuery(id+"F0.wireOp",EDGE,"E9.3.24.0"),sQuery(id+"F0.wireOp",EDGE,"E9.7.24.0"),sQuery(id+"F0.wireOp",EDGE,"E9.11.24.0"),sQuery(id+"F0.wireOp",EDGE,"E9.14.24.0"),sQuery(id+"F0.wireOp",EDGE,"E9.1.25.0"),sQuery(id+"F0.wireOp",EDGE,"E9.3.25.0"),sQuery(id+"F0.wireOp",EDGE,"E9.7.25.0"),sQuery(id+"F0.wireOp",EDGE,"E9.11.25.0"),sQuery(id+"F0.wireOp",EDGE,"E9.14.25.0"),sQuery(id+"F0.wireOp",EDGE,"E9.1.26.0"),sQuery(id+"F0.wireOp",EDGE,"E9.3.26.0"),sQuery(id+"F0.wireOp",EDGE,"E9.7.26.0"),sQuery(id+"F0.wireOp",EDGE,"E9.11.26.0"),sQuery(id+"F0.wireOp",EDGE,"E9.14.26.0"),sQuery(id+"F0.wireOp",EDGE,"E9.1.27.0"),sQuery(id+"F0.wireOp",EDGE,"E9.3.27.0"),sQuery(id+"F0.wireOp",EDGE,"E9.7.27.0"),sQuery(id+"F0.wireOp",EDGE,"E9.11.27.0"),sQuery(id+"F0.wireOp",EDGE,"E9.14.27.0"),sQuery(id+"F0.wireOp",EDGE,"E9.1.28.0"),sQuery(id+"F0.wireOp",EDGE,"E9.3.28.0"),sQuery(id+"F0.wireOp",EDGE,"E9.7.28.0"),sQuery(id+"F0.wireOp",EDGE,"E9.11.28.0"),sQuery(id+"F0.wireOp",EDGE,"E9.14.28.0"),sQuery(id+"F0.wireOp",EDGE,"E9.1.29.0"),sQuery(id+"F0.wireOp",EDGE,"E9.3.29.0"),sQuery(id+"F0.wireOp",EDGE,"E9.7.29.0"),sQuery(id+"F0.wireOp",EDGE,"E9.11.29.0"),sQuery(id+"F0.wireOp",EDGE,"E9.14.29.0"),sQuery(id+"F0.wireOp",EDGE,"E9.1.30.0"),sQuery(id+"F0.wireOp",EDGE,"E9.3.30.0"),sQuery(id+"F0.wireOp",EDGE,"E9.7.30.0"),sQuery(id+"F0.wireOp",EDGE,"E9.11.30.0"),sQuery(id+"F0.wireOp",EDGE,"E9.14.30.0"),sQuery(id+"F0.wireOp",EDGE,"E9.1.31.0"),sQuery(id+"F0.wireOp",EDGE,"E9.3.31.0"),sQuery(id+"F0.wireOp",EDGE,"E9.7.31.0"),sQuery(id+"F0.wireOp",EDGE,"E9.11.31.0"),sQuery(id+"F0.wireOp",EDGE,"E9.14.31.0"),sQuery(id+"F0.wireOp",EDGE,"E9.1.32.0"),sQuery(id+"F0.wireOp",EDGE,"E9.3.32.0"),sQuery(id+"F0.wireOp",EDGE,"E9.7.32.0"),sQuery(id+"F0.wireOp",EDGE,"E9.11.32.0"),sQuery(id+"F0.wireOp",EDGE,"E9.14.32.0"),sQuery(id+"F0.wireOp",EDGE,"E9.1.33.0"),sQuery(id+"F0.wireOp",EDGE,"E9.3.33.0"),sQuery(id+"F0.wireOp",EDGE,"E9.7.33.0"),sQuery(id+"F0.wireOp",EDGE,"E9.11.33.0"),sQuery(id+"F0.wireOp",EDGE,"E9.14.33.0"),sQuery(id+"F0.wireOp",EDGE,"E9.1.34.0"),sQuery(id+"F0.wireOp",EDGE,"E9.3.34.0"),sQuery(id+"F0.wireOp",EDGE,"E9.7.34.0"),sQuery(id+"F0.wireOp",EDGE,"E9.11.34.0"),sQuery(id+"F0.wireOp",EDGE,"E9.14.34.0"),sQuery(id+"F0.wireOp",EDGE,"E9.1.35.0"),sQuery(id+"F0.wireOp",EDGE,"E9.3.35.0"),sQuery(id+"F0.wireOp",EDGE,"E9.7.35.0"),sQuery(id+"F0.wireOp",EDGE,"E9.11.35.0"),sQuery(id+"F0.wireOp",EDGE,"E9.14.35.0"),sQuery(id+"F0.wireOp",EDGE,"E9.1.36.0"),sQuery(id+"F0.wireOp",EDGE,"E9.3.36.0"),sQuery(id+"F0.wireOp",EDGE,"E9.7.36.0"),sQuery(id+"F0.wireOp",EDGE,"E9.11.36.0"),sQuery(id+"F0.wireOp",EDGE,"E9.14.36.0"),sQuery(id+"F0.wireOp",EDGE,"E9.1.37.0"),sQuery(id+"F0.wireOp",EDGE,"E9.3.37.0"),sQuery(id+"F0.wireOp",EDGE,"E9.7.37.0"),sQuery(id+"F0.wireOp",EDGE,"E9.11.37.0"),sQuery(id+"F0.wireOp",EDGE,"E9.14.37.0"),sQuery(id+"F0.wireOp",EDGE,"E9.1.38.0"),sQuery(id+"F0.wireOp",EDGE,"E9.3.38.0"),sQuery(id+"F0.wireOp",EDGE,"E9.7.38.0"),sQuery(id+"F0.wireOp",EDGE,"E9.11.38.0"),sQuery(id+"F0.wireOp",EDGE,"E9.14.38.0"),sQuery(id+"F0.wireOp",EDGE,"E9.1.39.0"),sQuery(id+"F0.wireOp",EDGE,"E9.3.39.0"),sQuery(id+"F0.wireOp",EDGE,"E9.7.39.0"),sQuery(id+"F0.wireOp",EDGE,"E9.11.39.0"),sQuery(id+"F0.wireOp",EDGE,"E9.14.39.0"),sQuery(id+"F0.wireOp",EDGE,"E9.1.40.0"),sQuery(id+"F0.wireOp",EDGE,"E9.3.40.0"),sQuery(id+"F0.wireOp",EDGE,"E9.7.40.0"),sQuery(id+"F0.wireOp",EDGE,"E9.11.40.0"),sQuery(id+"F0.wireOp",EDGE,"E9.14.40.0"),sQuery(id+"F0.wireOp",EDGE,"E9.1.41.0"),sQuery(id+"F0.wireOp",EDGE,"E9.3.41.0"),sQuery(id+"F0.wireOp",EDGE,"E9.7.41.0"),sQuery(id+"F0.wireOp",EDGE,"E9.11.41.0"),sQuery(id+"F0.wireOp",EDGE,"E9.14.41.0"),sQuery(id+"F0.wireOp",EDGE,"E9.1.42.0"),sQuery(id+"F0.wireOp",EDGE,"E9.3.42.0"),sQuery(id+"F0.wireOp",EDGE,"E9.7.42.0"),sQuery(id+"F0.wireOp",EDGE,"E9.11.42.0"),sQuery(id+"F0.wireOp",EDGE,"E9.14.42.0"),sQuery(id+"F0.wireOp",EDGE,"E9.1.43.0"),sQuery(id+"F0.wireOp",EDGE,"E9.3.43.0"),sQuery(id+"F0.wireOp",EDGE,"E9.7.43.0"),sQuery(id+"F0.wireOp",EDGE,"E9.11.43.0"),sQuery(id+"F0.wireOp",EDGE,"E9.14.43.0"),sQuery(id+"F0.wireOp",EDGE,"E9.1.44.0"),sQuery(id+"F0.wireOp",EDGE,"E9.3.44.0"),sQuery(id+"F0.wireOp",EDGE,"E9.7.44.0"),sQuery(id+"F0.wireOp",EDGE,"E9.11.44.0"),sQuery(id+"F0.wireOp",EDGE,"E9.14.44.0"),sQuery(id+"F0.wireOp",EDGE,"E9.1.45.0"),sQuery(id+"F0.wireOp",EDGE,"E9.3.45.0"),sQuery(id+"F0.wireOp",EDGE,"E9.7.45.0"),sQuery(id+"F0.wireOp",EDGE,"E9.11.45.0"),sQuery(id+"F0.wireOp",EDGE,"E9.14.45.0"),sQuery(id+"F0.wireOp",EDGE,"E9.1.46.0"),sQuery(id+"F0.wireOp",EDGE,"E9.3.46.0"),sQuery(id+"F0.wireOp",EDGE,"E9.7.46.0"),sQuery(id+"F0.wireOp",EDGE,"E9.11.46.0"),sQuery(id+"F0.wireOp",EDGE,"E9.14.46.0"),sQuery(id+"F0.wireOp",EDGE,"E9.1.47.0"),sQuery(id+"F0.wireOp",EDGE,"E9.3.47.0"),sQuery(id+"F0.wireOp",EDGE,"E9.7.47.0"),sQuery(id+"F0.wireOp",EDGE,"E9.11.47.0"),sQuery(id+"F0.wireOp",EDGE,"E9.14.47.0"),sQuery(id+"F0.wireOp",EDGE,"E9.1.48.0"),sQuery(id+"F0.wireOp",EDGE,"E9.3.48.0"),sQuery(id+"F0.wireOp",EDGE,"E9.7.48.0"),sQuery(id+"F0.wireOp",EDGE,"E9.11.48.0"),sQuery(id+"F0.wireOp",EDGE,"E9.14.48.0"),sQuery(id+"F0.wireOp",EDGE,"E9.1.49.0"),sQuery(id+"F0.wireOp",EDGE,"E9.3.49.0"),sQuery(id+"F0.wireOp",EDGE,"E9.7.49.0"),sQuery(id+"F0.wireOp",EDGE,"E9.11.49.0"),sQuery(id+"F0.wireOp",EDGE,"E9.14.49.0"),sQuery(id+"F0.wireOp",EDGE,"E9.1.50.0"),sQuery(id+"F0.wireOp",EDGE,"E9.3.50.0"),sQuery(id+"F0.wireOp",EDGE,"E9.7.50.0"),sQuery(id+"F0.wireOp",EDGE,"E9.11.50.0"),sQuery(id+"F0.wireOp",EDGE,"E9.14.50.0"),sQuery(id+"F0.wireOp",EDGE,"E9.1.51.0"),sQuery(id+"F0.wireOp",EDGE,"E9.3.51.0"),sQuery(id+"F0.wireOp",EDGE,"E9.7.51.0"),sQuery(id+"F0.wireOp",EDGE,"E9.11.51.0"),sQuery(id+"F0.wireOp",EDGE,"E9.14.51.0"),sQuery(id+"F0.wireOp",EDGE,"E9.1.52.0"),sQuery(id+"F0.wireOp",EDGE,"E9.3.52.0"),sQuery(id+"F0.wireOp",EDGE,"E9.7.52.0"),sQuery(id+"F0.wireOp",EDGE,"E9.11.52.0"),sQuery(id+"F0.wireOp",EDGE,"E9.14.52.0"),sQuery(id+"F0.wireOp",EDGE,"E9.1.53.0"),sQuery(id+"F0.wireOp",EDGE,"E9.3.53.0"),sQuery(id+"F0.wireOp",EDGE,"E9.7.53.0"),sQuery(id+"F0.wireOp",EDGE,"E9.11.53.0"),sQuery(id+"F0.wireOp",EDGE,"E9.14.53.0"),sQuery(id+"F0.wireOp",EDGE,"E9.1.54.0"),sQuery(id+"F0.wireOp",EDGE,"E9.3.54.0"),sQuery(id+"F0.wireOp",EDGE,"E9.7.54.0"),sQuery(id+"F0.wireOp",EDGE,"E9.11.54.0"),sQuery(id+"F0.wireOp",EDGE,"E9.14.54.0"),sQuery(id+"F0.wireOp",EDGE,"E9.1.55.0"),sQuery(id+"F0.wireOp",EDGE,"E9.3.55.0"),sQuery(id+"F0.wireOp",EDGE,"E9.7.55.0"),sQuery(id+"F0.wireOp",EDGE,"E9.11.55.0"),sQuery(id+"F0.wireOp",EDGE,"E9.14.55.0"),sQuery(id+"F0.wireOp",EDGE,"E9.1.56.0"),sQuery(id+"F0.wireOp",EDGE,"E9.3.56.0"),sQuery(id+"F0.wireOp",EDGE,"E9.7.56.0"),sQuery(id+"F0.wireOp",EDGE,"E9.11.56.0"),sQuery(id+"F0.wireOp",EDGE,"E9.14.56.0"),sQuery(id+"F0.wireOp",EDGE,"E9.1.57.0"),sQuery(id+"F0.wireOp",EDGE,"E9.3.57.0"),sQuery(id+"F0.wireOp",EDGE,"E9.7.57.0"),sQuery(id+"F0.wireOp",EDGE,"E9.11.57.0"),sQuery(id+"F0.wireOp",EDGE,"E9.14.57.0"),sQuery(id+"F0.wireOp",EDGE,"E9.1.58.0"),sQuery(id+"F0.wireOp",EDGE,"E9.3.58.0"),sQuery(id+"F0.wireOp",EDGE,"E9.7.58.0"),sQuery(id+"F0.wireOp",EDGE,"E9.11.58.0"),sQuery(id+"F0.wireOp",EDGE,"E9.14.58.0"),sQuery(id+"F0.wireOp",EDGE,"E9.1.59.0"),sQuery(id+"F0.wireOp",EDGE,"E9.3.59.0"),sQuery(id+"F0.wireOp",EDGE,"E9.7.59.0"),sQuery(id+"F0.wireOp",EDGE,"E9.11.59.0"),sQuery(id+"F0.wireOp",EDGE,"E9.14.59.0"),sQuery(id+"F2.wireOp",EDGE,"E35.trimOffspring")])],"isStart":false})});
            var Q2;
            Q2=makeQuery(id+"F8.boolean.opBoolean","COPY",EDGE,{"derivedFrom":makeQuery(id+"F8.opExtrude","CAP_EDGE",EDGE,{"disambiguationData":[OSD([sQuery(id+"F0.wireOp",EDGE,"E0"),sQuery(id+"F0.wireOp",EDGE,"E1"),sQuery(id+"F0.wireOp",EDGE,"E3"),sQuery(id+"F0.wireOp",EDGE,"E4"),sQuery(id+"F0.wireOp",EDGE,"E5"),sQuery(id+"F0.wireOp",EDGE,"E6.trimOffspring"),sQuery(id+"F0.wireOp",EDGE,"E7"),sQuery(id+"F0.wireOp",EDGE,"E8.1.0"),sQuery(id+"F0.wireOp",EDGE,"E8.1.1"),sQuery(id+"F0.wireOp",EDGE,"E8.1.2"),sQuery(id+"F0.wireOp",EDGE,"E8.1.3"),sQuery(id+"F0.wireOp",EDGE,"E8.1.4"),sQuery(id+"F0.wireOp",EDGE,"E8.2.0"),sQuery(id+"F0.wireOp",EDGE,"E8.2.1"),sQuery(id+"F0.wireOp",EDGE,"E8.2.2"),sQuery(id+"F0.wireOp",EDGE,"E8.2.3"),sQuery(id+"F0.wireOp",EDGE,"E8.2.4"),sQuery(id+"F0.wireOp",EDGE,"E9.1.3.0"),sQuery(id+"F0.wireOp",EDGE,"E9.3.3.0"),sQuery(id+"F0.wireOp",EDGE,"E9.7.3.0"),sQuery(id+"F0.wireOp",EDGE,"E9.11.3.0"),sQuery(id+"F0.wireOp",EDGE,"E9.14.3.0"),sQuery(id+"F0.wireOp",EDGE,"E9.1.4.0"),sQuery(id+"F0.wireOp",EDGE,"E9.3.4.0"),sQuery(id+"F0.wireOp",EDGE,"E9.7.4.0"),sQuery(id+"F0.wireOp",EDGE,"E9.11.4.0"),sQuery(id+"F0.wireOp",EDGE,"E9.14.4.0"),sQuery(id+"F0.wireOp",EDGE,"E9.1.5.0"),sQuery(id+"F0.wireOp",EDGE,"E9.3.5.0"),sQuery(id+"F0.wireOp",EDGE,"E9.7.5.0"),sQuery(id+"F0.wireOp",EDGE,"E9.11.5.0"),sQuery(id+"F0.wireOp",EDGE,"E9.14.5.0"),sQuery(id+"F0.wireOp",EDGE,"E9.1.6.0"),sQuery(id+"F0.wireOp",EDGE,"E9.3.6.0"),sQuery(id+"F0.wireOp",EDGE,"E9.7.6.0"),sQuery(id+"F0.wireOp",EDGE,"E9.11.6.0"),sQuery(id+"F0.wireOp",EDGE,"E9.14.6.0"),sQuery(id+"F0.wireOp",EDGE,"E9.1.7.0"),sQuery(id+"F0.wireOp",EDGE,"E9.3.7.0"),sQuery(id+"F0.wireOp",EDGE,"E9.7.7.0"),sQuery(id+"F0.wireOp",EDGE,"E9.11.7.0"),sQuery(id+"F0.wireOp",EDGE,"E9.14.7.0"),sQuery(id+"F0.wireOp",EDGE,"E9.1.8.0"),sQuery(id+"F0.wireOp",EDGE,"E9.3.8.0"),sQuery(id+"F0.wireOp",EDGE,"E9.7.8.0"),sQuery(id+"F0.wireOp",EDGE,"E9.11.8.0"),sQuery(id+"F0.wireOp",EDGE,"E9.14.8.0"),sQuery(id+"F0.wireOp",EDGE,"E9.1.9.0"),sQuery(id+"F0.wireOp",EDGE,"E9.3.9.0"),sQuery(id+"F0.wireOp",EDGE,"E9.7.9.0"),sQuery(id+"F0.wireOp",EDGE,"E9.11.9.0"),sQuery(id+"F0.wireOp",EDGE,"E9.14.9.0"),sQuery(id+"F0.wireOp",EDGE,"E9.1.10.0"),sQuery(id+"F0.wireOp",EDGE,"E9.3.10.0"),sQuery(id+"F0.wireOp",EDGE,"E9.7.10.0"),sQuery(id+"F0.wireOp",EDGE,"E9.11.10.0"),sQuery(id+"F0.wireOp",EDGE,"E9.14.10.0"),sQuery(id+"F0.wireOp",EDGE,"E9.1.11.0"),sQuery(id+"F0.wireOp",EDGE,"E9.3.11.0"),sQuery(id+"F0.wireOp",EDGE,"E9.7.11.0"),sQuery(id+"F0.wireOp",EDGE,"E9.11.11.0"),sQuery(id+"F0.wireOp",EDGE,"E9.14.11.0"),sQuery(id+"F0.wireOp",EDGE,"E9.1.12.0"),sQuery(id+"F0.wireOp",EDGE,"E9.3.12.0"),sQuery(id+"F0.wireOp",EDGE,"E9.7.12.0"),sQuery(id+"F0.wireOp",EDGE,"E9.11.12.0"),sQuery(id+"F0.wireOp",EDGE,"E9.14.12.0"),sQuery(id+"F0.wireOp",EDGE,"E9.1.13.0"),sQuery(id+"F0.wireOp",EDGE,"E9.3.13.0"),sQuery(id+"F0.wireOp",EDGE,"E9.7.13.0"),sQuery(id+"F0.wireOp",EDGE,"E9.11.13.0"),sQuery(id+"F0.wireOp",EDGE,"E9.14.13.0"),sQuery(id+"F0.wireOp",EDGE,"E9.1.14.0"),sQuery(id+"F0.wireOp",EDGE,"E9.3.14.0"),sQuery(id+"F0.wireOp",EDGE,"E9.7.14.0"),sQuery(id+"F0.wireOp",EDGE,"E9.11.14.0"),sQuery(id+"F0.wireOp",EDGE,"E9.14.14.0"),sQuery(id+"F0.wireOp",EDGE,"E9.1.15.0"),sQuery(id+"F0.wireOp",EDGE,"E9.3.15.0"),sQuery(id+"F0.wireOp",EDGE,"E9.7.15.0"),sQuery(id+"F0.wireOp",EDGE,"E9.11.15.0"),sQuery(id+"F0.wireOp",EDGE,"E9.14.15.0"),sQuery(id+"F0.wireOp",EDGE,"E9.1.16.0"),sQuery(id+"F0.wireOp",EDGE,"E9.3.16.0"),sQuery(id+"F0.wireOp",EDGE,"E9.7.16.0"),sQuery(id+"F0.wireOp",EDGE,"E9.11.16.0"),sQuery(id+"F0.wireOp",EDGE,"E9.14.16.0"),sQuery(id+"F0.wireOp",EDGE,"E9.1.17.0"),sQuery(id+"F0.wireOp",EDGE,"E9.3.17.0"),sQuery(id+"F0.wireOp",EDGE,"E9.7.17.0"),sQuery(id+"F0.wireOp",EDGE,"E9.11.17.0"),sQuery(id+"F0.wireOp",EDGE,"E9.14.17.0"),sQuery(id+"F0.wireOp",EDGE,"E9.1.18.0"),sQuery(id+"F0.wireOp",EDGE,"E9.3.18.0"),sQuery(id+"F0.wireOp",EDGE,"E9.7.18.0"),sQuery(id+"F0.wireOp",EDGE,"E9.11.18.0"),sQuery(id+"F0.wireOp",EDGE,"E9.14.18.0"),sQuery(id+"F0.wireOp",EDGE,"E9.1.19.0"),sQuery(id+"F0.wireOp",EDGE,"E9.3.19.0"),sQuery(id+"F0.wireOp",EDGE,"E9.7.19.0"),sQuery(id+"F0.wireOp",EDGE,"E9.11.19.0"),sQuery(id+"F0.wireOp",EDGE,"E9.14.19.0"),sQuery(id+"F0.wireOp",EDGE,"E9.1.20.0"),sQuery(id+"F0.wireOp",EDGE,"E9.3.20.0"),sQuery(id+"F0.wireOp",EDGE,"E9.7.20.0"),sQuery(id+"F0.wireOp",EDGE,"E9.11.20.0"),sQuery(id+"F0.wireOp",EDGE,"E9.14.20.0"),sQuery(id+"F0.wireOp",EDGE,"E9.1.21.0"),sQuery(id+"F0.wireOp",EDGE,"E9.3.21.0"),sQuery(id+"F0.wireOp",EDGE,"E9.7.21.0"),sQuery(id+"F0.wireOp",EDGE,"E9.11.21.0"),sQuery(id+"F0.wireOp",EDGE,"E9.14.21.0"),sQuery(id+"F0.wireOp",EDGE,"E9.1.22.0"),sQuery(id+"F0.wireOp",EDGE,"E9.3.22.0"),sQuery(id+"F0.wireOp",EDGE,"E9.7.22.0"),sQuery(id+"F0.wireOp",EDGE,"E9.11.22.0"),sQuery(id+"F0.wireOp",EDGE,"E9.14.22.0"),sQuery(id+"F0.wireOp",EDGE,"E9.1.23.0"),sQuery(id+"F0.wireOp",EDGE,"E9.3.23.0"),sQuery(id+"F0.wireOp",EDGE,"E9.7.23.0"),sQuery(id+"F0.wireOp",EDGE,"E9.11.23.0"),sQuery(id+"F0.wireOp",EDGE,"E9.14.23.0"),sQuery(id+"F0.wireOp",EDGE,"E9.1.24.0"),sQuery(id+"F0.wireOp",EDGE,"E9.3.24.0"),sQuery(id+"F0.wireOp",EDGE,"E9.7.24.0"),sQuery(id+"F0.wireOp",EDGE,"E9.11.24.0"),sQuery(id+"F0.wireOp",EDGE,"E9.14.24.0"),sQuery(id+"F0.wireOp",EDGE,"E9.1.25.0"),sQuery(id+"F0.wireOp",EDGE,"E9.3.25.0"),sQuery(id+"F0.wireOp",EDGE,"E9.7.25.0"),sQuery(id+"F0.wireOp",EDGE,"E9.11.25.0"),sQuery(id+"F0.wireOp",EDGE,"E9.14.25.0"),sQuery(id+"F0.wireOp",EDGE,"E9.1.26.0"),sQuery(id+"F0.wireOp",EDGE,"E9.3.26.0"),sQuery(id+"F0.wireOp",EDGE,"E9.7.26.0"),sQuery(id+"F0.wireOp",EDGE,"E9.11.26.0"),sQuery(id+"F0.wireOp",EDGE,"E9.14.26.0"),sQuery(id+"F0.wireOp",EDGE,"E9.1.27.0"),sQuery(id+"F0.wireOp",EDGE,"E9.3.27.0"),sQuery(id+"F0.wireOp",EDGE,"E9.7.27.0"),sQuery(id+"F0.wireOp",EDGE,"E9.11.27.0"),sQuery(id+"F0.wireOp",EDGE,"E9.14.27.0"),sQuery(id+"F0.wireOp",EDGE,"E9.1.28.0"),sQuery(id+"F0.wireOp",EDGE,"E9.3.28.0"),sQuery(id+"F0.wireOp",EDGE,"E9.7.28.0"),sQuery(id+"F0.wireOp",EDGE,"E9.11.28.0"),sQuery(id+"F0.wireOp",EDGE,"E9.14.28.0"),sQuery(id+"F0.wireOp",EDGE,"E9.1.29.0"),sQuery(id+"F0.wireOp",EDGE,"E9.3.29.0"),sQuery(id+"F0.wireOp",EDGE,"E9.7.29.0"),sQuery(id+"F0.wireOp",EDGE,"E9.11.29.0"),sQuery(id+"F0.wireOp",EDGE,"E9.14.29.0"),sQuery(id+"F0.wireOp",EDGE,"E9.1.30.0"),sQuery(id+"F0.wireOp",EDGE,"E9.3.30.0"),sQuery(id+"F0.wireOp",EDGE,"E9.7.30.0"),sQuery(id+"F0.wireOp",EDGE,"E9.11.30.0"),sQuery(id+"F0.wireOp",EDGE,"E9.14.30.0"),sQuery(id+"F0.wireOp",EDGE,"E9.1.31.0"),sQuery(id+"F0.wireOp",EDGE,"E9.3.31.0"),sQuery(id+"F0.wireOp",EDGE,"E9.7.31.0"),sQuery(id+"F0.wireOp",EDGE,"E9.11.31.0"),sQuery(id+"F0.wireOp",EDGE,"E9.14.31.0"),sQuery(id+"F0.wireOp",EDGE,"E9.1.32.0"),sQuery(id+"F0.wireOp",EDGE,"E9.3.32.0"),sQuery(id+"F0.wireOp",EDGE,"E9.7.32.0"),sQuery(id+"F0.wireOp",EDGE,"E9.11.32.0"),sQuery(id+"F0.wireOp",EDGE,"E9.14.32.0"),sQuery(id+"F0.wireOp",EDGE,"E9.1.33.0"),sQuery(id+"F0.wireOp",EDGE,"E9.3.33.0"),sQuery(id+"F0.wireOp",EDGE,"E9.7.33.0"),sQuery(id+"F0.wireOp",EDGE,"E9.11.33.0"),sQuery(id+"F0.wireOp",EDGE,"E9.14.33.0"),sQuery(id+"F0.wireOp",EDGE,"E9.1.34.0"),sQuery(id+"F0.wireOp",EDGE,"E9.3.34.0"),sQuery(id+"F0.wireOp",EDGE,"E9.7.34.0"),sQuery(id+"F0.wireOp",EDGE,"E9.11.34.0"),sQuery(id+"F0.wireOp",EDGE,"E9.14.34.0"),sQuery(id+"F0.wireOp",EDGE,"E9.1.35.0"),sQuery(id+"F0.wireOp",EDGE,"E9.3.35.0"),sQuery(id+"F0.wireOp",EDGE,"E9.7.35.0"),sQuery(id+"F0.wireOp",EDGE,"E9.11.35.0"),sQuery(id+"F0.wireOp",EDGE,"E9.14.35.0"),sQuery(id+"F0.wireOp",EDGE,"E9.1.36.0"),sQuery(id+"F0.wireOp",EDGE,"E9.3.36.0"),sQuery(id+"F0.wireOp",EDGE,"E9.7.36.0"),sQuery(id+"F0.wireOp",EDGE,"E9.11.36.0"),sQuery(id+"F0.wireOp",EDGE,"E9.14.36.0"),sQuery(id+"F0.wireOp",EDGE,"E9.1.37.0"),sQuery(id+"F0.wireOp",EDGE,"E9.3.37.0"),sQuery(id+"F0.wireOp",EDGE,"E9.7.37.0"),sQuery(id+"F0.wireOp",EDGE,"E9.11.37.0"),sQuery(id+"F0.wireOp",EDGE,"E9.14.37.0"),sQuery(id+"F0.wireOp",EDGE,"E9.1.38.0"),sQuery(id+"F0.wireOp",EDGE,"E9.3.38.0"),sQuery(id+"F0.wireOp",EDGE,"E9.7.38.0"),sQuery(id+"F0.wireOp",EDGE,"E9.11.38.0"),sQuery(id+"F0.wireOp",EDGE,"E9.14.38.0"),sQuery(id+"F0.wireOp",EDGE,"E9.1.39.0"),sQuery(id+"F0.wireOp",EDGE,"E9.3.39.0"),sQuery(id+"F0.wireOp",EDGE,"E9.7.39.0"),sQuery(id+"F0.wireOp",EDGE,"E9.11.39.0"),sQuery(id+"F0.wireOp",EDGE,"E9.14.39.0"),sQuery(id+"F0.wireOp",EDGE,"E9.1.40.0"),sQuery(id+"F0.wireOp",EDGE,"E9.3.40.0"),sQuery(id+"F0.wireOp",EDGE,"E9.7.40.0"),sQuery(id+"F0.wireOp",EDGE,"E9.11.40.0"),sQuery(id+"F0.wireOp",EDGE,"E9.14.40.0"),sQuery(id+"F0.wireOp",EDGE,"E9.1.41.0"),sQuery(id+"F0.wireOp",EDGE,"E9.3.41.0"),sQuery(id+"F0.wireOp",EDGE,"E9.7.41.0"),sQuery(id+"F0.wireOp",EDGE,"E9.11.41.0"),sQuery(id+"F0.wireOp",EDGE,"E9.14.41.0"),sQuery(id+"F0.wireOp",EDGE,"E9.1.42.0"),sQuery(id+"F0.wireOp",EDGE,"E9.3.42.0"),sQuery(id+"F0.wireOp",EDGE,"E9.7.42.0"),sQuery(id+"F0.wireOp",EDGE,"E9.11.42.0"),sQuery(id+"F0.wireOp",EDGE,"E9.14.42.0"),sQuery(id+"F0.wireOp",EDGE,"E9.1.43.0"),sQuery(id+"F0.wireOp",EDGE,"E9.3.43.0"),sQuery(id+"F0.wireOp",EDGE,"E9.7.43.0"),sQuery(id+"F0.wireOp",EDGE,"E9.11.43.0"),sQuery(id+"F0.wireOp",EDGE,"E9.14.43.0"),sQuery(id+"F0.wireOp",EDGE,"E9.1.44.0"),sQuery(id+"F0.wireOp",EDGE,"E9.3.44.0"),sQuery(id+"F0.wireOp",EDGE,"E9.7.44.0"),sQuery(id+"F0.wireOp",EDGE,"E9.11.44.0"),sQuery(id+"F0.wireOp",EDGE,"E9.14.44.0"),sQuery(id+"F0.wireOp",EDGE,"E9.1.45.0"),sQuery(id+"F0.wireOp",EDGE,"E9.3.45.0"),sQuery(id+"F0.wireOp",EDGE,"E9.7.45.0"),sQuery(id+"F0.wireOp",EDGE,"E9.11.45.0"),sQuery(id+"F0.wireOp",EDGE,"E9.14.45.0"),sQuery(id+"F0.wireOp",EDGE,"E9.1.46.0"),sQuery(id+"F0.wireOp",EDGE,"E9.3.46.0"),sQuery(id+"F0.wireOp",EDGE,"E9.7.46.0"),sQuery(id+"F0.wireOp",EDGE,"E9.11.46.0"),sQuery(id+"F0.wireOp",EDGE,"E9.14.46.0"),sQuery(id+"F0.wireOp",EDGE,"E9.1.47.0"),sQuery(id+"F0.wireOp",EDGE,"E9.3.47.0"),sQuery(id+"F0.wireOp",EDGE,"E9.7.47.0"),sQuery(id+"F0.wireOp",EDGE,"E9.11.47.0"),sQuery(id+"F0.wireOp",EDGE,"E9.14.47.0"),sQuery(id+"F0.wireOp",EDGE,"E9.1.48.0"),sQuery(id+"F0.wireOp",EDGE,"E9.3.48.0"),sQuery(id+"F0.wireOp",EDGE,"E9.7.48.0"),sQuery(id+"F0.wireOp",EDGE,"E9.11.48.0"),sQuery(id+"F0.wireOp",EDGE,"E9.14.48.0"),sQuery(id+"F0.wireOp",EDGE,"E9.1.49.0"),sQuery(id+"F0.wireOp",EDGE,"E9.3.49.0"),sQuery(id+"F0.wireOp",EDGE,"E9.7.49.0"),sQuery(id+"F0.wireOp",EDGE,"E9.11.49.0"),sQuery(id+"F0.wireOp",EDGE,"E9.14.49.0"),sQuery(id+"F0.wireOp",EDGE,"E9.1.50.0"),sQuery(id+"F0.wireOp",EDGE,"E9.3.50.0"),sQuery(id+"F0.wireOp",EDGE,"E9.7.50.0"),sQuery(id+"F0.wireOp",EDGE,"E9.11.50.0"),sQuery(id+"F0.wireOp",EDGE,"E9.14.50.0"),sQuery(id+"F0.wireOp",EDGE,"E9.1.51.0"),sQuery(id+"F0.wireOp",EDGE,"E9.3.51.0"),sQuery(id+"F0.wireOp",EDGE,"E9.7.51.0"),sQuery(id+"F0.wireOp",EDGE,"E9.11.51.0"),sQuery(id+"F0.wireOp",EDGE,"E9.14.51.0"),sQuery(id+"F0.wireOp",EDGE,"E9.1.52.0"),sQuery(id+"F0.wireOp",EDGE,"E9.3.52.0"),sQuery(id+"F0.wireOp",EDGE,"E9.7.52.0"),sQuery(id+"F0.wireOp",EDGE,"E9.11.52.0"),sQuery(id+"F0.wireOp",EDGE,"E9.14.52.0"),sQuery(id+"F0.wireOp",EDGE,"E9.1.53.0"),sQuery(id+"F0.wireOp",EDGE,"E9.3.53.0"),sQuery(id+"F0.wireOp",EDGE,"E9.7.53.0"),sQuery(id+"F0.wireOp",EDGE,"E9.11.53.0"),sQuery(id+"F0.wireOp",EDGE,"E9.14.53.0"),sQuery(id+"F0.wireOp",EDGE,"E9.1.54.0"),sQuery(id+"F0.wireOp",EDGE,"E9.3.54.0"),sQuery(id+"F0.wireOp",EDGE,"E9.7.54.0"),sQuery(id+"F0.wireOp",EDGE,"E9.11.54.0"),sQuery(id+"F0.wireOp",EDGE,"E9.14.54.0"),sQuery(id+"F0.wireOp",EDGE,"E9.1.55.0"),sQuery(id+"F0.wireOp",EDGE,"E9.3.55.0"),sQuery(id+"F0.wireOp",EDGE,"E9.7.55.0"),sQuery(id+"F0.wireOp",EDGE,"E9.11.55.0"),sQuery(id+"F0.wireOp",EDGE,"E9.14.55.0"),sQuery(id+"F0.wireOp",EDGE,"E9.1.56.0"),sQuery(id+"F0.wireOp",EDGE,"E9.3.56.0"),sQuery(id+"F0.wireOp",EDGE,"E9.7.56.0"),sQuery(id+"F0.wireOp",EDGE,"E9.11.56.0"),sQuery(id+"F0.wireOp",EDGE,"E9.14.56.0"),sQuery(id+"F0.wireOp",EDGE,"E9.1.57.0"),sQuery(id+"F0.wireOp",EDGE,"E9.3.57.0"),sQuery(id+"F0.wireOp",EDGE,"E9.7.57.0"),sQuery(id+"F0.wireOp",EDGE,"E9.11.57.0"),sQuery(id+"F0.wireOp",EDGE,"E9.14.57.0"),sQuery(id+"F0.wireOp",EDGE,"E9.1.58.0"),sQuery(id+"F0.wireOp",EDGE,"E9.3.58.0"),sQuery(id+"F0.wireOp",EDGE,"E9.7.58.0"),sQuery(id+"F0.wireOp",EDGE,"E9.11.58.0"),sQuery(id+"F0.wireOp",EDGE,"E9.14.58.0"),sQuery(id+"F0.wireOp",EDGE,"E9.1.59.0"),sQuery(id+"F0.wireOp",EDGE,"E9.3.59.0"),sQuery(id+"F0.wireOp",EDGE,"E9.7.59.0"),sQuery(id+"F0.wireOp",EDGE,"E9.11.59.0"),sQuery(id+"F0.wireOp",EDGE,"E9.14.59.0"),sQuery(id+"F2.wireOp",EDGE,"E20.0")])],"isStart":false})});
            var Q3;
            Q3=makeQuery(id+"F8.boolean.opBoolean","COPY",EDGE,{"derivedFrom":makeQuery(id+"F8.opExtrude","CAP_EDGE",EDGE,{"disambiguationData":[OSD([sQuery(id+"F0.wireOp",EDGE,"E0"),sQuery(id+"F0.wireOp",EDGE,"E1"),sQuery(id+"F0.wireOp",EDGE,"E3"),sQuery(id+"F0.wireOp",EDGE,"E4"),sQuery(id+"F0.wireOp",EDGE,"E5"),sQuery(id+"F0.wireOp",EDGE,"E6.trimOffspring"),sQuery(id+"F0.wireOp",EDGE,"E7"),sQuery(id+"F0.wireOp",EDGE,"E8.1.0"),sQuery(id+"F0.wireOp",EDGE,"E8.1.1"),sQuery(id+"F0.wireOp",EDGE,"E8.1.2"),sQuery(id+"F0.wireOp",EDGE,"E8.1.3"),sQuery(id+"F0.wireOp",EDGE,"E8.1.4"),sQuery(id+"F0.wireOp",EDGE,"E8.2.0"),sQuery(id+"F0.wireOp",EDGE,"E8.2.1"),sQuery(id+"F0.wireOp",EDGE,"E8.2.2"),sQuery(id+"F0.wireOp",EDGE,"E8.2.3"),sQuery(id+"F0.wireOp",EDGE,"E8.2.4"),sQuery(id+"F0.wireOp",EDGE,"E9.1.3.0"),sQuery(id+"F0.wireOp",EDGE,"E9.3.3.0"),sQuery(id+"F0.wireOp",EDGE,"E9.7.3.0"),sQuery(id+"F0.wireOp",EDGE,"E9.11.3.0"),sQuery(id+"F0.wireOp",EDGE,"E9.14.3.0"),sQuery(id+"F0.wireOp",EDGE,"E9.1.4.0"),sQuery(id+"F0.wireOp",EDGE,"E9.3.4.0"),sQuery(id+"F0.wireOp",EDGE,"E9.7.4.0"),sQuery(id+"F0.wireOp",EDGE,"E9.11.4.0"),sQuery(id+"F0.wireOp",EDGE,"E9.14.4.0"),sQuery(id+"F0.wireOp",EDGE,"E9.1.5.0"),sQuery(id+"F0.wireOp",EDGE,"E9.3.5.0"),sQuery(id+"F0.wireOp",EDGE,"E9.7.5.0"),sQuery(id+"F0.wireOp",EDGE,"E9.11.5.0"),sQuery(id+"F0.wireOp",EDGE,"E9.14.5.0"),sQuery(id+"F0.wireOp",EDGE,"E9.1.6.0"),sQuery(id+"F0.wireOp",EDGE,"E9.3.6.0"),sQuery(id+"F0.wireOp",EDGE,"E9.7.6.0"),sQuery(id+"F0.wireOp",EDGE,"E9.11.6.0"),sQuery(id+"F0.wireOp",EDGE,"E9.14.6.0"),sQuery(id+"F0.wireOp",EDGE,"E9.1.7.0"),sQuery(id+"F0.wireOp",EDGE,"E9.3.7.0"),sQuery(id+"F0.wireOp",EDGE,"E9.7.7.0"),sQuery(id+"F0.wireOp",EDGE,"E9.11.7.0"),sQuery(id+"F0.wireOp",EDGE,"E9.14.7.0"),sQuery(id+"F0.wireOp",EDGE,"E9.1.8.0"),sQuery(id+"F0.wireOp",EDGE,"E9.3.8.0"),sQuery(id+"F0.wireOp",EDGE,"E9.7.8.0"),sQuery(id+"F0.wireOp",EDGE,"E9.11.8.0"),sQuery(id+"F0.wireOp",EDGE,"E9.14.8.0"),sQuery(id+"F0.wireOp",EDGE,"E9.1.9.0"),sQuery(id+"F0.wireOp",EDGE,"E9.3.9.0"),sQuery(id+"F0.wireOp",EDGE,"E9.7.9.0"),sQuery(id+"F0.wireOp",EDGE,"E9.11.9.0"),sQuery(id+"F0.wireOp",EDGE,"E9.14.9.0"),sQuery(id+"F0.wireOp",EDGE,"E9.1.10.0"),sQuery(id+"F0.wireOp",EDGE,"E9.3.10.0"),sQuery(id+"F0.wireOp",EDGE,"E9.7.10.0"),sQuery(id+"F0.wireOp",EDGE,"E9.11.10.0"),sQuery(id+"F0.wireOp",EDGE,"E9.14.10.0"),sQuery(id+"F0.wireOp",EDGE,"E9.1.11.0"),sQuery(id+"F0.wireOp",EDGE,"E9.3.11.0"),sQuery(id+"F0.wireOp",EDGE,"E9.7.11.0"),sQuery(id+"F0.wireOp",EDGE,"E9.11.11.0"),sQuery(id+"F0.wireOp",EDGE,"E9.14.11.0"),sQuery(id+"F0.wireOp",EDGE,"E9.1.12.0"),sQuery(id+"F0.wireOp",EDGE,"E9.3.12.0"),sQuery(id+"F0.wireOp",EDGE,"E9.7.12.0"),sQuery(id+"F0.wireOp",EDGE,"E9.11.12.0"),sQuery(id+"F0.wireOp",EDGE,"E9.14.12.0"),sQuery(id+"F0.wireOp",EDGE,"E9.1.13.0"),sQuery(id+"F0.wireOp",EDGE,"E9.3.13.0"),sQuery(id+"F0.wireOp",EDGE,"E9.7.13.0"),sQuery(id+"F0.wireOp",EDGE,"E9.11.13.0"),sQuery(id+"F0.wireOp",EDGE,"E9.14.13.0"),sQuery(id+"F0.wireOp",EDGE,"E9.1.14.0"),sQuery(id+"F0.wireOp",EDGE,"E9.3.14.0"),sQuery(id+"F0.wireOp",EDGE,"E9.7.14.0"),sQuery(id+"F0.wireOp",EDGE,"E9.11.14.0"),sQuery(id+"F0.wireOp",EDGE,"E9.14.14.0"),sQuery(id+"F0.wireOp",EDGE,"E9.1.15.0"),sQuery(id+"F0.wireOp",EDGE,"E9.3.15.0"),sQuery(id+"F0.wireOp",EDGE,"E9.7.15.0"),sQuery(id+"F0.wireOp",EDGE,"E9.11.15.0"),sQuery(id+"F0.wireOp",EDGE,"E9.14.15.0"),sQuery(id+"F0.wireOp",EDGE,"E9.1.16.0"),sQuery(id+"F0.wireOp",EDGE,"E9.3.16.0"),sQuery(id+"F0.wireOp",EDGE,"E9.7.16.0"),sQuery(id+"F0.wireOp",EDGE,"E9.11.16.0"),sQuery(id+"F0.wireOp",EDGE,"E9.14.16.0"),sQuery(id+"F0.wireOp",EDGE,"E9.1.17.0"),sQuery(id+"F0.wireOp",EDGE,"E9.3.17.0"),sQuery(id+"F0.wireOp",EDGE,"E9.7.17.0"),sQuery(id+"F0.wireOp",EDGE,"E9.11.17.0"),sQuery(id+"F0.wireOp",EDGE,"E9.14.17.0"),sQuery(id+"F0.wireOp",EDGE,"E9.1.18.0"),sQuery(id+"F0.wireOp",EDGE,"E9.3.18.0"),sQuery(id+"F0.wireOp",EDGE,"E9.7.18.0"),sQuery(id+"F0.wireOp",EDGE,"E9.11.18.0"),sQuery(id+"F0.wireOp",EDGE,"E9.14.18.0"),sQuery(id+"F0.wireOp",EDGE,"E9.1.19.0"),sQuery(id+"F0.wireOp",EDGE,"E9.3.19.0"),sQuery(id+"F0.wireOp",EDGE,"E9.7.19.0"),sQuery(id+"F0.wireOp",EDGE,"E9.11.19.0"),sQuery(id+"F0.wireOp",EDGE,"E9.14.19.0"),sQuery(id+"F0.wireOp",EDGE,"E9.1.20.0"),sQuery(id+"F0.wireOp",EDGE,"E9.3.20.0"),sQuery(id+"F0.wireOp",EDGE,"E9.7.20.0"),sQuery(id+"F0.wireOp",EDGE,"E9.11.20.0"),sQuery(id+"F0.wireOp",EDGE,"E9.14.20.0"),sQuery(id+"F0.wireOp",EDGE,"E9.1.21.0"),sQuery(id+"F0.wireOp",EDGE,"E9.3.21.0"),sQuery(id+"F0.wireOp",EDGE,"E9.7.21.0"),sQuery(id+"F0.wireOp",EDGE,"E9.11.21.0"),sQuery(id+"F0.wireOp",EDGE,"E9.14.21.0"),sQuery(id+"F0.wireOp",EDGE,"E9.1.22.0"),sQuery(id+"F0.wireOp",EDGE,"E9.3.22.0"),sQuery(id+"F0.wireOp",EDGE,"E9.7.22.0"),sQuery(id+"F0.wireOp",EDGE,"E9.11.22.0"),sQuery(id+"F0.wireOp",EDGE,"E9.14.22.0"),sQuery(id+"F0.wireOp",EDGE,"E9.1.23.0"),sQuery(id+"F0.wireOp",EDGE,"E9.3.23.0"),sQuery(id+"F0.wireOp",EDGE,"E9.7.23.0"),sQuery(id+"F0.wireOp",EDGE,"E9.11.23.0"),sQuery(id+"F0.wireOp",EDGE,"E9.14.23.0"),sQuery(id+"F0.wireOp",EDGE,"E9.1.24.0"),sQuery(id+"F0.wireOp",EDGE,"E9.3.24.0"),sQuery(id+"F0.wireOp",EDGE,"E9.7.24.0"),sQuery(id+"F0.wireOp",EDGE,"E9.11.24.0"),sQuery(id+"F0.wireOp",EDGE,"E9.14.24.0"),sQuery(id+"F0.wireOp",EDGE,"E9.1.25.0"),sQuery(id+"F0.wireOp",EDGE,"E9.3.25.0"),sQuery(id+"F0.wireOp",EDGE,"E9.7.25.0"),sQuery(id+"F0.wireOp",EDGE,"E9.11.25.0"),sQuery(id+"F0.wireOp",EDGE,"E9.14.25.0"),sQuery(id+"F0.wireOp",EDGE,"E9.1.26.0"),sQuery(id+"F0.wireOp",EDGE,"E9.3.26.0"),sQuery(id+"F0.wireOp",EDGE,"E9.7.26.0"),sQuery(id+"F0.wireOp",EDGE,"E9.11.26.0"),sQuery(id+"F0.wireOp",EDGE,"E9.14.26.0"),sQuery(id+"F0.wireOp",EDGE,"E9.1.27.0"),sQuery(id+"F0.wireOp",EDGE,"E9.3.27.0"),sQuery(id+"F0.wireOp",EDGE,"E9.7.27.0"),sQuery(id+"F0.wireOp",EDGE,"E9.11.27.0"),sQuery(id+"F0.wireOp",EDGE,"E9.14.27.0"),sQuery(id+"F0.wireOp",EDGE,"E9.1.28.0"),sQuery(id+"F0.wireOp",EDGE,"E9.3.28.0"),sQuery(id+"F0.wireOp",EDGE,"E9.7.28.0"),sQuery(id+"F0.wireOp",EDGE,"E9.11.28.0"),sQuery(id+"F0.wireOp",EDGE,"E9.14.28.0"),sQuery(id+"F0.wireOp",EDGE,"E9.1.29.0"),sQuery(id+"F0.wireOp",EDGE,"E9.3.29.0"),sQuery(id+"F0.wireOp",EDGE,"E9.7.29.0"),sQuery(id+"F0.wireOp",EDGE,"E9.11.29.0"),sQuery(id+"F0.wireOp",EDGE,"E9.14.29.0"),sQuery(id+"F0.wireOp",EDGE,"E9.1.30.0"),sQuery(id+"F0.wireOp",EDGE,"E9.3.30.0"),sQuery(id+"F0.wireOp",EDGE,"E9.7.30.0"),sQuery(id+"F0.wireOp",EDGE,"E9.11.30.0"),sQuery(id+"F0.wireOp",EDGE,"E9.14.30.0"),sQuery(id+"F0.wireOp",EDGE,"E9.1.31.0"),sQuery(id+"F0.wireOp",EDGE,"E9.3.31.0"),sQuery(id+"F0.wireOp",EDGE,"E9.7.31.0"),sQuery(id+"F0.wireOp",EDGE,"E9.11.31.0"),sQuery(id+"F0.wireOp",EDGE,"E9.14.31.0"),sQuery(id+"F0.wireOp",EDGE,"E9.1.32.0"),sQuery(id+"F0.wireOp",EDGE,"E9.3.32.0"),sQuery(id+"F0.wireOp",EDGE,"E9.7.32.0"),sQuery(id+"F0.wireOp",EDGE,"E9.11.32.0"),sQuery(id+"F0.wireOp",EDGE,"E9.14.32.0"),sQuery(id+"F0.wireOp",EDGE,"E9.1.33.0"),sQuery(id+"F0.wireOp",EDGE,"E9.3.33.0"),sQuery(id+"F0.wireOp",EDGE,"E9.7.33.0"),sQuery(id+"F0.wireOp",EDGE,"E9.11.33.0"),sQuery(id+"F0.wireOp",EDGE,"E9.14.33.0"),sQuery(id+"F0.wireOp",EDGE,"E9.1.34.0"),sQuery(id+"F0.wireOp",EDGE,"E9.3.34.0"),sQuery(id+"F0.wireOp",EDGE,"E9.7.34.0"),sQuery(id+"F0.wireOp",EDGE,"E9.11.34.0"),sQuery(id+"F0.wireOp",EDGE,"E9.14.34.0"),sQuery(id+"F0.wireOp",EDGE,"E9.1.35.0"),sQuery(id+"F0.wireOp",EDGE,"E9.3.35.0"),sQuery(id+"F0.wireOp",EDGE,"E9.7.35.0"),sQuery(id+"F0.wireOp",EDGE,"E9.11.35.0"),sQuery(id+"F0.wireOp",EDGE,"E9.14.35.0"),sQuery(id+"F0.wireOp",EDGE,"E9.1.36.0"),sQuery(id+"F0.wireOp",EDGE,"E9.3.36.0"),sQuery(id+"F0.wireOp",EDGE,"E9.7.36.0"),sQuery(id+"F0.wireOp",EDGE,"E9.11.36.0"),sQuery(id+"F0.wireOp",EDGE,"E9.14.36.0"),sQuery(id+"F0.wireOp",EDGE,"E9.1.37.0"),sQuery(id+"F0.wireOp",EDGE,"E9.3.37.0"),sQuery(id+"F0.wireOp",EDGE,"E9.7.37.0"),sQuery(id+"F0.wireOp",EDGE,"E9.11.37.0"),sQuery(id+"F0.wireOp",EDGE,"E9.14.37.0"),sQuery(id+"F0.wireOp",EDGE,"E9.1.38.0"),sQuery(id+"F0.wireOp",EDGE,"E9.3.38.0"),sQuery(id+"F0.wireOp",EDGE,"E9.7.38.0"),sQuery(id+"F0.wireOp",EDGE,"E9.11.38.0"),sQuery(id+"F0.wireOp",EDGE,"E9.14.38.0"),sQuery(id+"F0.wireOp",EDGE,"E9.1.39.0"),sQuery(id+"F0.wireOp",EDGE,"E9.3.39.0"),sQuery(id+"F0.wireOp",EDGE,"E9.7.39.0"),sQuery(id+"F0.wireOp",EDGE,"E9.11.39.0"),sQuery(id+"F0.wireOp",EDGE,"E9.14.39.0"),sQuery(id+"F0.wireOp",EDGE,"E9.1.40.0"),sQuery(id+"F0.wireOp",EDGE,"E9.3.40.0"),sQuery(id+"F0.wireOp",EDGE,"E9.7.40.0"),sQuery(id+"F0.wireOp",EDGE,"E9.11.40.0"),sQuery(id+"F0.wireOp",EDGE,"E9.14.40.0"),sQuery(id+"F0.wireOp",EDGE,"E9.1.41.0"),sQuery(id+"F0.wireOp",EDGE,"E9.3.41.0"),sQuery(id+"F0.wireOp",EDGE,"E9.7.41.0"),sQuery(id+"F0.wireOp",EDGE,"E9.11.41.0"),sQuery(id+"F0.wireOp",EDGE,"E9.14.41.0"),sQuery(id+"F0.wireOp",EDGE,"E9.1.42.0"),sQuery(id+"F0.wireOp",EDGE,"E9.3.42.0"),sQuery(id+"F0.wireOp",EDGE,"E9.7.42.0"),sQuery(id+"F0.wireOp",EDGE,"E9.11.42.0"),sQuery(id+"F0.wireOp",EDGE,"E9.14.42.0"),sQuery(id+"F0.wireOp",EDGE,"E9.1.43.0"),sQuery(id+"F0.wireOp",EDGE,"E9.3.43.0"),sQuery(id+"F0.wireOp",EDGE,"E9.7.43.0"),sQuery(id+"F0.wireOp",EDGE,"E9.11.43.0"),sQuery(id+"F0.wireOp",EDGE,"E9.14.43.0"),sQuery(id+"F0.wireOp",EDGE,"E9.1.44.0"),sQuery(id+"F0.wireOp",EDGE,"E9.3.44.0"),sQuery(id+"F0.wireOp",EDGE,"E9.7.44.0"),sQuery(id+"F0.wireOp",EDGE,"E9.11.44.0"),sQuery(id+"F0.wireOp",EDGE,"E9.14.44.0"),sQuery(id+"F0.wireOp",EDGE,"E9.1.45.0"),sQuery(id+"F0.wireOp",EDGE,"E9.3.45.0"),sQuery(id+"F0.wireOp",EDGE,"E9.7.45.0"),sQuery(id+"F0.wireOp",EDGE,"E9.11.45.0"),sQuery(id+"F0.wireOp",EDGE,"E9.14.45.0"),sQuery(id+"F0.wireOp",EDGE,"E9.1.46.0"),sQuery(id+"F0.wireOp",EDGE,"E9.3.46.0"),sQuery(id+"F0.wireOp",EDGE,"E9.7.46.0"),sQuery(id+"F0.wireOp",EDGE,"E9.11.46.0"),sQuery(id+"F0.wireOp",EDGE,"E9.14.46.0"),sQuery(id+"F0.wireOp",EDGE,"E9.1.47.0"),sQuery(id+"F0.wireOp",EDGE,"E9.3.47.0"),sQuery(id+"F0.wireOp",EDGE,"E9.7.47.0"),sQuery(id+"F0.wireOp",EDGE,"E9.11.47.0"),sQuery(id+"F0.wireOp",EDGE,"E9.14.47.0"),sQuery(id+"F0.wireOp",EDGE,"E9.1.48.0"),sQuery(id+"F0.wireOp",EDGE,"E9.3.48.0"),sQuery(id+"F0.wireOp",EDGE,"E9.7.48.0"),sQuery(id+"F0.wireOp",EDGE,"E9.11.48.0"),sQuery(id+"F0.wireOp",EDGE,"E9.14.48.0"),sQuery(id+"F0.wireOp",EDGE,"E9.1.49.0"),sQuery(id+"F0.wireOp",EDGE,"E9.3.49.0"),sQuery(id+"F0.wireOp",EDGE,"E9.7.49.0"),sQuery(id+"F0.wireOp",EDGE,"E9.11.49.0"),sQuery(id+"F0.wireOp",EDGE,"E9.14.49.0"),sQuery(id+"F0.wireOp",EDGE,"E9.1.50.0"),sQuery(id+"F0.wireOp",EDGE,"E9.3.50.0"),sQuery(id+"F0.wireOp",EDGE,"E9.7.50.0"),sQuery(id+"F0.wireOp",EDGE,"E9.11.50.0"),sQuery(id+"F0.wireOp",EDGE,"E9.14.50.0"),sQuery(id+"F0.wireOp",EDGE,"E9.1.51.0"),sQuery(id+"F0.wireOp",EDGE,"E9.3.51.0"),sQuery(id+"F0.wireOp",EDGE,"E9.7.51.0"),sQuery(id+"F0.wireOp",EDGE,"E9.11.51.0"),sQuery(id+"F0.wireOp",EDGE,"E9.14.51.0"),sQuery(id+"F0.wireOp",EDGE,"E9.1.52.0"),sQuery(id+"F0.wireOp",EDGE,"E9.3.52.0"),sQuery(id+"F0.wireOp",EDGE,"E9.7.52.0"),sQuery(id+"F0.wireOp",EDGE,"E9.11.52.0"),sQuery(id+"F0.wireOp",EDGE,"E9.14.52.0"),sQuery(id+"F0.wireOp",EDGE,"E9.1.53.0"),sQuery(id+"F0.wireOp",EDGE,"E9.3.53.0"),sQuery(id+"F0.wireOp",EDGE,"E9.7.53.0"),sQuery(id+"F0.wireOp",EDGE,"E9.11.53.0"),sQuery(id+"F0.wireOp",EDGE,"E9.14.53.0"),sQuery(id+"F0.wireOp",EDGE,"E9.1.54.0"),sQuery(id+"F0.wireOp",EDGE,"E9.3.54.0"),sQuery(id+"F0.wireOp",EDGE,"E9.7.54.0"),sQuery(id+"F0.wireOp",EDGE,"E9.11.54.0"),sQuery(id+"F0.wireOp",EDGE,"E9.14.54.0"),sQuery(id+"F0.wireOp",EDGE,"E9.1.55.0"),sQuery(id+"F0.wireOp",EDGE,"E9.3.55.0"),sQuery(id+"F0.wireOp",EDGE,"E9.7.55.0"),sQuery(id+"F0.wireOp",EDGE,"E9.11.55.0"),sQuery(id+"F0.wireOp",EDGE,"E9.14.55.0"),sQuery(id+"F0.wireOp",EDGE,"E9.1.56.0"),sQuery(id+"F0.wireOp",EDGE,"E9.3.56.0"),sQuery(id+"F0.wireOp",EDGE,"E9.7.56.0"),sQuery(id+"F0.wireOp",EDGE,"E9.11.56.0"),sQuery(id+"F0.wireOp",EDGE,"E9.14.56.0"),sQuery(id+"F0.wireOp",EDGE,"E9.1.57.0"),sQuery(id+"F0.wireOp",EDGE,"E9.3.57.0"),sQuery(id+"F0.wireOp",EDGE,"E9.7.57.0"),sQuery(id+"F0.wireOp",EDGE,"E9.11.57.0"),sQuery(id+"F0.wireOp",EDGE,"E9.14.57.0"),sQuery(id+"F0.wireOp",EDGE,"E9.1.58.0"),sQuery(id+"F0.wireOp",EDGE,"E9.3.58.0"),sQuery(id+"F0.wireOp",EDGE,"E9.7.58.0"),sQuery(id+"F0.wireOp",EDGE,"E9.11.58.0"),sQuery(id+"F0.wireOp",EDGE,"E9.14.58.0"),sQuery(id+"F0.wireOp",EDGE,"E9.1.59.0"),sQuery(id+"F0.wireOp",EDGE,"E9.3.59.0"),sQuery(id+"F0.wireOp",EDGE,"E9.7.59.0"),sQuery(id+"F0.wireOp",EDGE,"E9.11.59.0"),sQuery(id+"F0.wireOp",EDGE,"E9.14.59.0"),sQuery(id+"F2.wireOp",EDGE,"E26")])],"isStart":false})});
            var Q4;
            Q4=makeQuery(id+"F8.boolean.opBoolean","COPY",EDGE,{"derivedFrom":makeQuery(id+"F8.opExtrude","CAP_EDGE",EDGE,{"disambiguationData":[OSD([sQuery(id+"F0.wireOp",EDGE,"E0"),sQuery(id+"F0.wireOp",EDGE,"E1"),sQuery(id+"F0.wireOp",EDGE,"E3"),sQuery(id+"F0.wireOp",EDGE,"E4"),sQuery(id+"F0.wireOp",EDGE,"E5"),sQuery(id+"F0.wireOp",EDGE,"E6.trimOffspring"),sQuery(id+"F0.wireOp",EDGE,"E7"),sQuery(id+"F0.wireOp",EDGE,"E8.1.0"),sQuery(id+"F0.wireOp",EDGE,"E8.1.1"),sQuery(id+"F0.wireOp",EDGE,"E8.1.2"),sQuery(id+"F0.wireOp",EDGE,"E8.1.3"),sQuery(id+"F0.wireOp",EDGE,"E8.1.4"),sQuery(id+"F0.wireOp",EDGE,"E8.2.0"),sQuery(id+"F0.wireOp",EDGE,"E8.2.1"),sQuery(id+"F0.wireOp",EDGE,"E8.2.2"),sQuery(id+"F0.wireOp",EDGE,"E8.2.3"),sQuery(id+"F0.wireOp",EDGE,"E8.2.4"),sQuery(id+"F0.wireOp",EDGE,"E9.1.3.0"),sQuery(id+"F0.wireOp",EDGE,"E9.3.3.0"),sQuery(id+"F0.wireOp",EDGE,"E9.7.3.0"),sQuery(id+"F0.wireOp",EDGE,"E9.11.3.0"),sQuery(id+"F0.wireOp",EDGE,"E9.14.3.0"),sQuery(id+"F0.wireOp",EDGE,"E9.1.4.0"),sQuery(id+"F0.wireOp",EDGE,"E9.3.4.0"),sQuery(id+"F0.wireOp",EDGE,"E9.7.4.0"),sQuery(id+"F0.wireOp",EDGE,"E9.11.4.0"),sQuery(id+"F0.wireOp",EDGE,"E9.14.4.0"),sQuery(id+"F0.wireOp",EDGE,"E9.1.5.0"),sQuery(id+"F0.wireOp",EDGE,"E9.3.5.0"),sQuery(id+"F0.wireOp",EDGE,"E9.7.5.0"),sQuery(id+"F0.wireOp",EDGE,"E9.11.5.0"),sQuery(id+"F0.wireOp",EDGE,"E9.14.5.0"),sQuery(id+"F0.wireOp",EDGE,"E9.1.6.0"),sQuery(id+"F0.wireOp",EDGE,"E9.3.6.0"),sQuery(id+"F0.wireOp",EDGE,"E9.7.6.0"),sQuery(id+"F0.wireOp",EDGE,"E9.11.6.0"),sQuery(id+"F0.wireOp",EDGE,"E9.14.6.0"),sQuery(id+"F0.wireOp",EDGE,"E9.1.7.0"),sQuery(id+"F0.wireOp",EDGE,"E9.3.7.0"),sQuery(id+"F0.wireOp",EDGE,"E9.7.7.0"),sQuery(id+"F0.wireOp",EDGE,"E9.11.7.0"),sQuery(id+"F0.wireOp",EDGE,"E9.14.7.0"),sQuery(id+"F0.wireOp",EDGE,"E9.1.8.0"),sQuery(id+"F0.wireOp",EDGE,"E9.3.8.0"),sQuery(id+"F0.wireOp",EDGE,"E9.7.8.0"),sQuery(id+"F0.wireOp",EDGE,"E9.11.8.0"),sQuery(id+"F0.wireOp",EDGE,"E9.14.8.0"),sQuery(id+"F0.wireOp",EDGE,"E9.1.9.0"),sQuery(id+"F0.wireOp",EDGE,"E9.3.9.0"),sQuery(id+"F0.wireOp",EDGE,"E9.7.9.0"),sQuery(id+"F0.wireOp",EDGE,"E9.11.9.0"),sQuery(id+"F0.wireOp",EDGE,"E9.14.9.0"),sQuery(id+"F0.wireOp",EDGE,"E9.1.10.0"),sQuery(id+"F0.wireOp",EDGE,"E9.3.10.0"),sQuery(id+"F0.wireOp",EDGE,"E9.7.10.0"),sQuery(id+"F0.wireOp",EDGE,"E9.11.10.0"),sQuery(id+"F0.wireOp",EDGE,"E9.14.10.0"),sQuery(id+"F0.wireOp",EDGE,"E9.1.11.0"),sQuery(id+"F0.wireOp",EDGE,"E9.3.11.0"),sQuery(id+"F0.wireOp",EDGE,"E9.7.11.0"),sQuery(id+"F0.wireOp",EDGE,"E9.11.11.0"),sQuery(id+"F0.wireOp",EDGE,"E9.14.11.0"),sQuery(id+"F0.wireOp",EDGE,"E9.1.12.0"),sQuery(id+"F0.wireOp",EDGE,"E9.3.12.0"),sQuery(id+"F0.wireOp",EDGE,"E9.7.12.0"),sQuery(id+"F0.wireOp",EDGE,"E9.11.12.0"),sQuery(id+"F0.wireOp",EDGE,"E9.14.12.0"),sQuery(id+"F0.wireOp",EDGE,"E9.1.13.0"),sQuery(id+"F0.wireOp",EDGE,"E9.3.13.0"),sQuery(id+"F0.wireOp",EDGE,"E9.7.13.0"),sQuery(id+"F0.wireOp",EDGE,"E9.11.13.0"),sQuery(id+"F0.wireOp",EDGE,"E9.14.13.0"),sQuery(id+"F0.wireOp",EDGE,"E9.1.14.0"),sQuery(id+"F0.wireOp",EDGE,"E9.3.14.0"),sQuery(id+"F0.wireOp",EDGE,"E9.7.14.0"),sQuery(id+"F0.wireOp",EDGE,"E9.11.14.0"),sQuery(id+"F0.wireOp",EDGE,"E9.14.14.0"),sQuery(id+"F0.wireOp",EDGE,"E9.1.15.0"),sQuery(id+"F0.wireOp",EDGE,"E9.3.15.0"),sQuery(id+"F0.wireOp",EDGE,"E9.7.15.0"),sQuery(id+"F0.wireOp",EDGE,"E9.11.15.0"),sQuery(id+"F0.wireOp",EDGE,"E9.14.15.0"),sQuery(id+"F0.wireOp",EDGE,"E9.1.16.0"),sQuery(id+"F0.wireOp",EDGE,"E9.3.16.0"),sQuery(id+"F0.wireOp",EDGE,"E9.7.16.0"),sQuery(id+"F0.wireOp",EDGE,"E9.11.16.0"),sQuery(id+"F0.wireOp",EDGE,"E9.14.16.0"),sQuery(id+"F0.wireOp",EDGE,"E9.1.17.0"),sQuery(id+"F0.wireOp",EDGE,"E9.3.17.0"),sQuery(id+"F0.wireOp",EDGE,"E9.7.17.0"),sQuery(id+"F0.wireOp",EDGE,"E9.11.17.0"),sQuery(id+"F0.wireOp",EDGE,"E9.14.17.0"),sQuery(id+"F0.wireOp",EDGE,"E9.1.18.0"),sQuery(id+"F0.wireOp",EDGE,"E9.3.18.0"),sQuery(id+"F0.wireOp",EDGE,"E9.7.18.0"),sQuery(id+"F0.wireOp",EDGE,"E9.11.18.0"),sQuery(id+"F0.wireOp",EDGE,"E9.14.18.0"),sQuery(id+"F0.wireOp",EDGE,"E9.1.19.0"),sQuery(id+"F0.wireOp",EDGE,"E9.3.19.0"),sQuery(id+"F0.wireOp",EDGE,"E9.7.19.0"),sQuery(id+"F0.wireOp",EDGE,"E9.11.19.0"),sQuery(id+"F0.wireOp",EDGE,"E9.14.19.0"),sQuery(id+"F0.wireOp",EDGE,"E9.1.20.0"),sQuery(id+"F0.wireOp",EDGE,"E9.3.20.0"),sQuery(id+"F0.wireOp",EDGE,"E9.7.20.0"),sQuery(id+"F0.wireOp",EDGE,"E9.11.20.0"),sQuery(id+"F0.wireOp",EDGE,"E9.14.20.0"),sQuery(id+"F0.wireOp",EDGE,"E9.1.21.0"),sQuery(id+"F0.wireOp",EDGE,"E9.3.21.0"),sQuery(id+"F0.wireOp",EDGE,"E9.7.21.0"),sQuery(id+"F0.wireOp",EDGE,"E9.11.21.0"),sQuery(id+"F0.wireOp",EDGE,"E9.14.21.0"),sQuery(id+"F0.wireOp",EDGE,"E9.1.22.0"),sQuery(id+"F0.wireOp",EDGE,"E9.3.22.0"),sQuery(id+"F0.wireOp",EDGE,"E9.7.22.0"),sQuery(id+"F0.wireOp",EDGE,"E9.11.22.0"),sQuery(id+"F0.wireOp",EDGE,"E9.14.22.0"),sQuery(id+"F0.wireOp",EDGE,"E9.1.23.0"),sQuery(id+"F0.wireOp",EDGE,"E9.3.23.0"),sQuery(id+"F0.wireOp",EDGE,"E9.7.23.0"),sQuery(id+"F0.wireOp",EDGE,"E9.11.23.0"),sQuery(id+"F0.wireOp",EDGE,"E9.14.23.0"),sQuery(id+"F0.wireOp",EDGE,"E9.1.24.0"),sQuery(id+"F0.wireOp",EDGE,"E9.3.24.0"),sQuery(id+"F0.wireOp",EDGE,"E9.7.24.0"),sQuery(id+"F0.wireOp",EDGE,"E9.11.24.0"),sQuery(id+"F0.wireOp",EDGE,"E9.14.24.0"),sQuery(id+"F0.wireOp",EDGE,"E9.1.25.0"),sQuery(id+"F0.wireOp",EDGE,"E9.3.25.0"),sQuery(id+"F0.wireOp",EDGE,"E9.7.25.0"),sQuery(id+"F0.wireOp",EDGE,"E9.11.25.0"),sQuery(id+"F0.wireOp",EDGE,"E9.14.25.0"),sQuery(id+"F0.wireOp",EDGE,"E9.1.26.0"),sQuery(id+"F0.wireOp",EDGE,"E9.3.26.0"),sQuery(id+"F0.wireOp",EDGE,"E9.7.26.0"),sQuery(id+"F0.wireOp",EDGE,"E9.11.26.0"),sQuery(id+"F0.wireOp",EDGE,"E9.14.26.0"),sQuery(id+"F0.wireOp",EDGE,"E9.1.27.0"),sQuery(id+"F0.wireOp",EDGE,"E9.3.27.0"),sQuery(id+"F0.wireOp",EDGE,"E9.7.27.0"),sQuery(id+"F0.wireOp",EDGE,"E9.11.27.0"),sQuery(id+"F0.wireOp",EDGE,"E9.14.27.0"),sQuery(id+"F0.wireOp",EDGE,"E9.1.28.0"),sQuery(id+"F0.wireOp",EDGE,"E9.3.28.0"),sQuery(id+"F0.wireOp",EDGE,"E9.7.28.0"),sQuery(id+"F0.wireOp",EDGE,"E9.11.28.0"),sQuery(id+"F0.wireOp",EDGE,"E9.14.28.0"),sQuery(id+"F0.wireOp",EDGE,"E9.1.29.0"),sQuery(id+"F0.wireOp",EDGE,"E9.3.29.0"),sQuery(id+"F0.wireOp",EDGE,"E9.7.29.0"),sQuery(id+"F0.wireOp",EDGE,"E9.11.29.0"),sQuery(id+"F0.wireOp",EDGE,"E9.14.29.0"),sQuery(id+"F0.wireOp",EDGE,"E9.1.30.0"),sQuery(id+"F0.wireOp",EDGE,"E9.3.30.0"),sQuery(id+"F0.wireOp",EDGE,"E9.7.30.0"),sQuery(id+"F0.wireOp",EDGE,"E9.11.30.0"),sQuery(id+"F0.wireOp",EDGE,"E9.14.30.0"),sQuery(id+"F0.wireOp",EDGE,"E9.1.31.0"),sQuery(id+"F0.wireOp",EDGE,"E9.3.31.0"),sQuery(id+"F0.wireOp",EDGE,"E9.7.31.0"),sQuery(id+"F0.wireOp",EDGE,"E9.11.31.0"),sQuery(id+"F0.wireOp",EDGE,"E9.14.31.0"),sQuery(id+"F0.wireOp",EDGE,"E9.1.32.0"),sQuery(id+"F0.wireOp",EDGE,"E9.3.32.0"),sQuery(id+"F0.wireOp",EDGE,"E9.7.32.0"),sQuery(id+"F0.wireOp",EDGE,"E9.11.32.0"),sQuery(id+"F0.wireOp",EDGE,"E9.14.32.0"),sQuery(id+"F0.wireOp",EDGE,"E9.1.33.0"),sQuery(id+"F0.wireOp",EDGE,"E9.3.33.0"),sQuery(id+"F0.wireOp",EDGE,"E9.7.33.0"),sQuery(id+"F0.wireOp",EDGE,"E9.11.33.0"),sQuery(id+"F0.wireOp",EDGE,"E9.14.33.0"),sQuery(id+"F0.wireOp",EDGE,"E9.1.34.0"),sQuery(id+"F0.wireOp",EDGE,"E9.3.34.0"),sQuery(id+"F0.wireOp",EDGE,"E9.7.34.0"),sQuery(id+"F0.wireOp",EDGE,"E9.11.34.0"),sQuery(id+"F0.wireOp",EDGE,"E9.14.34.0"),sQuery(id+"F0.wireOp",EDGE,"E9.1.35.0"),sQuery(id+"F0.wireOp",EDGE,"E9.3.35.0"),sQuery(id+"F0.wireOp",EDGE,"E9.7.35.0"),sQuery(id+"F0.wireOp",EDGE,"E9.11.35.0"),sQuery(id+"F0.wireOp",EDGE,"E9.14.35.0"),sQuery(id+"F0.wireOp",EDGE,"E9.1.36.0"),sQuery(id+"F0.wireOp",EDGE,"E9.3.36.0"),sQuery(id+"F0.wireOp",EDGE,"E9.7.36.0"),sQuery(id+"F0.wireOp",EDGE,"E9.11.36.0"),sQuery(id+"F0.wireOp",EDGE,"E9.14.36.0"),sQuery(id+"F0.wireOp",EDGE,"E9.1.37.0"),sQuery(id+"F0.wireOp",EDGE,"E9.3.37.0"),sQuery(id+"F0.wireOp",EDGE,"E9.7.37.0"),sQuery(id+"F0.wireOp",EDGE,"E9.11.37.0"),sQuery(id+"F0.wireOp",EDGE,"E9.14.37.0"),sQuery(id+"F0.wireOp",EDGE,"E9.1.38.0"),sQuery(id+"F0.wireOp",EDGE,"E9.3.38.0"),sQuery(id+"F0.wireOp",EDGE,"E9.7.38.0"),sQuery(id+"F0.wireOp",EDGE,"E9.11.38.0"),sQuery(id+"F0.wireOp",EDGE,"E9.14.38.0"),sQuery(id+"F0.wireOp",EDGE,"E9.1.39.0"),sQuery(id+"F0.wireOp",EDGE,"E9.3.39.0"),sQuery(id+"F0.wireOp",EDGE,"E9.7.39.0"),sQuery(id+"F0.wireOp",EDGE,"E9.11.39.0"),sQuery(id+"F0.wireOp",EDGE,"E9.14.39.0"),sQuery(id+"F0.wireOp",EDGE,"E9.1.40.0"),sQuery(id+"F0.wireOp",EDGE,"E9.3.40.0"),sQuery(id+"F0.wireOp",EDGE,"E9.7.40.0"),sQuery(id+"F0.wireOp",EDGE,"E9.11.40.0"),sQuery(id+"F0.wireOp",EDGE,"E9.14.40.0"),sQuery(id+"F0.wireOp",EDGE,"E9.1.41.0"),sQuery(id+"F0.wireOp",EDGE,"E9.3.41.0"),sQuery(id+"F0.wireOp",EDGE,"E9.7.41.0"),sQuery(id+"F0.wireOp",EDGE,"E9.11.41.0"),sQuery(id+"F0.wireOp",EDGE,"E9.14.41.0"),sQuery(id+"F0.wireOp",EDGE,"E9.1.42.0"),sQuery(id+"F0.wireOp",EDGE,"E9.3.42.0"),sQuery(id+"F0.wireOp",EDGE,"E9.7.42.0"),sQuery(id+"F0.wireOp",EDGE,"E9.11.42.0"),sQuery(id+"F0.wireOp",EDGE,"E9.14.42.0"),sQuery(id+"F0.wireOp",EDGE,"E9.1.43.0"),sQuery(id+"F0.wireOp",EDGE,"E9.3.43.0"),sQuery(id+"F0.wireOp",EDGE,"E9.7.43.0"),sQuery(id+"F0.wireOp",EDGE,"E9.11.43.0"),sQuery(id+"F0.wireOp",EDGE,"E9.14.43.0"),sQuery(id+"F0.wireOp",EDGE,"E9.1.44.0"),sQuery(id+"F0.wireOp",EDGE,"E9.3.44.0"),sQuery(id+"F0.wireOp",EDGE,"E9.7.44.0"),sQuery(id+"F0.wireOp",EDGE,"E9.11.44.0"),sQuery(id+"F0.wireOp",EDGE,"E9.14.44.0"),sQuery(id+"F0.wireOp",EDGE,"E9.1.45.0"),sQuery(id+"F0.wireOp",EDGE,"E9.3.45.0"),sQuery(id+"F0.wireOp",EDGE,"E9.7.45.0"),sQuery(id+"F0.wireOp",EDGE,"E9.11.45.0"),sQuery(id+"F0.wireOp",EDGE,"E9.14.45.0"),sQuery(id+"F0.wireOp",EDGE,"E9.1.46.0"),sQuery(id+"F0.wireOp",EDGE,"E9.3.46.0"),sQuery(id+"F0.wireOp",EDGE,"E9.7.46.0"),sQuery(id+"F0.wireOp",EDGE,"E9.11.46.0"),sQuery(id+"F0.wireOp",EDGE,"E9.14.46.0"),sQuery(id+"F0.wireOp",EDGE,"E9.1.47.0"),sQuery(id+"F0.wireOp",EDGE,"E9.3.47.0"),sQuery(id+"F0.wireOp",EDGE,"E9.7.47.0"),sQuery(id+"F0.wireOp",EDGE,"E9.11.47.0"),sQuery(id+"F0.wireOp",EDGE,"E9.14.47.0"),sQuery(id+"F0.wireOp",EDGE,"E9.1.48.0"),sQuery(id+"F0.wireOp",EDGE,"E9.3.48.0"),sQuery(id+"F0.wireOp",EDGE,"E9.7.48.0"),sQuery(id+"F0.wireOp",EDGE,"E9.11.48.0"),sQuery(id+"F0.wireOp",EDGE,"E9.14.48.0"),sQuery(id+"F0.wireOp",EDGE,"E9.1.49.0"),sQuery(id+"F0.wireOp",EDGE,"E9.3.49.0"),sQuery(id+"F0.wireOp",EDGE,"E9.7.49.0"),sQuery(id+"F0.wireOp",EDGE,"E9.11.49.0"),sQuery(id+"F0.wireOp",EDGE,"E9.14.49.0"),sQuery(id+"F0.wireOp",EDGE,"E9.1.50.0"),sQuery(id+"F0.wireOp",EDGE,"E9.3.50.0"),sQuery(id+"F0.wireOp",EDGE,"E9.7.50.0"),sQuery(id+"F0.wireOp",EDGE,"E9.11.50.0"),sQuery(id+"F0.wireOp",EDGE,"E9.14.50.0"),sQuery(id+"F0.wireOp",EDGE,"E9.1.51.0"),sQuery(id+"F0.wireOp",EDGE,"E9.3.51.0"),sQuery(id+"F0.wireOp",EDGE,"E9.7.51.0"),sQuery(id+"F0.wireOp",EDGE,"E9.11.51.0"),sQuery(id+"F0.wireOp",EDGE,"E9.14.51.0"),sQuery(id+"F0.wireOp",EDGE,"E9.1.52.0"),sQuery(id+"F0.wireOp",EDGE,"E9.3.52.0"),sQuery(id+"F0.wireOp",EDGE,"E9.7.52.0"),sQuery(id+"F0.wireOp",EDGE,"E9.11.52.0"),sQuery(id+"F0.wireOp",EDGE,"E9.14.52.0"),sQuery(id+"F0.wireOp",EDGE,"E9.1.53.0"),sQuery(id+"F0.wireOp",EDGE,"E9.3.53.0"),sQuery(id+"F0.wireOp",EDGE,"E9.7.53.0"),sQuery(id+"F0.wireOp",EDGE,"E9.11.53.0"),sQuery(id+"F0.wireOp",EDGE,"E9.14.53.0"),sQuery(id+"F0.wireOp",EDGE,"E9.1.54.0"),sQuery(id+"F0.wireOp",EDGE,"E9.3.54.0"),sQuery(id+"F0.wireOp",EDGE,"E9.7.54.0"),sQuery(id+"F0.wireOp",EDGE,"E9.11.54.0"),sQuery(id+"F0.wireOp",EDGE,"E9.14.54.0"),sQuery(id+"F0.wireOp",EDGE,"E9.1.55.0"),sQuery(id+"F0.wireOp",EDGE,"E9.3.55.0"),sQuery(id+"F0.wireOp",EDGE,"E9.7.55.0"),sQuery(id+"F0.wireOp",EDGE,"E9.11.55.0"),sQuery(id+"F0.wireOp",EDGE,"E9.14.55.0"),sQuery(id+"F0.wireOp",EDGE,"E9.1.56.0"),sQuery(id+"F0.wireOp",EDGE,"E9.3.56.0"),sQuery(id+"F0.wireOp",EDGE,"E9.7.56.0"),sQuery(id+"F0.wireOp",EDGE,"E9.11.56.0"),sQuery(id+"F0.wireOp",EDGE,"E9.14.56.0"),sQuery(id+"F0.wireOp",EDGE,"E9.1.57.0"),sQuery(id+"F0.wireOp",EDGE,"E9.3.57.0"),sQuery(id+"F0.wireOp",EDGE,"E9.7.57.0"),sQuery(id+"F0.wireOp",EDGE,"E9.11.57.0"),sQuery(id+"F0.wireOp",EDGE,"E9.14.57.0"),sQuery(id+"F0.wireOp",EDGE,"E9.1.58.0"),sQuery(id+"F0.wireOp",EDGE,"E9.3.58.0"),sQuery(id+"F0.wireOp",EDGE,"E9.7.58.0"),sQuery(id+"F0.wireOp",EDGE,"E9.11.58.0"),sQuery(id+"F0.wireOp",EDGE,"E9.14.58.0"),sQuery(id+"F0.wireOp",EDGE,"E9.1.59.0"),sQuery(id+"F0.wireOp",EDGE,"E9.3.59.0"),sQuery(id+"F0.wireOp",EDGE,"E9.7.59.0"),sQuery(id+"F0.wireOp",EDGE,"E9.11.59.0"),sQuery(id+"F0.wireOp",EDGE,"E9.14.59.0"),sQuery(id+"F2.wireOp",EDGE,"E37.trimOffspring")])],"isStart":false})});
            var Q5;
            Q5=makeQuery(id+"F6.boolean.opBoolean","INTERSECT",EDGE,{"derivedFrom":[makeQuery(id+"F4.boolean.opBoolean","COPY",FACE,{"derivedFrom":makeQuery(id+"F4.opExtrude","CAP_FACE",FACE,{"disambiguationData":[OSD([sQuery(id+"F3.wireOp",EDGE,"E42"),sQuery(id+"F3.wireOp",EDGE,"E43")])],"isStart":false})}),makeQuery(id+"F6.opExtrude","SWEPT_FACE",FACE,{"disambiguationData":[OSD([sQuery(id+"F2.wireOp",EDGE,"E20.0")])]})]});
            var Q6;
            Q6=makeQuery(id+"F6.boolean.opBoolean","INTERSECT",EDGE,{"derivedFrom":[makeQuery(id+"F4.boolean.opBoolean","COPY",FACE,{"derivedFrom":makeQuery(id+"F4.opExtrude","CAP_FACE",FACE,{"disambiguationData":[OSD([sQuery(id+"F3.wireOp",EDGE,"E42"),sQuery(id+"F3.wireOp",EDGE,"E43")])],"isStart":false})}),makeQuery(id+"F6.opExtrude","SWEPT_FACE",FACE,{"disambiguationData":[OSD([sQuery(id+"F2.wireOp",EDGE,"E19")])]})]});
            var Q7;
            Q7=makeQuery(id+"F6.boolean.opBoolean","INTERSECT",EDGE,{"derivedFrom":[makeQuery(id+"F4.boolean.opBoolean","COPY",FACE,{"derivedFrom":makeQuery(id+"F4.opExtrude","CAP_FACE",FACE,{"disambiguationData":[OSD([sQuery(id+"F3.wireOp",EDGE,"E42"),sQuery(id+"F3.wireOp",EDGE,"E43")])],"isStart":false})}),makeQuery(id+"F6.opExtrude","SWEPT_FACE",FACE,{"disambiguationData":[OSD([sQuery(id+"F2.wireOp",EDGE,"E22.0")])]})]});
            var Q8;
            Q8=makeQuery(id+"F6.boolean.opBoolean","INTERSECT",EDGE,{"derivedFrom":[makeQuery(id+"F4.boolean.opBoolean","COPY",FACE,{"derivedFrom":makeQuery(id+"F4.opExtrude","CAP_FACE",FACE,{"disambiguationData":[OSD([sQuery(id+"F3.wireOp",EDGE,"E42"),sQuery(id+"F3.wireOp",EDGE,"E43")])],"isStart":false})}),makeQuery(id+"F6.opExtrude","SWEPT_FACE",FACE,{"disambiguationData":[OSD([sQuery(id+"F2.wireOp",EDGE,"E36.trimOffspring")])]})]});
            fillet(context, id + "F9", {"entities" : qUnion([Q0, Q1, Q2, Q3, Q4, Q5, Q6, Q7, Q8]), "radius" : 1 * mm, "tangentPropagation" : true, "allowEdgeOverflow" : false});
        }
        {
            var Q0;
            Q0=makeQuery(id+"F4.boolean.opBoolean","COPY",EDGE,{"derivedFrom":makeQuery(id+"F4.opExtrude","CAP_EDGE",EDGE,{"disambiguationData":[OSD([sQuery(id+"F3.wireOp",EDGE,"E43")])],"isStart":false})});
            var Q1;
            Q1=makeQuery(id+"F8.boolean.opBoolean","COPY",EDGE,{"derivedFrom":makeQuery(id+"F8.opExtrude","CAP_EDGE",EDGE,{"disambiguationData":[OSD([sQuery(id+"F7.wireOp",EDGE,"E47")])],"isStart":false})});
            var Q2;
            Q2=makeQuery(id+"F4.boolean.opBoolean","COPY",EDGE,{"derivedFrom":makeQuery(id+"F4.opExtrude","CAP_EDGE",EDGE,{"disambiguationData":[OSD([sQuery(id+"F3.wireOp",EDGE,"E42")])],"isStart":false})});
            var Q3;
            Q3=makeQuery(id+"F8.boolean.opBoolean","COPY",EDGE,{"derivedFrom":makeQuery(id+"F8.opExtrude","CAP_EDGE",EDGE,{"disambiguationData":[OSD([sQuery(id+"F7.wireOp",EDGE,"E44")])],"isStart":false})});
            fillet(context, id + "F10", {"entities" : qUnion([Q0, Q1, Q2, Q3]), "radius" : 1 * mm, "tangentPropagation" : true, "allowEdgeOverflow" : false});
        }
    });
